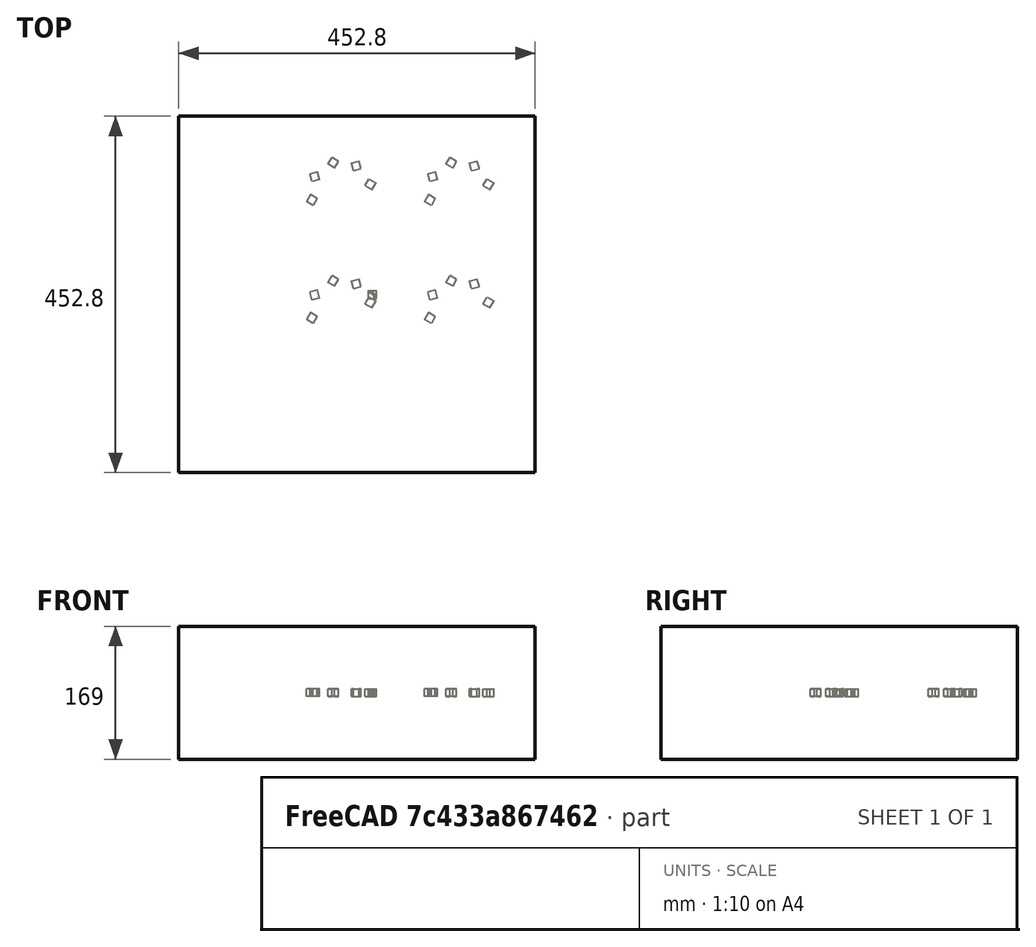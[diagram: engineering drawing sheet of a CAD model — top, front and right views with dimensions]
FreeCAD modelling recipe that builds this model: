
FCSTD DOCUMENT  (FreeCAD 1.0R39109 (Git))
Label: orthoArray-of-polarArray-of-Part
License: All rights reserved
LicenseURL: http://en.wikipedia.org/wiki/All_rights_reserved
objects: App::DocumentObjectGroupPython×1251, Part::FeaturePython×5, App::Part×5
note: 4 computed .brp shape members not serialized (recipe doc carries the construction recipe); baked Part::Feature solids carry a one-line shape summary decoded from their .brp

FEATURE [App::DocumentObjectGroupPython] HALFPI  # scripted group (container) (typed FeaturePython)
  name = HALFPI
  value = pi/2.
FEATURE [App::DocumentObjectGroupPython] PI  # scripted group (container) (typed FeaturePython)
  name = PI
  value = 1.*pi
FEATURE [App::DocumentObjectGroupPython] TWOPI  # scripted group (container) (typed FeaturePython)
  name = TWOPI
  value = 2.*pi
FEATURE [App::DocumentObjectGroupPython] Constants  # scripted group (container) (typed FeaturePython)
  Group = -> [HALFPI,PI,TWOPI]
FEATURE [App::DocumentObjectGroupPython] Variables  # scripted group (container) (typed FeaturePython)
FEATURE [App::DocumentObjectGroupPython] Quantities  # scripted group (container) (typed FeaturePython)
FEATURE [App::DocumentObjectGroupPython] Isotopes  # scripted group (container) (typed FeaturePython)
FEATURE [App::DocumentObjectGroupPython] Elements  # scripted group (container) (typed FeaturePython)
FEATURE [App::DocumentObjectGroupPython] Matrix  # scripted group (container) (typed FeaturePython)
FEATURE [App::DocumentObjectGroupPython] Surfaces  # scripted group (container) (typed FeaturePython)
FEATURE [App::DocumentObjectGroupPython] Opticals  # scripted group (container) (typed FeaturePython)
  Group = -> [Matrix,Surfaces]
FEATURE [App::DocumentObjectGroupPython] G4Isotopes  # scripted group (container) (typed FeaturePython)
FEATURE [App::DocumentObjectGroupPython] H_element  # scripted group (container) (typed FeaturePython)
  Z = 1
  atom_value = 1.008
  formula = H
  name = H_element
FEATURE [App::DocumentObjectGroupPython] He_element  # scripted group (container) (typed FeaturePython)
  Z = 2
  atom_value = 4.0026
  formula = He
  name = He_element
FEATURE [App::DocumentObjectGroupPython] Li_element  # scripted group (container) (typed FeaturePython)
  Z = 3
  atom_value = 6.94
  formula = Li
  name = Li_element
FEATURE [App::DocumentObjectGroupPython] Be_element  # scripted group (container) (typed FeaturePython)
  Z = 4
  atom_value = 9.01218
  formula = Be
  name = Be_element
FEATURE [App::DocumentObjectGroupPython] B_element  # scripted group (container) (typed FeaturePython)
  Z = 5
  atom_value = 10.81
  formula = B
  name = B_element
FEATURE [App::DocumentObjectGroupPython] C_element  # scripted group (container) (typed FeaturePython)
  Z = 6
  atom_value = 12.011
  formula = C
  name = C_element
FEATURE [App::DocumentObjectGroupPython] N_element  # scripted group (container) (typed FeaturePython)
  Z = 7
  atom_value = 14.007
  formula = N
  name = N_element
FEATURE [App::DocumentObjectGroupPython] O_element  # scripted group (container) (typed FeaturePython)
  Z = 8
  atom_value = 15.999
  formula = O
  name = O_element
FEATURE [App::DocumentObjectGroupPython] F_element  # scripted group (container) (typed FeaturePython)
  Z = 9
  atom_value = 18.9984
  formula = F
  name = F_element
FEATURE [App::DocumentObjectGroupPython] Ne_element  # scripted group (container) (typed FeaturePython)
  Z = 10
  atom_value = 20.1797
  formula = Ne
  name = Ne_element
FEATURE [App::DocumentObjectGroupPython] Na_element  # scripted group (container) (typed FeaturePython)
  Z = 11
  atom_value = 22.9898
  formula = Na
  name = Na_element
FEATURE [App::DocumentObjectGroupPython] Mg_element  # scripted group (container) (typed FeaturePython)
  Z = 12
  atom_value = 24.305
  formula = Mg
  name = Mg_element
FEATURE [App::DocumentObjectGroupPython] Al_element  # scripted group (container) (typed FeaturePython)
  Z = 13
  atom_value = 26.9815
  formula = Al
  name = Al_element
FEATURE [App::DocumentObjectGroupPython] Si_element  # scripted group (container) (typed FeaturePython)
  Z = 14
  atom_value = 28.085
  formula = Si
  name = Si_element
FEATURE [App::DocumentObjectGroupPython] P_element  # scripted group (container) (typed FeaturePython)
  Z = 15
  atom_value = 30.9738
  formula = P
  name = P_element
FEATURE [App::DocumentObjectGroupPython] S_element  # scripted group (container) (typed FeaturePython)
  Z = 16
  atom_value = 32.06
  formula = S
  name = S_element
FEATURE [App::DocumentObjectGroupPython] Cl_element  # scripted group (container) (typed FeaturePython)
  Z = 17
  atom_value = 35.45
  formula = Cl
  name = Cl_element
FEATURE [App::DocumentObjectGroupPython] Ar_element  # scripted group (container) (typed FeaturePython)
  Z = 18
  atom_value = 39.95
  formula = Ar
  name = Ar_element
FEATURE [App::DocumentObjectGroupPython] K_element  # scripted group (container) (typed FeaturePython)
  Z = 19
  atom_value = 39.0983
  formula = K
  name = K_element
FEATURE [App::DocumentObjectGroupPython] Ca_element  # scripted group (container) (typed FeaturePython)
  Z = 20
  atom_value = 40.078
  formula = Ca
  name = Ca_element
FEATURE [App::DocumentObjectGroupPython] Sc_element  # scripted group (container) (typed FeaturePython)
  Z = 21
  atom_value = 44.9559
  formula = Sc
  name = Sc_element
FEATURE [App::DocumentObjectGroupPython] Ti_element  # scripted group (container) (typed FeaturePython)
  Z = 22
  atom_value = 47.867
  formula = Ti
  name = Ti_element
FEATURE [App::DocumentObjectGroupPython] V_element  # scripted group (container) (typed FeaturePython)
  Z = 23
  atom_value = 50.9415
  formula = V
  name = V_element
FEATURE [App::DocumentObjectGroupPython] Cr_element  # scripted group (container) (typed FeaturePython)
  Z = 24
  atom_value = 51.9961
  formula = Cr
  name = Cr_element
FEATURE [App::DocumentObjectGroupPython] Mn_element  # scripted group (container) (typed FeaturePython)
  Z = 25
  atom_value = 54.938
  formula = Mn
  name = Mn_element
FEATURE [App::DocumentObjectGroupPython] Fe_element  # scripted group (container) (typed FeaturePython)
  Z = 26
  atom_value = 55.845
  formula = Fe
  name = Fe_element
FEATURE [App::DocumentObjectGroupPython] Co_element  # scripted group (container) (typed FeaturePython)
  Z = 27
  atom_value = 58.9332
  formula = Co
  name = Co_element
FEATURE [App::DocumentObjectGroupPython] Ni_element  # scripted group (container) (typed FeaturePython)
  Z = 28
  atom_value = 58.6934
  formula = Ni
  name = Ni_element
FEATURE [App::DocumentObjectGroupPython] Cu_element  # scripted group (container) (typed FeaturePython)
  Z = 29
  atom_value = 63.546
  formula = Cu
  name = Cu_element
FEATURE [App::DocumentObjectGroupPython] Zn_element  # scripted group (container) (typed FeaturePython)
  Z = 30
  atom_value = 65.38
  formula = Zn
  name = Zn_element
FEATURE [App::DocumentObjectGroupPython] Ga_element  # scripted group (container) (typed FeaturePython)
  Z = 31
  atom_value = 69.723
  formula = Ga
  name = Ga_element
FEATURE [App::DocumentObjectGroupPython] Ge_element  # scripted group (container) (typed FeaturePython)
  Z = 32
  atom_value = 72.63
  formula = Ge
  name = Ge_element
FEATURE [App::DocumentObjectGroupPython] As_element  # scripted group (container) (typed FeaturePython)
  Z = 33
  atom_value = 74.9216
  formula = As
  name = As_element
FEATURE [App::DocumentObjectGroupPython] Se_element  # scripted group (container) (typed FeaturePython)
  Z = 34
  atom_value = 78.971
  formula = Se
  name = Se_element
FEATURE [App::DocumentObjectGroupPython] Br_element  # scripted group (container) (typed FeaturePython)
  Z = 35
  atom_value = 79.904
  formula = Br
  name = Br_element
FEATURE [App::DocumentObjectGroupPython] Kr_element  # scripted group (container) (typed FeaturePython)
  Z = 36
  atom_value = 83.798
  formula = Kr
  name = Kr_element
FEATURE [App::DocumentObjectGroupPython] Rb_element  # scripted group (container) (typed FeaturePython)
  Z = 37
  atom_value = 85.4678
  formula = Rb
  name = Rb_element
FEATURE [App::DocumentObjectGroupPython] Sr_element  # scripted group (container) (typed FeaturePython)
  Z = 38
  atom_value = 87.62
  formula = Sr
  name = Sr_element
FEATURE [App::DocumentObjectGroupPython] Y_element  # scripted group (container) (typed FeaturePython)
  Z = 39
  atom_value = 88.9058
  formula = Y
  name = Y_element
FEATURE [App::DocumentObjectGroupPython] Zr_element  # scripted group (container) (typed FeaturePython)
  Z = 40
  atom_value = 91.224
  formula = Zr
  name = Zr_element
FEATURE [App::DocumentObjectGroupPython] Nb_element  # scripted group (container) (typed FeaturePython)
  Z = 41
  atom_value = 92.9064
  formula = Nb
  name = Nb_element
FEATURE [App::DocumentObjectGroupPython] Mo_element  # scripted group (container) (typed FeaturePython)
  Z = 42
  atom_value = 95.95
  formula = Mo
  name = Mo_element
FEATURE [App::DocumentObjectGroupPython] Tc_element  # scripted group (container) (typed FeaturePython)
  Z = 43
  atom_value = 97
  formula = Tc
  name = Tc_element
FEATURE [App::DocumentObjectGroupPython] Ru_element  # scripted group (container) (typed FeaturePython)
  Z = 44
  atom_value = 101.07
  formula = Ru
  name = Ru_element
FEATURE [App::DocumentObjectGroupPython] Rh_element  # scripted group (container) (typed FeaturePython)
  Z = 45
  atom_value = 102.905
  formula = Rh
  name = Rh_element
FEATURE [App::DocumentObjectGroupPython] Pd_element  # scripted group (container) (typed FeaturePython)
  Z = 46
  atom_value = 106.42
  formula = Pd
  name = Pd_element
FEATURE [App::DocumentObjectGroupPython] Ag_element  # scripted group (container) (typed FeaturePython)
  Z = 47
  atom_value = 107.868
  formula = Ag
  name = Ag_element
FEATURE [App::DocumentObjectGroupPython] Cd_element  # scripted group (container) (typed FeaturePython)
  Z = 48
  atom_value = 112.414
  formula = Cd
  name = Cd_element
FEATURE [App::DocumentObjectGroupPython] In_element  # scripted group (container) (typed FeaturePython)
  Z = 49
  atom_value = 114.818
  formula = In
  name = In_element
FEATURE [App::DocumentObjectGroupPython] Sn_element  # scripted group (container) (typed FeaturePython)
  Z = 50
  atom_value = 118.71
  formula = Sn
  name = Sn_element
FEATURE [App::DocumentObjectGroupPython] Sb_element  # scripted group (container) (typed FeaturePython)
  Z = 51
  atom_value = 121.76
  formula = Sb
  name = Sb_element
FEATURE [App::DocumentObjectGroupPython] Te_element  # scripted group (container) (typed FeaturePython)
  Z = 52
  atom_value = 127.6
  formula = Te
  name = Te_element
FEATURE [App::DocumentObjectGroupPython] I_element  # scripted group (container) (typed FeaturePython)
  Z = 53
  atom_value = 126.904
  formula = I
  name = I_element
FEATURE [App::DocumentObjectGroupPython] Xe_element  # scripted group (container) (typed FeaturePython)
  Z = 54
  atom_value = 131.293
  formula = Xe
  name = Xe_element
FEATURE [App::DocumentObjectGroupPython] Cs_element  # scripted group (container) (typed FeaturePython)
  Z = 55
  atom_value = 132.905
  formula = Cs
  name = Cs_element
FEATURE [App::DocumentObjectGroupPython] Ba_element  # scripted group (container) (typed FeaturePython)
  Z = 56
  atom_value = 137.327
  formula = Ba
  name = Ba_element
FEATURE [App::DocumentObjectGroupPython] La_element  # scripted group (container) (typed FeaturePython)
  Z = 57
  atom_value = 138.905
  formula = La
  name = La_element
FEATURE [App::DocumentObjectGroupPython] Ce_element  # scripted group (container) (typed FeaturePython)
  Z = 58
  atom_value = 140.116
  formula = Ce
  name = Ce_element
FEATURE [App::DocumentObjectGroupPython] Pr_element  # scripted group (container) (typed FeaturePython)
  Z = 59
  atom_value = 140.908
  formula = Pr
  name = Pr_element
FEATURE [App::DocumentObjectGroupPython] Nd_element  # scripted group (container) (typed FeaturePython)
  Z = 60
  atom_value = 144.242
  formula = Nd
  name = Nd_element
FEATURE [App::DocumentObjectGroupPython] Pm_element  # scripted group (container) (typed FeaturePython)
  Z = 61
  atom_value = 145
  formula = Pm
  name = Pm_element
FEATURE [App::DocumentObjectGroupPython] Sm_element  # scripted group (container) (typed FeaturePython)
  Z = 62
  atom_value = 150.36
  formula = Sm
  name = Sm_element
FEATURE [App::DocumentObjectGroupPython] Eu_element  # scripted group (container) (typed FeaturePython)
  Z = 63
  atom_value = 151.964
  formula = Eu
  name = Eu_element
FEATURE [App::DocumentObjectGroupPython] Gd_element  # scripted group (container) (typed FeaturePython)
  Z = 64
  atom_value = 157.25
  formula = Gd
  name = Gd_element
FEATURE [App::DocumentObjectGroupPython] Tb_element  # scripted group (container) (typed FeaturePython)
  Z = 65
  atom_value = 158.925
  formula = Tb
  name = Tb_element
FEATURE [App::DocumentObjectGroupPython] Dy_element  # scripted group (container) (typed FeaturePython)
  Z = 66
  atom_value = 162.5
  formula = Dy
  name = Dy_element
FEATURE [App::DocumentObjectGroupPython] Ho_element  # scripted group (container) (typed FeaturePython)
  Z = 67
  atom_value = 164.93
  formula = Ho
  name = Ho_element
FEATURE [App::DocumentObjectGroupPython] Er_element  # scripted group (container) (typed FeaturePython)
  Z = 68
  atom_value = 167.259
  formula = Er
  name = Er_element
FEATURE [App::DocumentObjectGroupPython] Tm_element  # scripted group (container) (typed FeaturePython)
  Z = 69
  atom_value = 168.934
  formula = Tm
  name = Tm_element
FEATURE [App::DocumentObjectGroupPython] Yb_element  # scripted group (container) (typed FeaturePython)
  Z = 70
  atom_value = 173.045
  formula = Yb
  name = Yb_element
FEATURE [App::DocumentObjectGroupPython] Lu_element  # scripted group (container) (typed FeaturePython)
  Z = 71
  atom_value = 174.967
  formula = Lu
  name = Lu_element
FEATURE [App::DocumentObjectGroupPython] Hf_element  # scripted group (container) (typed FeaturePython)
  Z = 72
  atom_value = 178.49
  formula = Hf
  name = Hf_element
FEATURE [App::DocumentObjectGroupPython] Ta_element  # scripted group (container) (typed FeaturePython)
  Z = 73
  atom_value = 180.948
  formula = Ta
  name = Ta_element
FEATURE [App::DocumentObjectGroupPython] W_element  # scripted group (container) (typed FeaturePython)
  Z = 74
  atom_value = 183.84
  formula = W
  name = W_element
FEATURE [App::DocumentObjectGroupPython] Re_element  # scripted group (container) (typed FeaturePython)
  Z = 75
  atom_value = 186.207
  formula = Re
  name = Re_element
FEATURE [App::DocumentObjectGroupPython] Os_element  # scripted group (container) (typed FeaturePython)
  Z = 76
  atom_value = 190.23
  formula = Os
  name = Os_element
FEATURE [App::DocumentObjectGroupPython] Ir_element  # scripted group (container) (typed FeaturePython)
  Z = 77
  atom_value = 192.217
  formula = Ir
  name = Ir_element
FEATURE [App::DocumentObjectGroupPython] Pt_element  # scripted group (container) (typed FeaturePython)
  Z = 78
  atom_value = 195.084
  formula = Pt
  name = Pt_element
FEATURE [App::DocumentObjectGroupPython] Au_element  # scripted group (container) (typed FeaturePython)
  Z = 79
  atom_value = 196.967
  formula = Au
  name = Au_element
FEATURE [App::DocumentObjectGroupPython] Hg_element  # scripted group (container) (typed FeaturePython)
  Z = 80
  atom_value = 200.592
  formula = Hg
  name = Hg_element
FEATURE [App::DocumentObjectGroupPython] Tl_element  # scripted group (container) (typed FeaturePython)
  Z = 81
  atom_value = 204.38
  formula = Tl
  name = Tl_element
FEATURE [App::DocumentObjectGroupPython] Pb_element  # scripted group (container) (typed FeaturePython)
  Z = 82
  atom_value = 207.2
  formula = Pb
  name = Pb_element
FEATURE [App::DocumentObjectGroupPython] Bi_element  # scripted group (container) (typed FeaturePython)
  Z = 83
  atom_value = 208.98
  formula = Bi
  name = Bi_element
FEATURE [App::DocumentObjectGroupPython] Po_element  # scripted group (container) (typed FeaturePython)
  Z = 84
  atom_value = 209
  formula = Po
  name = Po_element
FEATURE [App::DocumentObjectGroupPython] At_element  # scripted group (container) (typed FeaturePython)
  Z = 85
  atom_value = 210
  formula = At
  name = At_element
FEATURE [App::DocumentObjectGroupPython] Rn_element  # scripted group (container) (typed FeaturePython)
  Z = 86
  atom_value = 222
  formula = Rn
  name = Rn_element
FEATURE [App::DocumentObjectGroupPython] Fr_element  # scripted group (container) (typed FeaturePython)
  Z = 87
  atom_value = 223
  formula = Fr
  name = Fr_element
FEATURE [App::DocumentObjectGroupPython] Ra_element  # scripted group (container) (typed FeaturePython)
  Z = 88
  atom_value = 226
  formula = Ra
  name = Ra_element
FEATURE [App::DocumentObjectGroupPython] Ac_element  # scripted group (container) (typed FeaturePython)
  Z = 89
  atom_value = 227
  formula = Ac
  name = Ac_element
FEATURE [App::DocumentObjectGroupPython] Th_element  # scripted group (container) (typed FeaturePython)
  Z = 90
  atom_value = 232.038
  formula = Th
  name = Th_element
FEATURE [App::DocumentObjectGroupPython] Pa_element  # scripted group (container) (typed FeaturePython)
  Z = 91
  atom_value = 231.036
  formula = Pa
  name = Pa_element
FEATURE [App::DocumentObjectGroupPython] U_element  # scripted group (container) (typed FeaturePython)
  Z = 92
  atom_value = 238.029
  formula = U
  name = U_element
FEATURE [App::DocumentObjectGroupPython] Np_element  # scripted group (container) (typed FeaturePython)
  Z = 93
  atom_value = 237
  formula = Np
  name = Np_element
FEATURE [App::DocumentObjectGroupPython] Pu_element  # scripted group (container) (typed FeaturePython)
  Z = 94
  atom_value = 244
  formula = Pu
  name = Pu_element
FEATURE [App::DocumentObjectGroupPython] Am_element  # scripted group (container) (typed FeaturePython)
  Z = 95
  atom_value = 243
  formula = Am
  name = Am_element
FEATURE [App::DocumentObjectGroupPython] Cm_element  # scripted group (container) (typed FeaturePython)
  Z = 96
  atom_value = 247
  formula = Cm
  name = Cm_element
FEATURE [App::DocumentObjectGroupPython] Bk_element  # scripted group (container) (typed FeaturePython)
  Z = 97
  atom_value = 247
  formula = Bk
  name = Bk_element
FEATURE [App::DocumentObjectGroupPython] Cf_element  # scripted group (container) (typed FeaturePython)
  Z = 98
  atom_value = 251
  formula = Cf
  name = Cf_element
FEATURE [App::DocumentObjectGroupPython] G4Elements  # scripted group (container) (typed FeaturePython)
  Group = -> [H_element,He_element,Li_element,Be_element,B_element,C_element,N_element,O_element,F_element,Ne_element,Na_element,Mg_element,Al_element,Si_element,P_element,S_element,Cl_element,Ar_element,K_element,Ca_element,Sc_element,Ti_element,V_element,Cr_element,Mn_element,Fe_element,Co_element,Ni_element,Cu_element,Zn_element,Ga_element,Ge_element,As_element,Se_element,Br_element,Kr_element,Rb_element,+61 more]
FEATURE [App::DocumentObjectGroupPython] H_element001  label="H_element : 0.101"  # scripted group (container) (typed FeaturePython)
  n = 0.101327
FEATURE [App::DocumentObjectGroupPython] C_element001  label="C_element : 0.775"  # scripted group (container) (typed FeaturePython)
  n = 0.7755
FEATURE [App::DocumentObjectGroupPython] N_element001  label="N_element : 0.035"  # scripted group (container) (typed FeaturePython)
  n = 0.035057
FEATURE [App::DocumentObjectGroupPython] O_element001  label="O_element : 0.052"  # scripted group (container) (typed FeaturePython)
  n = 0.0523159
FEATURE [App::DocumentObjectGroupPython] F_element001  label="F_element : 0.017"  # scripted group (container) (typed FeaturePython)
  n = 0.017422
FEATURE [App::DocumentObjectGroupPython] Ca_element001  label="Ca_element : 0.018"  # scripted group (container) (typed FeaturePython)
  n = 0.018378
FEATURE [App::DocumentObjectGroupPython] G4_A_150_TISSUE  label="G4_A-150_TISSUE"  # scripted group (container) (typed FeaturePython)
  Dunit = g/cm3
  Dvalue = 1.127
  Group = -> [H_element001,C_element001,N_element001,O_element001,F_element001,Ca_element001]
  conduct = 2
  density = 1
  expand = 3
  formula = G4_A-150_TISSUE
  name = G4_A-150_TISSUE
  specific = 4
FEATURE [App::DocumentObjectGroupPython] C_element002  label="C_element : 3"  # scripted group (container) (typed FeaturePython)
  n = 3
  ref = C_element
FEATURE [App::DocumentObjectGroupPython] H_element002  label="H_element : 6"  # scripted group (container) (typed FeaturePython)
  n = 6
  ref = H_element
FEATURE [App::DocumentObjectGroupPython] O_element002  label="O_element : 1"  # scripted group (container) (typed FeaturePython)
  n = 1
  ref = O_element
FEATURE [App::DocumentObjectGroupPython] G4_ACETONE  # scripted group (container) (typed FeaturePython)
  Dunit = g/cm3
  Dvalue = 0.7899
  Group = -> [C_element002,H_element002,O_element002]
  conduct = 2
  density = 1
  expand = 3
  formula = G4_ACETONE
  name = G4_ACETONE
  specific = 4
FEATURE [App::DocumentObjectGroupPython] C_element003  label="C_element : 2"  # scripted group (container) (typed FeaturePython)
  n = 2
  ref = C_element
FEATURE [App::DocumentObjectGroupPython] H_element003  label="H_element : 2"  # scripted group (container) (typed FeaturePython)
  n = 2
  ref = H_element
FEATURE [App::DocumentObjectGroupPython] G4_ACETYLENE  # scripted group (container) (typed FeaturePython)
  Dunit = g/cm3
  Dvalue = 0.0010967
  Group = -> [C_element003,H_element003]
  conduct = 2
  density = 1
  expand = 3
  formula = G4_ACETYLENE
  name = G4_ACETYLENE
  specific = 4
FEATURE [App::DocumentObjectGroupPython] C_element004  label="C_element : 5"  # scripted group (container) (typed FeaturePython)
  n = 5
  ref = C_element
FEATURE [App::DocumentObjectGroupPython] H_element004  label="H_element : 5"  # scripted group (container) (typed FeaturePython)
  n = 5
  ref = H_element
FEATURE [App::DocumentObjectGroupPython] N_element002  label="N_element : 5"  # scripted group (container) (typed FeaturePython)
  n = 5
  ref = N_element
FEATURE [App::DocumentObjectGroupPython] G4_ADENINE  # scripted group (container) (typed FeaturePython)
  Dunit = g/cm3
  Dvalue = 1.6
  Group = -> [C_element004,H_element004,N_element002]
  conduct = 2
  density = 1
  expand = 3
  formula = G4_ADENINE
  name = G4_ADENINE
  specific = 4
FEATURE [App::DocumentObjectGroupPython] H_element005  label="H_element : 0.114"  # scripted group (container) (typed FeaturePython)
  n = 0.114
FEATURE [App::DocumentObjectGroupPython] C_element005  label="C_element : 0.598"  # scripted group (container) (typed FeaturePython)
  n = 0.598
FEATURE [App::DocumentObjectGroupPython] N_element003  label="N_element : 0.007"  # scripted group (container) (typed FeaturePython)
  n = 0.007
FEATURE [App::DocumentObjectGroupPython] O_element003  label="O_element : 0.278"  # scripted group (container) (typed FeaturePython)
  n = 0.278
FEATURE [App::DocumentObjectGroupPython] Na_element001  label="Na_element : 0.001"  # scripted group (container) (typed FeaturePython)
  n = 0.001
FEATURE [App::DocumentObjectGroupPython] S_element001  label="S_element : 0.001"  # scripted group (container) (typed FeaturePython)
  n = 0.001
FEATURE [App::DocumentObjectGroupPython] Cl_element001  label="Cl_element : 0.001"  # scripted group (container) (typed FeaturePython)
  n = 0.001
FEATURE [App::DocumentObjectGroupPython] G4_ADIPOSE_TISSUE_ICRP  # scripted group (container) (typed FeaturePython)
  Dunit = g/cm3
  Dvalue = 0.95
  Group = -> [H_element005,C_element005,N_element003,O_element003,Na_element001,S_element001,Cl_element001]
  conduct = 2
  density = 1
  expand = 3
  formula = G4_ADIPOSE_TISSUE_ICRP
  name = G4_ADIPOSE_TISSUE_ICRP
  specific = 4
FEATURE [App::DocumentObjectGroupPython] C_element006  label="C_element : 0.000"  # scripted group (container) (typed FeaturePython)
  n = 0.000124
FEATURE [App::DocumentObjectGroupPython] N_element004  label="N_element : 0.755"  # scripted group (container) (typed FeaturePython)
  n = 0.755268
FEATURE [App::DocumentObjectGroupPython] O_element004  label="O_element : 0.232"  # scripted group (container) (typed FeaturePython)
  n = 0.231781
FEATURE [App::DocumentObjectGroupPython] Ar_element001  label="Ar_element : 0.013"  # scripted group (container) (typed FeaturePython)
  n = 0.012827
FEATURE [App::DocumentObjectGroupPython] G4_AIR  # scripted group (container) (typed FeaturePython)
  Dunit = g/cm3
  Dvalue = 0.00120479
  Group = -> [C_element006,N_element004,O_element004,Ar_element001]
  conduct = 2
  density = 1
  expand = 3
  formula = G4_AIR
  name = G4_AIR
  specific = 4
FEATURE [App::DocumentObjectGroupPython] C_element007  label="C_element : 006"  # scripted group (container) (typed FeaturePython)
  n = 3
  ref = C_element
FEATURE [App::DocumentObjectGroupPython] H_element006  label="H_element : 7"  # scripted group (container) (typed FeaturePython)
  n = 7
  ref = H_element
FEATURE [App::DocumentObjectGroupPython] N_element005  label="N_element : 1"  # scripted group (container) (typed FeaturePython)
  n = 1
  ref = N_element
FEATURE [App::DocumentObjectGroupPython] O_element005  label="O_element : 2"  # scripted group (container) (typed FeaturePython)
  n = 2
  ref = O_element
FEATURE [App::DocumentObjectGroupPython] G4_ALANINE  # scripted group (container) (typed FeaturePython)
  Dunit = g/cm3
  Dvalue = 1.42
  Group = -> [C_element007,H_element006,N_element005,O_element005]
  conduct = 2
  density = 1
  expand = 3
  formula = G4_ALANINE
  name = G4_ALANINE
  specific = 4
FEATURE [App::DocumentObjectGroupPython] Al_element001  label="Al_element : 2"  # scripted group (container) (typed FeaturePython)
  n = 2
  ref = Al_element
FEATURE [App::DocumentObjectGroupPython] O_element006  label="O_element : 3"  # scripted group (container) (typed FeaturePython)
  n = 3
  ref = O_element
FEATURE [App::DocumentObjectGroupPython] G4_ALUMINUM_OXIDE  # scripted group (container) (typed FeaturePython)
  Dunit = g/cm3
  Dvalue = 3.97
  Group = -> [Al_element001,O_element006]
  conduct = 2
  density = 1
  expand = 3
  formula = G4_ALUMINUM_OXIDE
  name = G4_ALUMINUM_OXIDE
  specific = 4
FEATURE [App::DocumentObjectGroupPython] H_element007  label="H_element : 0.106"  # scripted group (container) (typed FeaturePython)
  n = 0.10593
FEATURE [App::DocumentObjectGroupPython] C_element008  label="C_element : 0.789"  # scripted group (container) (typed FeaturePython)
  n = 0.788974
FEATURE [App::DocumentObjectGroupPython] O_element007  label="O_element : 0.105"  # scripted group (container) (typed FeaturePython)
  n = 0.105096
FEATURE [App::DocumentObjectGroupPython] G4_AMBER  # scripted group (container) (typed FeaturePython)
  Dunit = g/cm3
  Dvalue = 1.1
  Group = -> [H_element007,C_element008,O_element007]
  conduct = 2
  density = 1
  expand = 3
  formula = G4_AMBER
  name = G4_AMBER
  specific = 4
FEATURE [App::DocumentObjectGroupPython] N_element006  label="N_element : 006"  # scripted group (container) (typed FeaturePython)
  n = 1
  ref = N_element
FEATURE [App::DocumentObjectGroupPython] H_element008  label="H_element : 3"  # scripted group (container) (typed FeaturePython)
  n = 3
  ref = H_element
FEATURE [App::DocumentObjectGroupPython] G4_AMMONIA  # scripted group (container) (typed FeaturePython)
  Dunit = g/cm3
  Dvalue = 0.000826019
  Group = -> [N_element006,H_element008]
  conduct = 2
  density = 1
  expand = 3
  formula = G4_AMMONIA
  name = G4_AMMONIA
  specific = 4
FEATURE [App::DocumentObjectGroupPython] C_element009  label="C_element : 6"  # scripted group (container) (typed FeaturePython)
  n = 6
  ref = C_element
FEATURE [App::DocumentObjectGroupPython] H_element009  label="H_element : 008"  # scripted group (container) (typed FeaturePython)
  n = 7
  ref = H_element
FEATURE [App::DocumentObjectGroupPython] N_element007  label="N_element : 007"  # scripted group (container) (typed FeaturePython)
  n = 1
  ref = N_element
FEATURE [App::DocumentObjectGroupPython] G4_ANILINE  # scripted group (container) (typed FeaturePython)
  Dunit = g/cm3
  Dvalue = 1.0235
  Group = -> [C_element009,H_element009,N_element007]
  conduct = 2
  density = 1
  expand = 3
  formula = G4_ANILINE
  name = G4_ANILINE
  specific = 4
FEATURE [App::DocumentObjectGroupPython] C_element010  label="C_element : 14"  # scripted group (container) (typed FeaturePython)
  n = 14
  ref = C_element
FEATURE [App::DocumentObjectGroupPython] H_element010  label="H_element : 10"  # scripted group (container) (typed FeaturePython)
  n = 10
  ref = H_element
FEATURE [App::DocumentObjectGroupPython] G4_ANTHRACENE  # scripted group (container) (typed FeaturePython)
  Dunit = g/cm3
  Dvalue = 1.283
  Group = -> [C_element010,H_element010]
  conduct = 2
  density = 1
  expand = 3
  formula = G4_ANTHRACENE
  name = G4_ANTHRACENE
  specific = 4
FEATURE [App::DocumentObjectGroupPython] H_element011  label="H_element : 0.065"  # scripted group (container) (typed FeaturePython)
  n = 0.0654709
FEATURE [App::DocumentObjectGroupPython] C_element011  label="C_element : 0.537"  # scripted group (container) (typed FeaturePython)
  n = 0.536944
FEATURE [App::DocumentObjectGroupPython] N_element008  label="N_element : 0.021"  # scripted group (container) (typed FeaturePython)
  n = 0.0215
FEATURE [App::DocumentObjectGroupPython] O_element008  label="O_element : 0.032"  # scripted group (container) (typed FeaturePython)
  n = 0.032085
FEATURE [App::DocumentObjectGroupPython] F_element002  label="F_element : 0.167"  # scripted group (container) (typed FeaturePython)
  n = 0.167411
FEATURE [App::DocumentObjectGroupPython] Ca_element002  label="Ca_element : 0.177"  # scripted group (container) (typed FeaturePython)
  n = 0.176589
FEATURE [App::DocumentObjectGroupPython] G4_B_100_BONE  label="G4_B-100_BONE"  # scripted group (container) (typed FeaturePython)
  Dunit = g/cm3
  Dvalue = 1.45
  Group = -> [H_element011,C_element011,N_element008,O_element008,F_element002,Ca_element002]
  conduct = 2
  density = 1
  expand = 3
  formula = G4_B-100_BONE
  name = G4_B-100_BONE
  specific = 4
FEATURE [App::DocumentObjectGroupPython] H_element012  label="H_element : 0.057"  # scripted group (container) (typed FeaturePython)
  n = 0.057441
FEATURE [App::DocumentObjectGroupPython] C_element012  label="C_element : 0.790"  # scripted group (container) (typed FeaturePython)
  n = 0.774591
FEATURE [App::DocumentObjectGroupPython] O_element009  label="O_element : 0.168"  # scripted group (container) (typed FeaturePython)
  n = 0.167968
FEATURE [App::DocumentObjectGroupPython] G4_BAKELITE  # scripted group (container) (typed FeaturePython)
  Dunit = g/cm3
  Dvalue = 1.25
  Group = -> [H_element012,C_element012,O_element009]
  conduct = 2
  density = 1
  expand = 3
  formula = G4_BAKELITE
  name = G4_BAKELITE
  specific = 4
FEATURE [App::DocumentObjectGroupPython] Ba_element001  label="Ba_element : 1"  # scripted group (container) (typed FeaturePython)
  n = 1
  ref = Ba_element
FEATURE [App::DocumentObjectGroupPython] F_element003  label="F_element : 2"  # scripted group (container) (typed FeaturePython)
  n = 2
  ref = F_element
FEATURE [App::DocumentObjectGroupPython] G4_BARIUM_FLUORIDE  # scripted group (container) (typed FeaturePython)
  Dunit = g/cm3
  Dvalue = 4.89
  Group = -> [Ba_element001,F_element003]
  conduct = 2
  density = 1
  expand = 3
  formula = G4_BARIUM_FLUORIDE
  name = G4_BARIUM_FLUORIDE
  specific = 4
FEATURE [App::DocumentObjectGroupPython] Ba_element002  label="Ba_element : 002"  # scripted group (container) (typed FeaturePython)
  n = 1
  ref = Ba_element
FEATURE [App::DocumentObjectGroupPython] S_element002  label="S_element : 1"  # scripted group (container) (typed FeaturePython)
  n = 1
  ref = S_element
FEATURE [App::DocumentObjectGroupPython] O_element010  label="O_element : 4"  # scripted group (container) (typed FeaturePython)
  n = 4
  ref = O_element
FEATURE [App::DocumentObjectGroupPython] G4_BARIUM_SULFATE  # scripted group (container) (typed FeaturePython)
  Dunit = g/cm3
  Dvalue = 4.5
  Group = -> [Ba_element002,S_element002,O_element010]
  conduct = 2
  density = 1
  expand = 3
  formula = G4_BARIUM_SULFATE
  name = G4_BARIUM_SULFATE
  specific = 4
FEATURE [App::DocumentObjectGroupPython] C_element013  label="C_element : 007"  # scripted group (container) (typed FeaturePython)
  n = 6
  ref = C_element
FEATURE [App::DocumentObjectGroupPython] H_element013  label="H_element : 009"  # scripted group (container) (typed FeaturePython)
  n = 6
  ref = H_element
FEATURE [App::DocumentObjectGroupPython] G4_BENZENE  # scripted group (container) (typed FeaturePython)
  Dunit = g/cm3
  Dvalue = 0.87865
  Group = -> [C_element013,H_element013]
  conduct = 2
  density = 1
  expand = 3
  formula = G4_BENZENE
  name = G4_BENZENE
  specific = 4
FEATURE [App::DocumentObjectGroupPython] Be_element001  label="Be_element : 1"  # scripted group (container) (typed FeaturePython)
  n = 1
  ref = Be_element
FEATURE [App::DocumentObjectGroupPython] O_element011  label="O_element : 005"  # scripted group (container) (typed FeaturePython)
  n = 1
  ref = O_element
FEATURE [App::DocumentObjectGroupPython] G4_BERYLLIUM_OXIDE  # scripted group (container) (typed FeaturePython)
  Dunit = g/cm3
  Dvalue = 3.01
  Group = -> [Be_element001,O_element011]
  conduct = 2
  density = 1
  expand = 3
  formula = G4_BERYLLIUM_OXIDE
  name = G4_BERYLLIUM_OXIDE
  specific = 4
FEATURE [App::DocumentObjectGroupPython] Bi_element001  label="Bi_element : 4"  # scripted group (container) (typed FeaturePython)
  n = 4
  ref = Bi_element
FEATURE [App::DocumentObjectGroupPython] Ge_element001  label="Ge_element : 3"  # scripted group (container) (typed FeaturePython)
  n = 3
  ref = Ge_element
FEATURE [App::DocumentObjectGroupPython] O_element012  label="O_element : 12"  # scripted group (container) (typed FeaturePython)
  n = 12
  ref = O_element
FEATURE [App::DocumentObjectGroupPython] G4_BGO  # scripted group (container) (typed FeaturePython)
  Dunit = g/cm3
  Dvalue = 7.13
  Group = -> [Bi_element001,Ge_element001,O_element012]
  conduct = 2
  density = 1
  expand = 3
  formula = G4_BGO
  name = G4_BGO
  specific = 4
FEATURE [App::DocumentObjectGroupPython] H_element014  label="H_element : 0.102"  # scripted group (container) (typed FeaturePython)
  n = 0.102
FEATURE [App::DocumentObjectGroupPython] C_element014  label="C_element : 0.110"  # scripted group (container) (typed FeaturePython)
  n = 0.11
FEATURE [App::DocumentObjectGroupPython] N_element009  label="N_element : 0.033"  # scripted group (container) (typed FeaturePython)
  n = 0.033
FEATURE [App::DocumentObjectGroupPython] O_element013  label="O_element : 0.745"  # scripted group (container) (typed FeaturePython)
  n = 0.745
FEATURE [App::DocumentObjectGroupPython] Na_element002  label="Na_element : 0.002"  # scripted group (container) (typed FeaturePython)
  n = 0.001
FEATURE [App::DocumentObjectGroupPython] P_element001  label="P_element : 0.001"  # scripted group (container) (typed FeaturePython)
  n = 0.001
FEATURE [App::DocumentObjectGroupPython] S_element003  label="S_element : 0.002"  # scripted group (container) (typed FeaturePython)
  n = 0.002
FEATURE [App::DocumentObjectGroupPython] Cl_element002  label="Cl_element : 0.003"  # scripted group (container) (typed FeaturePython)
  n = 0.003
FEATURE [App::DocumentObjectGroupPython] K_element001  label="K_element : 0.002"  # scripted group (container) (typed FeaturePython)
  n = 0.002
FEATURE [App::DocumentObjectGroupPython] Fe_element001  label="Fe_element : 0.001"  # scripted group (container) (typed FeaturePython)
  n = 0.001
FEATURE [App::DocumentObjectGroupPython] G4_BLOOD_ICRP  # scripted group (container) (typed FeaturePython)
  Dunit = g/cm3
  Dvalue = 1.06
  Group = -> [H_element014,C_element014,N_element009,O_element013,Na_element002,P_element001,S_element003,Cl_element002,K_element001,Fe_element001]
  conduct = 2
  density = 1
  expand = 3
  formula = G4_BLOOD_ICRP
  name = G4_BLOOD_ICRP
  specific = 4
FEATURE [App::DocumentObjectGroupPython] H_element015  label="H_element : 0.064"  # scripted group (container) (typed FeaturePython)
  n = 0.064
FEATURE [App::DocumentObjectGroupPython] C_element015  label="C_element : 0.278"  # scripted group (container) (typed FeaturePython)
  n = 0.278
FEATURE [App::DocumentObjectGroupPython] N_element010  label="N_element : 0.027"  # scripted group (container) (typed FeaturePython)
  n = 0.027
FEATURE [App::DocumentObjectGroupPython] O_element014  label="O_element : 0.410"  # scripted group (container) (typed FeaturePython)
  n = 0.41
FEATURE [App::DocumentObjectGroupPython] Mg_element001  label="Mg_element : 0.002"  # scripted group (container) (typed FeaturePython)
  n = 0.002
FEATURE [App::DocumentObjectGroupPython] P_element002  label="P_element : 0.070"  # scripted group (container) (typed FeaturePython)
  n = 0.07
FEATURE [App::DocumentObjectGroupPython] S_element004  label="S_element : 0.003"  # scripted group (container) (typed FeaturePython)
  n = 0.002
FEATURE [App::DocumentObjectGroupPython] Ca_element003  label="Ca_element : 0.147"  # scripted group (container) (typed FeaturePython)
  n = 0.147
FEATURE [App::DocumentObjectGroupPython] G4_BONE_COMPACT_ICRU  # scripted group (container) (typed FeaturePython)
  Dunit = g/cm3
  Dvalue = 1.85
  Group = -> [H_element015,C_element015,N_element010,O_element014,Mg_element001,P_element002,S_element004,Ca_element003]
  conduct = 2
  density = 1
  expand = 3
  formula = G4_BONE_COMPACT_ICRU
  name = G4_BONE_COMPACT_ICRU
  specific = 4
FEATURE [App::DocumentObjectGroupPython] H_element016  label="H_element : 0.034"  # scripted group (container) (typed FeaturePython)
  n = 0.034
FEATURE [App::DocumentObjectGroupPython] C_element016  label="C_element : 0.155"  # scripted group (container) (typed FeaturePython)
  n = 0.155
FEATURE [App::DocumentObjectGroupPython] N_element011  label="N_element : 0.042"  # scripted group (container) (typed FeaturePython)
  n = 0.042
FEATURE [App::DocumentObjectGroupPython] O_element015  label="O_element : 0.435"  # scripted group (container) (typed FeaturePython)
  n = 0.435
FEATURE [App::DocumentObjectGroupPython] Na_element003  label="Na_element : 0.003"  # scripted group (container) (typed FeaturePython)
  n = 0.001
FEATURE [App::DocumentObjectGroupPython] Mg_element002  label="Mg_element : 0.003"  # scripted group (container) (typed FeaturePython)
  n = 0.002
FEATURE [App::DocumentObjectGroupPython] P_element003  label="P_element : 0.103"  # scripted group (container) (typed FeaturePython)
  n = 0.103
FEATURE [App::DocumentObjectGroupPython] S_element005  label="S_element : 0.004"  # scripted group (container) (typed FeaturePython)
  n = 0.003
FEATURE [App::DocumentObjectGroupPython] Ca_element004  label="Ca_element : 0.225"  # scripted group (container) (typed FeaturePython)
  n = 0.225
FEATURE [App::DocumentObjectGroupPython] G4_BONE_CORTICAL_ICRP  # scripted group (container) (typed FeaturePython)
  Dunit = g/cm3
  Dvalue = 1.92
  Group = -> [H_element016,C_element016,N_element011,O_element015,Na_element003,Mg_element002,P_element003,S_element005,Ca_element004]
  conduct = 2
  density = 1
  expand = 3
  formula = G4_BONE_CORTICAL_ICRP
  name = G4_BONE_CORTICAL_ICRP
  specific = 4
FEATURE [App::DocumentObjectGroupPython] B_element001  label="B_element : 4"  # scripted group (container) (typed FeaturePython)
  n = 4
  ref = B_element
FEATURE [App::DocumentObjectGroupPython] C_element017  label="C_element : 1"  # scripted group (container) (typed FeaturePython)
  n = 1
  ref = C_element
FEATURE [App::DocumentObjectGroupPython] G4_BORON_CARBIDE  # scripted group (container) (typed FeaturePython)
  Dunit = g/cm3
  Dvalue = 2.52
  Group = -> [B_element001,C_element017]
  conduct = 2
  density = 1
  expand = 3
  formula = G4_BORON_CARBIDE
  name = G4_BORON_CARBIDE
  specific = 4
FEATURE [App::DocumentObjectGroupPython] B_element002  label="B_element : 2"  # scripted group (container) (typed FeaturePython)
  n = 2
  ref = B_element
FEATURE [App::DocumentObjectGroupPython] O_element016  label="O_element : 006"  # scripted group (container) (typed FeaturePython)
  n = 3
  ref = O_element
FEATURE [App::DocumentObjectGroupPython] G4_BORON_OXIDE  # scripted group (container) (typed FeaturePython)
  Dunit = g/cm3
  Dvalue = 1.812
  Group = -> [B_element002,O_element016]
  conduct = 2
  density = 1
  expand = 3
  formula = G4_BORON_OXIDE
  name = G4_BORON_OXIDE
  specific = 4
FEATURE [App::DocumentObjectGroupPython] H_element017  label="H_element : 0.107"  # scripted group (container) (typed FeaturePython)
  n = 0.107
FEATURE [App::DocumentObjectGroupPython] C_element018  label="C_element : 0.145"  # scripted group (container) (typed FeaturePython)
  n = 0.145
FEATURE [App::DocumentObjectGroupPython] N_element012  label="N_element : 0.022"  # scripted group (container) (typed FeaturePython)
  n = 0.022
FEATURE [App::DocumentObjectGroupPython] O_element017  label="O_element : 0.712"  # scripted group (container) (typed FeaturePython)
  n = 0.712
FEATURE [App::DocumentObjectGroupPython] Na_element004  label="Na_element : 0.004"  # scripted group (container) (typed FeaturePython)
  n = 0.002
FEATURE [App::DocumentObjectGroupPython] P_element004  label="P_element : 0.004"  # scripted group (container) (typed FeaturePython)
  n = 0.004
FEATURE [App::DocumentObjectGroupPython] S_element006  label="S_element : 0.005"  # scripted group (container) (typed FeaturePython)
  n = 0.002
FEATURE [App::DocumentObjectGroupPython] Cl_element003  label="Cl_element : 0.004"  # scripted group (container) (typed FeaturePython)
  n = 0.003
FEATURE [App::DocumentObjectGroupPython] K_element002  label="K_element : 0.003"  # scripted group (container) (typed FeaturePython)
  n = 0.003
FEATURE [App::DocumentObjectGroupPython] G4_BRAIN_ICRP  # scripted group (container) (typed FeaturePython)
  Dunit = g/cm3
  Dvalue = 1.04
  Group = -> [H_element017,C_element018,N_element012,O_element017,Na_element004,P_element004,S_element006,Cl_element003,K_element002]
  conduct = 2
  density = 1
  expand = 3
  formula = G4_BRAIN_ICRP
  name = G4_BRAIN_ICRP
  specific = 4
FEATURE [App::DocumentObjectGroupPython] C_element019  label="C_element : 4"  # scripted group (container) (typed FeaturePython)
  n = 4
  ref = C_element
FEATURE [App::DocumentObjectGroupPython] H_element018  label="H_element : 010"  # scripted group (container) (typed FeaturePython)
  n = 10
  ref = H_element
FEATURE [App::DocumentObjectGroupPython] G4_BUTANE  # scripted group (container) (typed FeaturePython)
  Dunit = g/cm3
  Dvalue = 0.00249343
  Group = -> [C_element019,H_element018]
  conduct = 2
  density = 1
  expand = 3
  formula = G4_BUTANE
  name = G4_BUTANE
  specific = 4
FEATURE [App::DocumentObjectGroupPython] C_element020  label="C_element : 008"  # scripted group (container) (typed FeaturePython)
  n = 4
  ref = C_element
FEATURE [App::DocumentObjectGroupPython] H_element019  label="H_element : 011"  # scripted group (container) (typed FeaturePython)
  n = 10
  ref = H_element
FEATURE [App::DocumentObjectGroupPython] O_element018  label="O_element : 007"  # scripted group (container) (typed FeaturePython)
  n = 1
  ref = O_element
FEATURE [App::DocumentObjectGroupPython] G4_N_BUTYL_ALCOHOL  label="G4_N-BUTYL_ALCOHOL"  # scripted group (container) (typed FeaturePython)
  Dunit = g/cm3
  Dvalue = 0.8098
  Group = -> [C_element020,H_element019,O_element018]
  conduct = 2
  density = 1
  expand = 3
  formula = G4_N-BUTYL_ALCOHOL
  name = G4_N-BUTYL_ALCOHOL
  specific = 4
FEATURE [App::DocumentObjectGroupPython] H_element020  label="H_element : 0.025"  # scripted group (container) (typed FeaturePython)
  n = 0.02468
FEATURE [App::DocumentObjectGroupPython] C_element021  label="C_element : 0.502"  # scripted group (container) (typed FeaturePython)
  n = 0.501611
FEATURE [App::DocumentObjectGroupPython] O_element019  label="O_element : 0.005"  # scripted group (container) (typed FeaturePython)
  n = 0.004527
FEATURE [App::DocumentObjectGroupPython] F_element004  label="F_element : 0.465"  # scripted group (container) (typed FeaturePython)
  n = 0.465209
FEATURE [App::DocumentObjectGroupPython] Si_element001  label="Si_element : 0.004"  # scripted group (container) (typed FeaturePython)
  n = 0.003973
FEATURE [App::DocumentObjectGroupPython] G4_C_552  label="G4_C-552"  # scripted group (container) (typed FeaturePython)
  Dunit = g/cm3
  Dvalue = 1.76
  Group = -> [H_element020,C_element021,O_element019,F_element004,Si_element001]
  conduct = 2
  density = 1
  expand = 3
  formula = G4_C-552
  name = G4_C-552
  specific = 4
FEATURE [App::DocumentObjectGroupPython] Cd_element001  label="Cd_element : 1"  # scripted group (container) (typed FeaturePython)
  n = 1
  ref = Cd_element
FEATURE [App::DocumentObjectGroupPython] Te_element001  label="Te_element : 1"  # scripted group (container) (typed FeaturePython)
  n = 1
  ref = Te_element
FEATURE [App::DocumentObjectGroupPython] G4_CADMIUM_TELLURIDE  # scripted group (container) (typed FeaturePython)
  Dunit = g/cm3
  Dvalue = 6.2
  Group = -> [Cd_element001,Te_element001]
  conduct = 2
  density = 1
  expand = 3
  formula = G4_CADMIUM_TELLURIDE
  name = G4_CADMIUM_TELLURIDE
  specific = 4
FEATURE [App::DocumentObjectGroupPython] Cd_element002  label="Cd_element : 002"  # scripted group (container) (typed FeaturePython)
  n = 1
  ref = Cd_element
FEATURE [App::DocumentObjectGroupPython] W_element001  label="W_element : 1"  # scripted group (container) (typed FeaturePython)
  n = 1
  ref = W_element
FEATURE [App::DocumentObjectGroupPython] O_element020  label="O_element : 008"  # scripted group (container) (typed FeaturePython)
  n = 4
  ref = O_element
FEATURE [App::DocumentObjectGroupPython] G4_CADMIUM_TUNGSTATE  # scripted group (container) (typed FeaturePython)
  Dunit = g/cm3
  Dvalue = 7.9
  Group = -> [Cd_element002,W_element001,O_element020]
  conduct = 2
  density = 1
  expand = 3
  formula = G4_CADMIUM_TUNGSTATE
  name = G4_CADMIUM_TUNGSTATE
  specific = 4
FEATURE [App::DocumentObjectGroupPython] Ca_element005  label="Ca_element : 1"  # scripted group (container) (typed FeaturePython)
  n = 1
  ref = Ca_element
FEATURE [App::DocumentObjectGroupPython] C_element022  label="C_element : 009"  # scripted group (container) (typed FeaturePython)
  n = 1
  ref = C_element
FEATURE [App::DocumentObjectGroupPython] O_element021  label="O_element : 009"  # scripted group (container) (typed FeaturePython)
  n = 3
  ref = O_element
FEATURE [App::DocumentObjectGroupPython] G4_CALCIUM_CARBONATE  # scripted group (container) (typed FeaturePython)
  Dunit = g/cm3
  Dvalue = 2.8
  Group = -> [Ca_element005,C_element022,O_element021]
  conduct = 2
  density = 1
  expand = 3
  formula = G4_CALCIUM_CARBONATE
  name = G4_CALCIUM_CARBONATE
  specific = 4
FEATURE [App::DocumentObjectGroupPython] Ca_element006  label="Ca_element : 002"  # scripted group (container) (typed FeaturePython)
  n = 1
  ref = Ca_element
FEATURE [App::DocumentObjectGroupPython] F_element005  label="F_element : 003"  # scripted group (container) (typed FeaturePython)
  n = 2
  ref = F_element
FEATURE [App::DocumentObjectGroupPython] G4_CALCIUM_FLUORIDE  # scripted group (container) (typed FeaturePython)
  Dunit = g/cm3
  Dvalue = 3.18
  Group = -> [Ca_element006,F_element005]
  conduct = 2
  density = 1
  expand = 3
  formula = G4_CALCIUM_FLUORIDE
  name = G4_CALCIUM_FLUORIDE
  specific = 4
FEATURE [App::DocumentObjectGroupPython] Ca_element007  label="Ca_element : 003"  # scripted group (container) (typed FeaturePython)
  n = 1
  ref = Ca_element
FEATURE [App::DocumentObjectGroupPython] O_element022  label="O_element : 010"  # scripted group (container) (typed FeaturePython)
  n = 1
  ref = O_element
FEATURE [App::DocumentObjectGroupPython] G4_CALCIUM_OXIDE  # scripted group (container) (typed FeaturePython)
  Dunit = g/cm3
  Dvalue = 3.3
  Group = -> [Ca_element007,O_element022]
  conduct = 2
  density = 1
  expand = 3
  formula = G4_CALCIUM_OXIDE
  name = G4_CALCIUM_OXIDE
  specific = 4
FEATURE [App::DocumentObjectGroupPython] Ca_element008  label="Ca_element : 004"  # scripted group (container) (typed FeaturePython)
  n = 1
  ref = Ca_element
FEATURE [App::DocumentObjectGroupPython] S_element007  label="S_element : 002"  # scripted group (container) (typed FeaturePython)
  n = 1
  ref = S_element
FEATURE [App::DocumentObjectGroupPython] O_element023  label="O_element : 011"  # scripted group (container) (typed FeaturePython)
  n = 4
  ref = O_element
FEATURE [App::DocumentObjectGroupPython] G4_CALCIUM_SULFATE  # scripted group (container) (typed FeaturePython)
  Dunit = g/cm3
  Dvalue = 2.96
  Group = -> [Ca_element008,S_element007,O_element023]
  conduct = 2
  density = 1
  expand = 3
  formula = G4_CALCIUM_SULFATE
  name = G4_CALCIUM_SULFATE
  specific = 4
FEATURE [App::DocumentObjectGroupPython] Ca_element009  label="Ca_element : 005"  # scripted group (container) (typed FeaturePython)
  n = 1
  ref = Ca_element
FEATURE [App::DocumentObjectGroupPython] W_element002  label="W_element : 002"  # scripted group (container) (typed FeaturePython)
  n = 1
  ref = W_element
FEATURE [App::DocumentObjectGroupPython] O_element024  label="O_element : 012"  # scripted group (container) (typed FeaturePython)
  n = 4
  ref = O_element
FEATURE [App::DocumentObjectGroupPython] G4_CALCIUM_TUNGSTATE  # scripted group (container) (typed FeaturePython)
  Dunit = g/cm3
  Dvalue = 6.062
  Group = -> [Ca_element009,W_element002,O_element024]
  conduct = 2
  density = 1
  expand = 3
  formula = G4_CALCIUM_TUNGSTATE
  name = G4_CALCIUM_TUNGSTATE
  specific = 4
FEATURE [App::DocumentObjectGroupPython] C_element023  label="C_element : 010"  # scripted group (container) (typed FeaturePython)
  n = 1
  ref = C_element
FEATURE [App::DocumentObjectGroupPython] O_element025  label="O_element : 013"  # scripted group (container) (typed FeaturePython)
  n = 2
  ref = O_element
FEATURE [App::DocumentObjectGroupPython] G4_CARBON_DIOXIDE  # scripted group (container) (typed FeaturePython)
  Dunit = g/cm3
  Dvalue = 0.00184212
  Group = -> [C_element023,O_element025]
  conduct = 2
  density = 1
  expand = 3
  formula = G4_CARBON_DIOXIDE
  name = G4_CARBON_DIOXIDE
  specific = 4
FEATURE [App::DocumentObjectGroupPython] C_element024  label="C_element : 011"  # scripted group (container) (typed FeaturePython)
  n = 1
  ref = C_element
FEATURE [App::DocumentObjectGroupPython] Cl_element004  label="Cl_element : 4"  # scripted group (container) (typed FeaturePython)
  n = 4
  ref = Cl_element
FEATURE [App::DocumentObjectGroupPython] G4_CARBON_TETRACHLORIDE  # scripted group (container) (typed FeaturePython)
  Dunit = g/cm3
  Dvalue = 1.594
  Group = -> [C_element024,Cl_element004]
  conduct = 2
  density = 1
  expand = 3
  formula = G4_CARBON_TETRACHLORIDE
  name = G4_CARBON_TETRACHLORIDE
  specific = 4
FEATURE [App::DocumentObjectGroupPython] C_element025  label="C_element : 012"  # scripted group (container) (typed FeaturePython)
  n = 6
  ref = C_element
FEATURE [App::DocumentObjectGroupPython] H_element021  label="H_element : 012"  # scripted group (container) (typed FeaturePython)
  n = 10
  ref = H_element
FEATURE [App::DocumentObjectGroupPython] O_element026  label="O_element : 5"  # scripted group (container) (typed FeaturePython)
  n = 5
  ref = O_element
FEATURE [App::DocumentObjectGroupPython] G4_CELLULOSE_CELLOPHANE  # scripted group (container) (typed FeaturePython)
  Dunit = g/cm3
  Dvalue = 1.42
  Group = -> [C_element025,H_element021,O_element026]
  conduct = 2
  density = 1
  expand = 3
  formula = G4_CELLULOSE_CELLOPHANE
  name = G4_CELLULOSE_CELLOPHANE
  specific = 4
FEATURE [App::DocumentObjectGroupPython] H_element022  label="H_element : 0.067"  # scripted group (container) (typed FeaturePython)
  n = 0.067125
FEATURE [App::DocumentObjectGroupPython] C_element026  label="C_element : 0.545"  # scripted group (container) (typed FeaturePython)
  n = 0.545403
FEATURE [App::DocumentObjectGroupPython] O_element027  label="O_element : 0.387"  # scripted group (container) (typed FeaturePython)
  n = 0.387472
FEATURE [App::DocumentObjectGroupPython] G4_CELLULOSE_BUTYRATE  # scripted group (container) (typed FeaturePython)
  Dunit = g/cm3
  Dvalue = 1.2
  Group = -> [H_element022,C_element026,O_element027]
  conduct = 2
  density = 1
  expand = 3
  formula = G4_CELLULOSE_BUTYRATE
  name = G4_CELLULOSE_BUTYRATE
  specific = 4
FEATURE [App::DocumentObjectGroupPython] H_element023  label="H_element : 0.029"  # scripted group (container) (typed FeaturePython)
  n = 0.029216
FEATURE [App::DocumentObjectGroupPython] C_element027  label="C_element : 0.271"  # scripted group (container) (typed FeaturePython)
  n = 0.271296
FEATURE [App::DocumentObjectGroupPython] N_element013  label="N_element : 0.121"  # scripted group (container) (typed FeaturePython)
  n = 0.121276
FEATURE [App::DocumentObjectGroupPython] O_element028  label="O_element : 0.578"  # scripted group (container) (typed FeaturePython)
  n = 0.578212
FEATURE [App::DocumentObjectGroupPython] G4_CELLULOSE_NITRATE  # scripted group (container) (typed FeaturePython)
  Dunit = g/cm3
  Dvalue = 1.49
  Group = -> [H_element023,C_element027,N_element013,O_element028]
  conduct = 2
  density = 1
  expand = 3
  formula = G4_CELLULOSE_NITRATE
  name = G4_CELLULOSE_NITRATE
  specific = 4
FEATURE [App::DocumentObjectGroupPython] H_element024  label="H_element : 0.108"  # scripted group (container) (typed FeaturePython)
  n = 0.107596
FEATURE [App::DocumentObjectGroupPython] N_element014  label="N_element : 0.001"  # scripted group (container) (typed FeaturePython)
  n = 0.0008
FEATURE [App::DocumentObjectGroupPython] O_element029  label="O_element : 0.875"  # scripted group (container) (typed FeaturePython)
  n = 0.874976
FEATURE [App::DocumentObjectGroupPython] S_element008  label="S_element : 0.015"  # scripted group (container) (typed FeaturePython)
  n = 0.014627
FEATURE [App::DocumentObjectGroupPython] Ce_element001  label="Ce_element : 0.002"  # scripted group (container) (typed FeaturePython)
  n = 0.002001
FEATURE [App::DocumentObjectGroupPython] G4_CERIC_SULFATE  # scripted group (container) (typed FeaturePython)
  Dunit = g/cm3
  Dvalue = 1.03
  Group = -> [H_element024,N_element014,O_element029,S_element008,Ce_element001]
  conduct = 2
  density = 1
  expand = 3
  formula = G4_CERIC_SULFATE
  name = G4_CERIC_SULFATE
  specific = 4
FEATURE [App::DocumentObjectGroupPython] Cs_element001  label="Cs_element : 1"  # scripted group (container) (typed FeaturePython)
  n = 1
  ref = Cs_element
FEATURE [App::DocumentObjectGroupPython] F_element006  label="F_element : 1"  # scripted group (container) (typed FeaturePython)
  n = 1
  ref = F_element
FEATURE [App::DocumentObjectGroupPython] G4_CESIUM_FLUORIDE  # scripted group (container) (typed FeaturePython)
  Dunit = g/cm3
  Dvalue = 4.115
  Group = -> [Cs_element001,F_element006]
  conduct = 2
  density = 1
  expand = 3
  formula = G4_CESIUM_FLUORIDE
  name = G4_CESIUM_FLUORIDE
  specific = 4
FEATURE [App::DocumentObjectGroupPython] Cs_element002  label="Cs_element : 002"  # scripted group (container) (typed FeaturePython)
  n = 1
  ref = Cs_element
FEATURE [App::DocumentObjectGroupPython] I_element001  label="I_element : 1"  # scripted group (container) (typed FeaturePython)
  n = 1
  ref = I_element
FEATURE [App::DocumentObjectGroupPython] G4_CESIUM_IODIDE  # scripted group (container) (typed FeaturePython)
  Dunit = g/cm3
  Dvalue = 4.51
  Group = -> [Cs_element002,I_element001]
  conduct = 2
  density = 1
  expand = 3
  formula = G4_CESIUM_IODIDE
  name = G4_CESIUM_IODIDE
  specific = 4
FEATURE [App::DocumentObjectGroupPython] C_element028  label="C_element : 013"  # scripted group (container) (typed FeaturePython)
  n = 6
  ref = C_element
FEATURE [App::DocumentObjectGroupPython] H_element025  label="H_element : 013"  # scripted group (container) (typed FeaturePython)
  n = 5
  ref = H_element
FEATURE [App::DocumentObjectGroupPython] Cl_element005  label="Cl_element : 1"  # scripted group (container) (typed FeaturePython)
  n = 1
  ref = Cl_element
FEATURE [App::DocumentObjectGroupPython] G4_CHLOROBENZENE  # scripted group (container) (typed FeaturePython)
  Dunit = g/cm3
  Dvalue = 1.1058
  Group = -> [C_element028,H_element025,Cl_element005]
  conduct = 2
  density = 1
  expand = 3
  formula = G4_CHLOROBENZENE
  name = G4_CHLOROBENZENE
  specific = 4
FEATURE [App::DocumentObjectGroupPython] C_element029  label="C_element : 014"  # scripted group (container) (typed FeaturePython)
  n = 1
  ref = C_element
FEATURE [App::DocumentObjectGroupPython] H_element026  label="H_element : 1"  # scripted group (container) (typed FeaturePython)
  n = 1
  ref = H_element
FEATURE [App::DocumentObjectGroupPython] Cl_element006  label="Cl_element : 3"  # scripted group (container) (typed FeaturePython)
  n = 3
  ref = Cl_element
FEATURE [App::DocumentObjectGroupPython] G4_CHLOROFORM  # scripted group (container) (typed FeaturePython)
  Dunit = g/cm3
  Dvalue = 1.4832
  Group = -> [C_element029,H_element026,Cl_element006]
  conduct = 2
  density = 1
  expand = 3
  formula = G4_CHLOROFORM
  name = G4_CHLOROFORM
  specific = 4
FEATURE [App::DocumentObjectGroupPython] H_element027  label="H_element : 0.010"  # scripted group (container) (typed FeaturePython)
  n = 0.01
FEATURE [App::DocumentObjectGroupPython] C_element030  label="C_element : 0.001"  # scripted group (container) (typed FeaturePython)
  n = 0.001
FEATURE [App::DocumentObjectGroupPython] O_element030  label="O_element : 0.529"  # scripted group (container) (typed FeaturePython)
  n = 0.529107
FEATURE [App::DocumentObjectGroupPython] Na_element005  label="Na_element : 0.016"  # scripted group (container) (typed FeaturePython)
  n = 0.016
FEATURE [App::DocumentObjectGroupPython] Mg_element003  label="Mg_element : 0.004"  # scripted group (container) (typed FeaturePython)
  n = 0.002
FEATURE [App::DocumentObjectGroupPython] Al_element002  label="Al_element : 0.034"  # scripted group (container) (typed FeaturePython)
  n = 0.033872
FEATURE [App::DocumentObjectGroupPython] Si_element002  label="Si_element : 0.337"  # scripted group (container) (typed FeaturePython)
  n = 0.337021
FEATURE [App::DocumentObjectGroupPython] K_element003  label="K_element : 0.013"  # scripted group (container) (typed FeaturePython)
  n = 0.013
FEATURE [App::DocumentObjectGroupPython] Ca_element010  label="Ca_element : 0.044"  # scripted group (container) (typed FeaturePython)
  n = 0.044
FEATURE [App::DocumentObjectGroupPython] Fe_element002  label="Fe_element : 0.014"  # scripted group (container) (typed FeaturePython)
  n = 0.014
FEATURE [App::DocumentObjectGroupPython] G4_CONCRETE  # scripted group (container) (typed FeaturePython)
  Dunit = g/cm3
  Dvalue = 2.3
  Group = -> [H_element027,C_element030,O_element030,Na_element005,Mg_element003,Al_element002,Si_element002,K_element003,Ca_element010,Fe_element002]
  conduct = 2
  density = 1
  expand = 3
  formula = G4_CONCRETE
  name = G4_CONCRETE
  specific = 4
FEATURE [App::DocumentObjectGroupPython] C_element031  label="C_element : 015"  # scripted group (container) (typed FeaturePython)
  n = 6
  ref = C_element
FEATURE [App::DocumentObjectGroupPython] H_element028  label="H_element : 12"  # scripted group (container) (typed FeaturePython)
  n = 12
  ref = H_element
FEATURE [App::DocumentObjectGroupPython] G4_CYCLOHEXANE  # scripted group (container) (typed FeaturePython)
  Dunit = g/cm3
  Dvalue = 0.779
  Group = -> [C_element031,H_element028]
  conduct = 2
  density = 1
  expand = 3
  formula = G4_CYCLOHEXANE
  name = G4_CYCLOHEXANE
  specific = 4
FEATURE [App::DocumentObjectGroupPython] C_element032  label="C_element : 016"  # scripted group (container) (typed FeaturePython)
  n = 6
  ref = C_element
FEATURE [App::DocumentObjectGroupPython] H_element029  label="H_element : 4"  # scripted group (container) (typed FeaturePython)
  n = 4
  ref = H_element
FEATURE [App::DocumentObjectGroupPython] Cl_element007  label="Cl_element : 2"  # scripted group (container) (typed FeaturePython)
  n = 2
  ref = Cl_element
FEATURE [App::DocumentObjectGroupPython] G4_1_2_DICHLOROBENZENE  label="G4_1.2-DICHLOROBENZENE"  # scripted group (container) (typed FeaturePython)
  Dunit = g/cm3
  Dvalue = 1.3048
  Group = -> [C_element032,H_element029,Cl_element007]
  conduct = 2
  density = 1
  expand = 3
  formula = G4_1.2-DICHLOROBENZENE
  name = G4_1.2-DICHLOROBENZENE
  specific = 4
FEATURE [App::DocumentObjectGroupPython] C_element033  label="C_element : 017"  # scripted group (container) (typed FeaturePython)
  n = 4
  ref = C_element
FEATURE [App::DocumentObjectGroupPython] H_element030  label="H_element : 8"  # scripted group (container) (typed FeaturePython)
  n = 8
  ref = H_element
FEATURE [App::DocumentObjectGroupPython] O_element031  label="O_element : 014"  # scripted group (container) (typed FeaturePython)
  n = 1
  ref = O_element
FEATURE [App::DocumentObjectGroupPython] Cl_element008  label="Cl_element : 005"  # scripted group (container) (typed FeaturePython)
  n = 2
  ref = Cl_element
FEATURE [App::DocumentObjectGroupPython] G4_DICHLORODIETHYL_ETHER  # scripted group (container) (typed FeaturePython)
  Dunit = g/cm3
  Dvalue = 1.2199
  Group = -> [C_element033,H_element030,O_element031,Cl_element008]
  conduct = 2
  density = 1
  expand = 3
  formula = G4_DICHLORODIETHYL_ETHER
  name = G4_DICHLORODIETHYL_ETHER
  specific = 4
FEATURE [App::DocumentObjectGroupPython] C_element034  label="C_element : 018"  # scripted group (container) (typed FeaturePython)
  n = 2
  ref = C_element
FEATURE [App::DocumentObjectGroupPython] H_element031  label="H_element : 014"  # scripted group (container) (typed FeaturePython)
  n = 4
  ref = H_element
FEATURE [App::DocumentObjectGroupPython] Cl_element009  label="Cl_element : 006"  # scripted group (container) (typed FeaturePython)
  n = 2
  ref = Cl_element
FEATURE [App::DocumentObjectGroupPython] G4_1_2_DICHLOROETHANE  label="G4_1.2-DICHLOROETHANE"  # scripted group (container) (typed FeaturePython)
  Dunit = g/cm3
  Dvalue = 1.2351
  Group = -> [C_element034,H_element031,Cl_element009]
  conduct = 2
  density = 1
  expand = 3
  formula = G4_1.2-DICHLOROETHANE
  name = G4_1.2-DICHLOROETHANE
  specific = 4
FEATURE [App::DocumentObjectGroupPython] C_element035  label="C_element : 019"  # scripted group (container) (typed FeaturePython)
  n = 4
  ref = C_element
FEATURE [App::DocumentObjectGroupPython] H_element032  label="H_element : 015"  # scripted group (container) (typed FeaturePython)
  n = 10
  ref = H_element
FEATURE [App::DocumentObjectGroupPython] O_element032  label="O_element : 015"  # scripted group (container) (typed FeaturePython)
  n = 1
  ref = O_element
FEATURE [App::DocumentObjectGroupPython] G4_DIETHYL_ETHER  # scripted group (container) (typed FeaturePython)
  Dunit = g/cm3
  Dvalue = 0.71378
  Group = -> [C_element035,H_element032,O_element032]
  conduct = 2
  density = 1
  expand = 3
  formula = G4_DIETHYL_ETHER
  name = G4_DIETHYL_ETHER
  specific = 4
FEATURE [App::DocumentObjectGroupPython] C_element036  label="C_element : 020"  # scripted group (container) (typed FeaturePython)
  n = 3
  ref = C_element
FEATURE [App::DocumentObjectGroupPython] H_element033  label="H_element : 016"  # scripted group (container) (typed FeaturePython)
  n = 7
  ref = H_element
FEATURE [App::DocumentObjectGroupPython] N_element015  label="N_element : 008"  # scripted group (container) (typed FeaturePython)
  n = 1
  ref = N_element
FEATURE [App::DocumentObjectGroupPython] O_element033  label="O_element : 016"  # scripted group (container) (typed FeaturePython)
  n = 1
  ref = O_element
FEATURE [App::DocumentObjectGroupPython] G4_N_N_DIMETHYL_FORMAMIDE  label="G4_N.N-DIMETHYL_FORMAMIDE"  # scripted group (container) (typed FeaturePython)
  Dunit = g/cm3
  Dvalue = 0.9487
  Group = -> [C_element036,H_element033,N_element015,O_element033]
  conduct = 2
  density = 1
  expand = 3
  formula = G4_N.N-DIMETHYL_FORMAMIDE
  name = G4_N.N-DIMETHYL_FORMAMIDE
  specific = 4
FEATURE [App::DocumentObjectGroupPython] C_element037  label="C_element : 021"  # scripted group (container) (typed FeaturePython)
  n = 2
  ref = C_element
FEATURE [App::DocumentObjectGroupPython] H_element034  label="H_element : 017"  # scripted group (container) (typed FeaturePython)
  n = 6
  ref = H_element
FEATURE [App::DocumentObjectGroupPython] O_element034  label="O_element : 017"  # scripted group (container) (typed FeaturePython)
  n = 1
  ref = O_element
FEATURE [App::DocumentObjectGroupPython] S_element009  label="S_element : 003"  # scripted group (container) (typed FeaturePython)
  n = 1
  ref = S_element
FEATURE [App::DocumentObjectGroupPython] G4_DIMETHYL_SULFOXIDE  # scripted group (container) (typed FeaturePython)
  Dunit = g/cm3
  Dvalue = 1.1014
  Group = -> [C_element037,H_element034,O_element034,S_element009]
  conduct = 2
  density = 1
  expand = 3
  formula = G4_DIMETHYL_SULFOXIDE
  name = G4_DIMETHYL_SULFOXIDE
  specific = 4
FEATURE [App::DocumentObjectGroupPython] C_element038  label="C_element : 022"  # scripted group (container) (typed FeaturePython)
  n = 2
  ref = C_element
FEATURE [App::DocumentObjectGroupPython] H_element035  label="H_element : 018"  # scripted group (container) (typed FeaturePython)
  n = 6
  ref = H_element
FEATURE [App::DocumentObjectGroupPython] G4_ETHANE  # scripted group (container) (typed FeaturePython)
  Dunit = g/cm3
  Dvalue = 0.00125324
  Group = -> [C_element038,H_element035]
  conduct = 2
  density = 1
  expand = 3
  formula = G4_ETHANE
  name = G4_ETHANE
  specific = 4
FEATURE [App::DocumentObjectGroupPython] C_element039  label="C_element : 023"  # scripted group (container) (typed FeaturePython)
  n = 2
  ref = C_element
FEATURE [App::DocumentObjectGroupPython] H_element036  label="H_element : 019"  # scripted group (container) (typed FeaturePython)
  n = 6
  ref = H_element
FEATURE [App::DocumentObjectGroupPython] O_element035  label="O_element : 018"  # scripted group (container) (typed FeaturePython)
  n = 1
  ref = O_element
FEATURE [App::DocumentObjectGroupPython] G4_ETHYL_ALCOHOL  # scripted group (container) (typed FeaturePython)
  Dunit = g/cm3
  Dvalue = 0.7893
  Group = -> [C_element039,H_element036,O_element035]
  conduct = 2
  density = 1
  expand = 3
  formula = G4_ETHYL_ALCOHOL
  name = G4_ETHYL_ALCOHOL
  specific = 4
FEATURE [App::DocumentObjectGroupPython] H_element037  label="H_element : 0.090"  # scripted group (container) (typed FeaturePython)
  n = 0.090027
FEATURE [App::DocumentObjectGroupPython] C_element040  label="C_element : 0.585"  # scripted group (container) (typed FeaturePython)
  n = 0.585182
FEATURE [App::DocumentObjectGroupPython] O_element036  label="O_element : 0.325"  # scripted group (container) (typed FeaturePython)
  n = 0.324791
FEATURE [App::DocumentObjectGroupPython] G4_ETHYL_CELLULOSE  # scripted group (container) (typed FeaturePython)
  Dunit = g/cm3
  Dvalue = 1.13
  Group = -> [H_element037,C_element040,O_element036]
  conduct = 2
  density = 1
  expand = 3
  formula = G4_ETHYL_CELLULOSE
  name = G4_ETHYL_CELLULOSE
  specific = 4
FEATURE [App::DocumentObjectGroupPython] C_element041  label="C_element : 024"  # scripted group (container) (typed FeaturePython)
  n = 2
  ref = C_element
FEATURE [App::DocumentObjectGroupPython] H_element038  label="H_element : 020"  # scripted group (container) (typed FeaturePython)
  n = 4
  ref = H_element
FEATURE [App::DocumentObjectGroupPython] G4_ETHYLENE  # scripted group (container) (typed FeaturePython)
  Dunit = g/cm3
  Dvalue = 0.00117497
  Group = -> [C_element041,H_element038]
  conduct = 2
  density = 1
  expand = 3
  formula = G4_ETHYLENE
  name = G4_ETHYLENE
  specific = 4
FEATURE [App::DocumentObjectGroupPython] H_element039  label="H_element : 0.096"  # scripted group (container) (typed FeaturePython)
  n = 0.096
FEATURE [App::DocumentObjectGroupPython] C_element042  label="C_element : 0.195"  # scripted group (container) (typed FeaturePython)
  n = 0.195
FEATURE [App::DocumentObjectGroupPython] N_element016  label="N_element : 0.057"  # scripted group (container) (typed FeaturePython)
  n = 0.057
FEATURE [App::DocumentObjectGroupPython] O_element037  label="O_element : 0.646"  # scripted group (container) (typed FeaturePython)
  n = 0.646
FEATURE [App::DocumentObjectGroupPython] Na_element006  label="Na_element : 0.017"  # scripted group (container) (typed FeaturePython)
  n = 0.001
FEATURE [App::DocumentObjectGroupPython] P_element005  label="P_element : 0.104"  # scripted group (container) (typed FeaturePython)
  n = 0.001
FEATURE [App::DocumentObjectGroupPython] S_element010  label="S_element : 0.016"  # scripted group (container) (typed FeaturePython)
  n = 0.003
FEATURE [App::DocumentObjectGroupPython] Cl_element010  label="Cl_element : 0.005"  # scripted group (container) (typed FeaturePython)
  n = 0.001
FEATURE [App::DocumentObjectGroupPython] G4_EYE_LENS_ICRP  # scripted group (container) (typed FeaturePython)
  Dunit = g/cm3
  Dvalue = 1.07
  Group = -> [H_element039,C_element042,N_element016,O_element037,Na_element006,P_element005,S_element010,Cl_element010]
  conduct = 2
  density = 1
  expand = 3
  formula = G4_EYE_LENS_ICRP
  name = G4_EYE_LENS_ICRP
  specific = 4
FEATURE [App::DocumentObjectGroupPython] Fe_element003  label="Fe_element : 2"  # scripted group (container) (typed FeaturePython)
  n = 2
  ref = Fe_element
FEATURE [App::DocumentObjectGroupPython] O_element038  label="O_element : 019"  # scripted group (container) (typed FeaturePython)
  n = 3
  ref = O_element
FEATURE [App::DocumentObjectGroupPython] G4_FERRIC_OXIDE  # scripted group (container) (typed FeaturePython)
  Dunit = g/cm3
  Dvalue = 5.2
  Group = -> [Fe_element003,O_element038]
  conduct = 2
  density = 1
  expand = 3
  formula = G4_FERRIC_OXIDE
  name = G4_FERRIC_OXIDE
  specific = 4
FEATURE [App::DocumentObjectGroupPython] Fe_element004  label="Fe_element : 1"  # scripted group (container) (typed FeaturePython)
  n = 1
  ref = Fe_element
FEATURE [App::DocumentObjectGroupPython] B_element003  label="B_element : 1"  # scripted group (container) (typed FeaturePython)
  n = 1
  ref = B_element
FEATURE [App::DocumentObjectGroupPython] G4_FERROBORIDE  # scripted group (container) (typed FeaturePython)
  Dunit = g/cm3
  Dvalue = 7.15
  Group = -> [Fe_element004,B_element003]
  conduct = 2
  density = 1
  expand = 3
  formula = G4_FERROBORIDE
  name = G4_FERROBORIDE
  specific = 4
FEATURE [App::DocumentObjectGroupPython] Fe_element005  label="Fe_element : 003"  # scripted group (container) (typed FeaturePython)
  n = 1
  ref = Fe_element
FEATURE [App::DocumentObjectGroupPython] O_element039  label="O_element : 020"  # scripted group (container) (typed FeaturePython)
  n = 1
  ref = O_element
FEATURE [App::DocumentObjectGroupPython] G4_FERROUS_OXIDE  # scripted group (container) (typed FeaturePython)
  Dunit = g/cm3
  Dvalue = 5.7
  Group = -> [Fe_element005,O_element039]
  conduct = 2
  density = 1
  expand = 3
  formula = G4_FERROUS_OXIDE
  name = G4_FERROUS_OXIDE
  specific = 4
FEATURE [App::DocumentObjectGroupPython] H_element040  label="H_element : 0.115"  # scripted group (container) (typed FeaturePython)
  n = 0.108259
FEATURE [App::DocumentObjectGroupPython] N_element017  label="N_element : 0.000"  # scripted group (container) (typed FeaturePython)
  n = 2.7e-05
FEATURE [App::DocumentObjectGroupPython] O_element040  label="O_element : 0.879"  # scripted group (container) (typed FeaturePython)
  n = 0.878636
FEATURE [App::DocumentObjectGroupPython] Na_element007  label="Na_element : 0.000"  # scripted group (container) (typed FeaturePython)
  n = 2.2e-05
FEATURE [App::DocumentObjectGroupPython] S_element011  label="S_element : 0.013"  # scripted group (container) (typed FeaturePython)
  n = 0.012968
FEATURE [App::DocumentObjectGroupPython] Cl_element011  label="Cl_element : 0.000"  # scripted group (container) (typed FeaturePython)
  n = 3.4e-05
FEATURE [App::DocumentObjectGroupPython] Fe_element006  label="Fe_element : 0.000"  # scripted group (container) (typed FeaturePython)
  n = 5.4e-05
FEATURE [App::DocumentObjectGroupPython] G4_FERROUS_SULFATE  # scripted group (container) (typed FeaturePython)
  Dunit = g/cm3
  Dvalue = 1.024
  Group = -> [H_element040,N_element017,O_element040,Na_element007,S_element011,Cl_element011,Fe_element006]
  conduct = 2
  density = 1
  expand = 3
  formula = G4_FERROUS_SULFATE
  name = G4_FERROUS_SULFATE
  specific = 4
FEATURE [App::DocumentObjectGroupPython] C_element043  label="C_element : 0.099"  # scripted group (container) (typed FeaturePython)
  n = 0.099335
FEATURE [App::DocumentObjectGroupPython] F_element007  label="F_element : 0.314"  # scripted group (container) (typed FeaturePython)
  n = 0.314247
FEATURE [App::DocumentObjectGroupPython] Cl_element012  label="Cl_element : 0.586"  # scripted group (container) (typed FeaturePython)
  n = 0.586418
FEATURE [App::DocumentObjectGroupPython] G4_FREON_12  label="G4_FREON-12"  # scripted group (container) (typed FeaturePython)
  Dunit = g/cm3
  Dvalue = 1.12
  Group = -> [C_element043,F_element007,Cl_element012]
  conduct = 2
  density = 1
  expand = 3
  formula = G4_FREON-12
  name = G4_FREON-12
  specific = 4
FEATURE [App::DocumentObjectGroupPython] C_element044  label="C_element : 0.057"  # scripted group (container) (typed FeaturePython)
  n = 0.057245
FEATURE [App::DocumentObjectGroupPython] F_element008  label="F_element : 0.181"  # scripted group (container) (typed FeaturePython)
  n = 0.181096
FEATURE [App::DocumentObjectGroupPython] Br_element001  label="Br_element : 0.762"  # scripted group (container) (typed FeaturePython)
  n = 0.761659
FEATURE [App::DocumentObjectGroupPython] G4_FREON_12B2  label="G4_FREON-12B2"  # scripted group (container) (typed FeaturePython)
  Dunit = g/cm3
  Dvalue = 1.8
  Group = -> [C_element044,F_element008,Br_element001]
  conduct = 2
  density = 1
  expand = 3
  formula = G4_FREON-12B2
  name = G4_FREON-12B2
  specific = 4
FEATURE [App::DocumentObjectGroupPython] C_element045  label="C_element : 0.115"  # scripted group (container) (typed FeaturePython)
  n = 0.114983
FEATURE [App::DocumentObjectGroupPython] F_element009  label="F_element : 0.546"  # scripted group (container) (typed FeaturePython)
  n = 0.545621
FEATURE [App::DocumentObjectGroupPython] Cl_element013  label="Cl_element : 0.339"  # scripted group (container) (typed FeaturePython)
  n = 0.339396
FEATURE [App::DocumentObjectGroupPython] G4_FREON_13  label="G4_FREON-13"  # scripted group (container) (typed FeaturePython)
  Dunit = g/cm3
  Dvalue = 0.95
  Group = -> [C_element045,F_element009,Cl_element013]
  conduct = 2
  density = 1
  expand = 3
  formula = G4_FREON-13
  name = G4_FREON-13
  specific = 4
FEATURE [App::DocumentObjectGroupPython] C_element046  label="C_element : 025"  # scripted group (container) (typed FeaturePython)
  n = 1
  ref = C_element
FEATURE [App::DocumentObjectGroupPython] F_element010  label="F_element : 3"  # scripted group (container) (typed FeaturePython)
  n = 3
  ref = F_element
FEATURE [App::DocumentObjectGroupPython] Br_element002  label="Br_element : 1"  # scripted group (container) (typed FeaturePython)
  n = 1
  ref = Br_element
FEATURE [App::DocumentObjectGroupPython] G4_FREON_13B1  label="G4_FREON-13B1"  # scripted group (container) (typed FeaturePython)
  Dunit = g/cm3
  Dvalue = 1.5
  Group = -> [C_element046,F_element010,Br_element002]
  conduct = 2
  density = 1
  expand = 3
  formula = G4_FREON-13B1
  name = G4_FREON-13B1
  specific = 4
FEATURE [App::DocumentObjectGroupPython] C_element047  label="C_element : 0.061"  # scripted group (container) (typed FeaturePython)
  n = 0.061309
FEATURE [App::DocumentObjectGroupPython] F_element011  label="F_element : 0.291"  # scripted group (container) (typed FeaturePython)
  n = 0.290924
FEATURE [App::DocumentObjectGroupPython] I_element002  label="I_element : 0.648"  # scripted group (container) (typed FeaturePython)
  n = 0.647767
FEATURE [App::DocumentObjectGroupPython] G4_FREON_13I1  label="G4_FREON-13I1"  # scripted group (container) (typed FeaturePython)
  Dunit = g/cm3
  Dvalue = 1.8
  Group = -> [C_element047,F_element011,I_element002]
  conduct = 2
  density = 1
  expand = 3
  formula = G4_FREON-13I1
  name = G4_FREON-13I1
  specific = 4
FEATURE [App::DocumentObjectGroupPython] Gd_element001  label="Gd_element : 2"  # scripted group (container) (typed FeaturePython)
  n = 2
  ref = Gd_element
FEATURE [App::DocumentObjectGroupPython] O_element041  label="O_element : 021"  # scripted group (container) (typed FeaturePython)
  n = 2
  ref = O_element
FEATURE [App::DocumentObjectGroupPython] S_element012  label="S_element : 004"  # scripted group (container) (typed FeaturePython)
  n = 1
  ref = S_element
FEATURE [App::DocumentObjectGroupPython] G4_GADOLINIUM_OXYSULFIDE  # scripted group (container) (typed FeaturePython)
  Dunit = g/cm3
  Dvalue = 7.44
  Group = -> [Gd_element001,O_element041,S_element012]
  conduct = 2
  density = 1
  expand = 3
  formula = G4_GADOLINIUM_OXYSULFIDE
  name = G4_GADOLINIUM_OXYSULFIDE
  specific = 4
FEATURE [App::DocumentObjectGroupPython] Ga_element001  label="Ga_element : 1"  # scripted group (container) (typed FeaturePython)
  n = 1
  ref = Ga_element
FEATURE [App::DocumentObjectGroupPython] As_element001  label="As_element : 1"  # scripted group (container) (typed FeaturePython)
  n = 1
  ref = As_element
FEATURE [App::DocumentObjectGroupPython] G4_GALLIUM_ARSENIDE  # scripted group (container) (typed FeaturePython)
  Dunit = g/cm3
  Dvalue = 5.31
  Group = -> [Ga_element001,As_element001]
  conduct = 2
  density = 1
  expand = 3
  formula = G4_GALLIUM_ARSENIDE
  name = G4_GALLIUM_ARSENIDE
  specific = 4
FEATURE [App::DocumentObjectGroupPython] H_element041  label="H_element : 0.081"  # scripted group (container) (typed FeaturePython)
  n = 0.08118
FEATURE [App::DocumentObjectGroupPython] C_element048  label="C_element : 0.416"  # scripted group (container) (typed FeaturePython)
  n = 0.41606
FEATURE [App::DocumentObjectGroupPython] N_element018  label="N_element : 0.111"  # scripted group (container) (typed FeaturePython)
  n = 0.11124
FEATURE [App::DocumentObjectGroupPython] O_element042  label="O_element : 0.381"  # scripted group (container) (typed FeaturePython)
  n = 0.38064
FEATURE [App::DocumentObjectGroupPython] S_element013  label="S_element : 0.011"  # scripted group (container) (typed FeaturePython)
  n = 0.01088
FEATURE [App::DocumentObjectGroupPython] G4_GEL_PHOTO_EMULSION  # scripted group (container) (typed FeaturePython)
  Dunit = g/cm3
  Dvalue = 1.2914
  Group = -> [H_element041,C_element048,N_element018,O_element042,S_element013]
  conduct = 2
  density = 1
  expand = 3
  formula = G4_GEL_PHOTO_EMULSION
  name = G4_GEL_PHOTO_EMULSION
  specific = 4
FEATURE [App::DocumentObjectGroupPython] B_element004  label="B_element : 0.040"  # scripted group (container) (typed FeaturePython)
  n = 0.0400639
FEATURE [App::DocumentObjectGroupPython] O_element043  label="O_element : 0.540"  # scripted group (container) (typed FeaturePython)
  n = 0.539561
FEATURE [App::DocumentObjectGroupPython] Na_element008  label="Na_element : 0.028"  # scripted group (container) (typed FeaturePython)
  n = 0.0281909
FEATURE [App::DocumentObjectGroupPython] Al_element003  label="Al_element : 0.012"  # scripted group (container) (typed FeaturePython)
  n = 0.011644
FEATURE [App::DocumentObjectGroupPython] Si_element003  label="Si_element : 0.377"  # scripted group (container) (typed FeaturePython)
  n = 0.377219
FEATURE [App::DocumentObjectGroupPython] K_element004  label="K_element : 0.014"  # scripted group (container) (typed FeaturePython)
  n = 0.00332099
FEATURE [App::DocumentObjectGroupPython] G4_Pyrex_Glass  # scripted group (container) (typed FeaturePython)
  Dunit = g/cm3
  Dvalue = 2.23
  Group = -> [B_element004,O_element043,Na_element008,Al_element003,Si_element003,K_element004]
  conduct = 2
  density = 1
  expand = 3
  formula = G4_Pyrex_Glass
  name = G4_Pyrex_Glass
  specific = 4
FEATURE [App::DocumentObjectGroupPython] O_element044  label="O_element : 0.156"  # scripted group (container) (typed FeaturePython)
  n = 0.156453
FEATURE [App::DocumentObjectGroupPython] Si_element004  label="Si_element : 0.081"  # scripted group (container) (typed FeaturePython)
  n = 0.080866
FEATURE [App::DocumentObjectGroupPython] Ti_element001  label="Ti_element : 0.008"  # scripted group (container) (typed FeaturePython)
  n = 0.008092
FEATURE [App::DocumentObjectGroupPython] As_element002  label="As_element : 0.003"  # scripted group (container) (typed FeaturePython)
  n = 0.002651
FEATURE [App::DocumentObjectGroupPython] Pb_element001  label="Pb_element : 0.752"  # scripted group (container) (typed FeaturePython)
  n = 0.751938
FEATURE [App::DocumentObjectGroupPython] G4_GLASS_LEAD  # scripted group (container) (typed FeaturePython)
  Dunit = g/cm3
  Dvalue = 6.22
  Group = -> [O_element044,Si_element004,Ti_element001,As_element002,Pb_element001]
  conduct = 2
  density = 1
  expand = 3
  formula = G4_GLASS_LEAD
  name = G4_GLASS_LEAD
  specific = 4
FEATURE [App::DocumentObjectGroupPython] O_element045  label="O_element : 0.460"  # scripted group (container) (typed FeaturePython)
  n = 0.4598
FEATURE [App::DocumentObjectGroupPython] Na_element009  label="Na_element : 0.096"  # scripted group (container) (typed FeaturePython)
  n = 0.0964411
FEATURE [App::DocumentObjectGroupPython] Si_element005  label="Si_element : 0.378"  # scripted group (container) (typed FeaturePython)
  n = 0.336553
FEATURE [App::DocumentObjectGroupPython] Ca_element011  label="Ca_element : 0.107"  # scripted group (container) (typed FeaturePython)
  n = 0.107205
FEATURE [App::DocumentObjectGroupPython] G4_GLASS_PLATE  # scripted group (container) (typed FeaturePython)
  Dunit = g/cm3
  Dvalue = 2.4
  Group = -> [O_element045,Na_element009,Si_element005,Ca_element011]
  conduct = 2
  density = 1
  expand = 3
  formula = G4_GLASS_PLATE
  name = G4_GLASS_PLATE
  specific = 4
FEATURE [App::DocumentObjectGroupPython] C_element049  label="C_element : 026"  # scripted group (container) (typed FeaturePython)
  n = 5
  ref = C_element
FEATURE [App::DocumentObjectGroupPython] H_element042  label="H_element : 021"  # scripted group (container) (typed FeaturePython)
  n = 10
  ref = H_element
FEATURE [App::DocumentObjectGroupPython] N_element019  label="N_element : 2"  # scripted group (container) (typed FeaturePython)
  n = 2
  ref = N_element
FEATURE [App::DocumentObjectGroupPython] O_element046  label="O_element : 022"  # scripted group (container) (typed FeaturePython)
  n = 3
  ref = O_element
FEATURE [App::DocumentObjectGroupPython] G4_GLUTAMINE  # scripted group (container) (typed FeaturePython)
  Dunit = g/cm3
  Dvalue = 1.46
  Group = -> [C_element049,H_element042,N_element019,O_element046]
  conduct = 2
  density = 1
  expand = 3
  formula = G4_GLUTAMINE
  name = G4_GLUTAMINE
  specific = 4
FEATURE [App::DocumentObjectGroupPython] C_element050  label="C_element : 027"  # scripted group (container) (typed FeaturePython)
  n = 3
  ref = C_element
FEATURE [App::DocumentObjectGroupPython] H_element043  label="H_element : 022"  # scripted group (container) (typed FeaturePython)
  n = 8
  ref = H_element
FEATURE [App::DocumentObjectGroupPython] O_element047  label="O_element : 023"  # scripted group (container) (typed FeaturePython)
  n = 3
  ref = O_element
FEATURE [App::DocumentObjectGroupPython] G4_GLYCEROL  # scripted group (container) (typed FeaturePython)
  Dunit = g/cm3
  Dvalue = 1.2613
  Group = -> [C_element050,H_element043,O_element047]
  conduct = 2
  density = 1
  expand = 3
  formula = G4_GLYCEROL
  name = G4_GLYCEROL
  specific = 4
FEATURE [App::DocumentObjectGroupPython] C_element051  label="C_element : 028"  # scripted group (container) (typed FeaturePython)
  n = 5
  ref = C_element
FEATURE [App::DocumentObjectGroupPython] H_element044  label="H_element : 023"  # scripted group (container) (typed FeaturePython)
  n = 5
  ref = H_element
FEATURE [App::DocumentObjectGroupPython] N_element020  label="N_element : 009"  # scripted group (container) (typed FeaturePython)
  n = 5
  ref = N_element
FEATURE [App::DocumentObjectGroupPython] O_element048  label="O_element : 024"  # scripted group (container) (typed FeaturePython)
  n = 1
  ref = O_element
FEATURE [App::DocumentObjectGroupPython] G4_GUANINE  # scripted group (container) (typed FeaturePython)
  Dunit = g/cm3
  Dvalue = 2.2
  Group = -> [C_element051,H_element044,N_element020,O_element048]
  conduct = 2
  density = 1
  expand = 3
  formula = G4_GUANINE
  name = G4_GUANINE
  specific = 4
FEATURE [App::DocumentObjectGroupPython] Ca_element012  label="Ca_element : 006"  # scripted group (container) (typed FeaturePython)
  n = 1
  ref = Ca_element
FEATURE [App::DocumentObjectGroupPython] S_element014  label="S_element : 005"  # scripted group (container) (typed FeaturePython)
  n = 1
  ref = S_element
FEATURE [App::DocumentObjectGroupPython] O_element049  label="O_element : 6"  # scripted group (container) (typed FeaturePython)
  n = 6
  ref = O_element
FEATURE [App::DocumentObjectGroupPython] H_element045  label="H_element : 024"  # scripted group (container) (typed FeaturePython)
  n = 4
  ref = H_element
FEATURE [App::DocumentObjectGroupPython] G4_GYPSUM  # scripted group (container) (typed FeaturePython)
  Dunit = g/cm3
  Dvalue = 2.32
  Group = -> [Ca_element012,S_element014,O_element049,H_element045]
  conduct = 2
  density = 1
  expand = 3
  formula = G4_GYPSUM
  name = G4_GYPSUM
  specific = 4
FEATURE [App::DocumentObjectGroupPython] C_element052  label="C_element : 7"  # scripted group (container) (typed FeaturePython)
  n = 7
  ref = C_element
FEATURE [App::DocumentObjectGroupPython] H_element046  label="H_element : 16"  # scripted group (container) (typed FeaturePython)
  n = 16
  ref = H_element
FEATURE [App::DocumentObjectGroupPython] G4_N_HEPTANE  label="G4_N-HEPTANE"  # scripted group (container) (typed FeaturePython)
  Dunit = g/cm3
  Dvalue = 0.68376
  Group = -> [C_element052,H_element046]
  conduct = 2
  density = 1
  expand = 3
  formula = G4_N-HEPTANE
  name = G4_N-HEPTANE
  specific = 4
FEATURE [App::DocumentObjectGroupPython] C_element053  label="C_element : 029"  # scripted group (container) (typed FeaturePython)
  n = 6
  ref = C_element
FEATURE [App::DocumentObjectGroupPython] H_element047  label="H_element : 14"  # scripted group (container) (typed FeaturePython)
  n = 14
  ref = H_element
FEATURE [App::DocumentObjectGroupPython] G4_N_HEXANE  label="G4_N-HEXANE"  # scripted group (container) (typed FeaturePython)
  Dunit = g/cm3
  Dvalue = 0.6603
  Group = -> [C_element053,H_element047]
  conduct = 2
  density = 1
  expand = 3
  formula = G4_N-HEXANE
  name = G4_N-HEXANE
  specific = 4
FEATURE [App::DocumentObjectGroupPython] C_element054  label="C_element : 22"  # scripted group (container) (typed FeaturePython)
  n = 22
  ref = C_element
FEATURE [App::DocumentObjectGroupPython] H_element048  label="H_element : 025"  # scripted group (container) (typed FeaturePython)
  n = 10
  ref = H_element
FEATURE [App::DocumentObjectGroupPython] N_element021  label="N_element : 010"  # scripted group (container) (typed FeaturePython)
  n = 2
  ref = N_element
FEATURE [App::DocumentObjectGroupPython] O_element050  label="O_element : 025"  # scripted group (container) (typed FeaturePython)
  n = 5
  ref = O_element
FEATURE [App::DocumentObjectGroupPython] G4_KAPTON  # scripted group (container) (typed FeaturePython)
  Dunit = g/cm3
  Dvalue = 1.42
  Group = -> [C_element054,H_element048,N_element021,O_element050]
  conduct = 2
  density = 1
  expand = 3
  formula = G4_KAPTON
  name = G4_KAPTON
  specific = 4
FEATURE [App::DocumentObjectGroupPython] La_element001  label="La_element : 1"  # scripted group (container) (typed FeaturePython)
  n = 1
  ref = La_element
FEATURE [App::DocumentObjectGroupPython] Br_element003  label="Br_element : 002"  # scripted group (container) (typed FeaturePython)
  n = 1
  ref = Br_element
FEATURE [App::DocumentObjectGroupPython] O_element051  label="O_element : 026"  # scripted group (container) (typed FeaturePython)
  n = 1
  ref = O_element
FEATURE [App::DocumentObjectGroupPython] G4_LANTHANUM_OXYBROMIDE  # scripted group (container) (typed FeaturePython)
  Dunit = g/cm3
  Dvalue = 6.28
  Group = -> [La_element001,Br_element003,O_element051]
  conduct = 2
  density = 1
  expand = 3
  formula = G4_LANTHANUM_OXYBROMIDE
  name = G4_LANTHANUM_OXYBROMIDE
  specific = 4
FEATURE [App::DocumentObjectGroupPython] La_element002  label="La_element : 2"  # scripted group (container) (typed FeaturePython)
  n = 2
  ref = La_element
FEATURE [App::DocumentObjectGroupPython] O_element052  label="O_element : 027"  # scripted group (container) (typed FeaturePython)
  n = 2
  ref = O_element
FEATURE [App::DocumentObjectGroupPython] S_element015  label="S_element : 006"  # scripted group (container) (typed FeaturePython)
  n = 1
  ref = S_element
FEATURE [App::DocumentObjectGroupPython] G4_LANTHANUM_OXYSULFIDE  # scripted group (container) (typed FeaturePython)
  Dunit = g/cm3
  Dvalue = 5.86
  Group = -> [La_element002,O_element052,S_element015]
  conduct = 2
  density = 1
  expand = 3
  formula = G4_LANTHANUM_OXYSULFIDE
  name = G4_LANTHANUM_OXYSULFIDE
  specific = 4
FEATURE [App::DocumentObjectGroupPython] O_element053  label="O_element : 0.072"  # scripted group (container) (typed FeaturePython)
  n = 0.071682
FEATURE [App::DocumentObjectGroupPython] Pb_element002  label="Pb_element : 0.928"  # scripted group (container) (typed FeaturePython)
  n = 0.928318
FEATURE [App::DocumentObjectGroupPython] G4_LEAD_OXIDE  # scripted group (container) (typed FeaturePython)
  Dunit = g/cm3
  Dvalue = 9.53
  Group = -> [O_element053,Pb_element002]
  conduct = 2
  density = 1
  expand = 3
  formula = G4_LEAD_OXIDE
  name = G4_LEAD_OXIDE
  specific = 4
FEATURE [App::DocumentObjectGroupPython] Li_element001  label="Li_element : 1"  # scripted group (container) (typed FeaturePython)
  n = 1
  ref = Li_element
FEATURE [App::DocumentObjectGroupPython] N_element022  label="N_element : 011"  # scripted group (container) (typed FeaturePython)
  n = 1
  ref = N_element
FEATURE [App::DocumentObjectGroupPython] H_element049  label="H_element : 026"  # scripted group (container) (typed FeaturePython)
  n = 2
  ref = H_element
FEATURE [App::DocumentObjectGroupPython] G4_LITHIUM_AMIDE  # scripted group (container) (typed FeaturePython)
  Dunit = g/cm3
  Dvalue = 1.178
  Group = -> [Li_element001,N_element022,H_element049]
  conduct = 2
  density = 1
  expand = 3
  formula = G4_LITHIUM_AMIDE
  name = G4_LITHIUM_AMIDE
  specific = 4
FEATURE [App::DocumentObjectGroupPython] Li_element002  label="Li_element : 2"  # scripted group (container) (typed FeaturePython)
  n = 2
  ref = Li_element
FEATURE [App::DocumentObjectGroupPython] C_element055  label="C_element : 030"  # scripted group (container) (typed FeaturePython)
  n = 1
  ref = C_element
FEATURE [App::DocumentObjectGroupPython] O_element054  label="O_element : 028"  # scripted group (container) (typed FeaturePython)
  n = 3
  ref = O_element
FEATURE [App::DocumentObjectGroupPython] G4_LITHIUM_CARBONATE  # scripted group (container) (typed FeaturePython)
  Dunit = g/cm3
  Dvalue = 2.11
  Group = -> [Li_element002,C_element055,O_element054]
  conduct = 2
  density = 1
  expand = 3
  formula = G4_LITHIUM_CARBONATE
  name = G4_LITHIUM_CARBONATE
  specific = 4
FEATURE [App::DocumentObjectGroupPython] Li_element003  label="Li_element : 003"  # scripted group (container) (typed FeaturePython)
  n = 1
  ref = Li_element
FEATURE [App::DocumentObjectGroupPython] F_element012  label="F_element : 004"  # scripted group (container) (typed FeaturePython)
  n = 1
  ref = F_element
FEATURE [App::DocumentObjectGroupPython] G4_LITHIUM_FLUORIDE  # scripted group (container) (typed FeaturePython)
  Dunit = g/cm3
  Dvalue = 2.635
  Group = -> [Li_element003,F_element012]
  conduct = 2
  density = 1
  expand = 3
  formula = G4_LITHIUM_FLUORIDE
  name = G4_LITHIUM_FLUORIDE
  specific = 4
FEATURE [App::DocumentObjectGroupPython] Li_element004  label="Li_element : 004"  # scripted group (container) (typed FeaturePython)
  n = 1
  ref = Li_element
FEATURE [App::DocumentObjectGroupPython] H_element050  label="H_element : 027"  # scripted group (container) (typed FeaturePython)
  n = 1
  ref = H_element
FEATURE [App::DocumentObjectGroupPython] G4_LITHIUM_HYDRIDE  # scripted group (container) (typed FeaturePython)
  Dunit = g/cm3
  Dvalue = 0.82
  Group = -> [Li_element004,H_element050]
  conduct = 2
  density = 1
  expand = 3
  formula = G4_LITHIUM_HYDRIDE
  name = G4_LITHIUM_HYDRIDE
  specific = 4
FEATURE [App::DocumentObjectGroupPython] Li_element005  label="Li_element : 005"  # scripted group (container) (typed FeaturePython)
  n = 1
  ref = Li_element
FEATURE [App::DocumentObjectGroupPython] I_element003  label="I_element : 002"  # scripted group (container) (typed FeaturePython)
  n = 1
  ref = I_element
FEATURE [App::DocumentObjectGroupPython] G4_LITHIUM_IODIDE  # scripted group (container) (typed FeaturePython)
  Dunit = g/cm3
  Dvalue = 3.494
  Group = -> [Li_element005,I_element003]
  conduct = 2
  density = 1
  expand = 3
  formula = G4_LITHIUM_IODIDE
  name = G4_LITHIUM_IODIDE
  specific = 4
FEATURE [App::DocumentObjectGroupPython] Li_element006  label="Li_element : 006"  # scripted group (container) (typed FeaturePython)
  n = 2
  ref = Li_element
FEATURE [App::DocumentObjectGroupPython] O_element055  label="O_element : 029"  # scripted group (container) (typed FeaturePython)
  n = 1
  ref = O_element
FEATURE [App::DocumentObjectGroupPython] G4_LITHIUM_OXIDE  # scripted group (container) (typed FeaturePython)
  Dunit = g/cm3
  Dvalue = 2.013
  Group = -> [Li_element006,O_element055]
  conduct = 2
  density = 1
  expand = 3
  formula = G4_LITHIUM_OXIDE
  name = G4_LITHIUM_OXIDE
  specific = 4
FEATURE [App::DocumentObjectGroupPython] Li_element007  label="Li_element : 007"  # scripted group (container) (typed FeaturePython)
  n = 2
  ref = Li_element
FEATURE [App::DocumentObjectGroupPython] B_element005  label="B_element : 005"  # scripted group (container) (typed FeaturePython)
  n = 4
  ref = B_element
FEATURE [App::DocumentObjectGroupPython] O_element056  label="O_element : 7"  # scripted group (container) (typed FeaturePython)
  n = 7
  ref = O_element
FEATURE [App::DocumentObjectGroupPython] G4_LITHIUM_TETRABORATE  # scripted group (container) (typed FeaturePython)
  Dunit = g/cm3
  Dvalue = 2.44
  Group = -> [Li_element007,B_element005,O_element056]
  conduct = 2
  density = 1
  expand = 3
  formula = G4_LITHIUM_TETRABORATE
  name = G4_LITHIUM_TETRABORATE
  specific = 4
FEATURE [App::DocumentObjectGroupPython] H_element051  label="H_element : 0.105"  # scripted group (container) (typed FeaturePython)
  n = 0.105
FEATURE [App::DocumentObjectGroupPython] C_element056  label="C_element : 0.083"  # scripted group (container) (typed FeaturePython)
  n = 0.083
FEATURE [App::DocumentObjectGroupPython] N_element023  label="N_element : 0.023"  # scripted group (container) (typed FeaturePython)
  n = 0.023
FEATURE [App::DocumentObjectGroupPython] O_element057  label="O_element : 0.779"  # scripted group (container) (typed FeaturePython)
  n = 0.779
FEATURE [App::DocumentObjectGroupPython] Na_element010  label="Na_element : 0.097"  # scripted group (container) (typed FeaturePython)
  n = 0.002
FEATURE [App::DocumentObjectGroupPython] P_element006  label="P_element : 0.105"  # scripted group (container) (typed FeaturePython)
  n = 0.001
FEATURE [App::DocumentObjectGroupPython] S_element016  label="S_element : 0.017"  # scripted group (container) (typed FeaturePython)
  n = 0.002
FEATURE [App::DocumentObjectGroupPython] Cl_element014  label="Cl_element : 0.587"  # scripted group (container) (typed FeaturePython)
  n = 0.003
FEATURE [App::DocumentObjectGroupPython] K_element005  label="K_element : 0.015"  # scripted group (container) (typed FeaturePython)
  n = 0.002
FEATURE [App::DocumentObjectGroupPython] G4_LUNG_ICRP  # scripted group (container) (typed FeaturePython)
  Dunit = g/cm3
  Dvalue = 1.04
  Group = -> [H_element051,C_element056,N_element023,O_element057,Na_element010,P_element006,S_element016,Cl_element014,K_element005]
  conduct = 2
  density = 1
  expand = 3
  formula = G4_LUNG_ICRP
  name = G4_LUNG_ICRP
  specific = 4
FEATURE [App::DocumentObjectGroupPython] H_element052  label="H_element : 0.116"  # scripted group (container) (typed FeaturePython)
  n = 0.114318
FEATURE [App::DocumentObjectGroupPython] C_element057  label="C_element : 0.656"  # scripted group (container) (typed FeaturePython)
  n = 0.655824
FEATURE [App::DocumentObjectGroupPython] O_element058  label="O_element : 0.092"  # scripted group (container) (typed FeaturePython)
  n = 0.0921831
FEATURE [App::DocumentObjectGroupPython] Mg_element004  label="Mg_element : 0.135"  # scripted group (container) (typed FeaturePython)
  n = 0.134792
FEATURE [App::DocumentObjectGroupPython] Ca_element013  label="Ca_element : 0.003"  # scripted group (container) (typed FeaturePython)
  n = 0.002883
FEATURE [App::DocumentObjectGroupPython] G4_M3_WAX  # scripted group (container) (typed FeaturePython)
  Dunit = g/cm3
  Dvalue = 1.05
  Group = -> [H_element052,C_element057,O_element058,Mg_element004,Ca_element013]
  conduct = 2
  density = 1
  expand = 3
  formula = G4_M3_WAX
  name = G4_M3_WAX
  specific = 4
FEATURE [App::DocumentObjectGroupPython] Mg_element005  label="Mg_element : 1"  # scripted group (container) (typed FeaturePython)
  n = 1
  ref = Mg_element
FEATURE [App::DocumentObjectGroupPython] C_element058  label="C_element : 031"  # scripted group (container) (typed FeaturePython)
  n = 1
  ref = C_element
FEATURE [App::DocumentObjectGroupPython] O_element059  label="O_element : 030"  # scripted group (container) (typed FeaturePython)
  n = 3
  ref = O_element
FEATURE [App::DocumentObjectGroupPython] G4_MAGNESIUM_CARBONATE  # scripted group (container) (typed FeaturePython)
  Dunit = g/cm3
  Dvalue = 2.958
  Group = -> [Mg_element005,C_element058,O_element059]
  conduct = 2
  density = 1
  expand = 3
  formula = G4_MAGNESIUM_CARBONATE
  name = G4_MAGNESIUM_CARBONATE
  specific = 4
FEATURE [App::DocumentObjectGroupPython] Mg_element006  label="Mg_element : 002"  # scripted group (container) (typed FeaturePython)
  n = 1
  ref = Mg_element
FEATURE [App::DocumentObjectGroupPython] F_element013  label="F_element : 005"  # scripted group (container) (typed FeaturePython)
  n = 2
  ref = F_element
FEATURE [App::DocumentObjectGroupPython] G4_MAGNESIUM_FLUORIDE  # scripted group (container) (typed FeaturePython)
  Dunit = g/cm3
  Dvalue = 3
  Group = -> [Mg_element006,F_element013]
  conduct = 2
  density = 1
  expand = 3
  formula = G4_MAGNESIUM_FLUORIDE
  name = G4_MAGNESIUM_FLUORIDE
  specific = 4
FEATURE [App::DocumentObjectGroupPython] Mg_element007  label="Mg_element : 003"  # scripted group (container) (typed FeaturePython)
  n = 1
  ref = Mg_element
FEATURE [App::DocumentObjectGroupPython] O_element060  label="O_element : 031"  # scripted group (container) (typed FeaturePython)
  n = 1
  ref = O_element
FEATURE [App::DocumentObjectGroupPython] G4_MAGNESIUM_OXIDE  # scripted group (container) (typed FeaturePython)
  Dunit = g/cm3
  Dvalue = 3.58
  Group = -> [Mg_element007,O_element060]
  conduct = 2
  density = 1
  expand = 3
  formula = G4_MAGNESIUM_OXIDE
  name = G4_MAGNESIUM_OXIDE
  specific = 4
FEATURE [App::DocumentObjectGroupPython] Mg_element008  label="Mg_element : 004"  # scripted group (container) (typed FeaturePython)
  n = 1
  ref = Mg_element
FEATURE [App::DocumentObjectGroupPython] B_element006  label="B_element : 006"  # scripted group (container) (typed FeaturePython)
  n = 4
  ref = B_element
FEATURE [App::DocumentObjectGroupPython] O_element061  label="O_element : 032"  # scripted group (container) (typed FeaturePython)
  n = 7
  ref = O_element
FEATURE [App::DocumentObjectGroupPython] G4_MAGNESIUM_TETRABORATE  # scripted group (container) (typed FeaturePython)
  Dunit = g/cm3
  Dvalue = 2.53
  Group = -> [Mg_element008,B_element006,O_element061]
  conduct = 2
  density = 1
  expand = 3
  formula = G4_MAGNESIUM_TETRABORATE
  name = G4_MAGNESIUM_TETRABORATE
  specific = 4
FEATURE [App::DocumentObjectGroupPython] Hg_element001  label="Hg_element : 1"  # scripted group (container) (typed FeaturePython)
  n = 1
  ref = Hg_element
FEATURE [App::DocumentObjectGroupPython] I_element004  label="I_element : 2"  # scripted group (container) (typed FeaturePython)
  n = 2
  ref = I_element
FEATURE [App::DocumentObjectGroupPython] G4_MERCURIC_IODIDE  # scripted group (container) (typed FeaturePython)
  Dunit = g/cm3
  Dvalue = 6.36
  Group = -> [Hg_element001,I_element004]
  conduct = 2
  density = 1
  expand = 3
  formula = G4_MERCURIC_IODIDE
  name = G4_MERCURIC_IODIDE
  specific = 4
FEATURE [App::DocumentObjectGroupPython] C_element059  label="C_element : 032"  # scripted group (container) (typed FeaturePython)
  n = 1
  ref = C_element
FEATURE [App::DocumentObjectGroupPython] H_element053  label="H_element : 028"  # scripted group (container) (typed FeaturePython)
  n = 4
  ref = H_element
FEATURE [App::DocumentObjectGroupPython] G4_METHANE  # scripted group (container) (typed FeaturePython)
  Dunit = g/cm3
  Dvalue = 0.000667151
  Group = -> [C_element059,H_element053]
  conduct = 2
  density = 1
  expand = 3
  formula = G4_METHANE
  name = G4_METHANE
  specific = 4
FEATURE [App::DocumentObjectGroupPython] C_element060  label="C_element : 033"  # scripted group (container) (typed FeaturePython)
  n = 1
  ref = C_element
FEATURE [App::DocumentObjectGroupPython] H_element054  label="H_element : 029"  # scripted group (container) (typed FeaturePython)
  n = 4
  ref = H_element
FEATURE [App::DocumentObjectGroupPython] O_element062  label="O_element : 033"  # scripted group (container) (typed FeaturePython)
  n = 1
  ref = O_element
FEATURE [App::DocumentObjectGroupPython] G4_METHANOL  # scripted group (container) (typed FeaturePython)
  Dunit = g/cm3
  Dvalue = 0.7914
  Group = -> [C_element060,H_element054,O_element062]
  conduct = 2
  density = 1
  expand = 3
  formula = G4_METHANOL
  name = G4_METHANOL
  specific = 4
FEATURE [App::DocumentObjectGroupPython] H_element055  label="H_element : 0.134"  # scripted group (container) (typed FeaturePython)
  n = 0.13404
FEATURE [App::DocumentObjectGroupPython] C_element061  label="C_element : 0.778"  # scripted group (container) (typed FeaturePython)
  n = 0.77796
FEATURE [App::DocumentObjectGroupPython] O_element063  label="O_element : 0.035"  # scripted group (container) (typed FeaturePython)
  n = 0.03502
FEATURE [App::DocumentObjectGroupPython] Mg_element009  label="Mg_element : 0.039"  # scripted group (container) (typed FeaturePython)
  n = 0.038594
FEATURE [App::DocumentObjectGroupPython] Ti_element002  label="Ti_element : 0.014"  # scripted group (container) (typed FeaturePython)
  n = 0.014386
FEATURE [App::DocumentObjectGroupPython] G4_MIX_D_WAX  # scripted group (container) (typed FeaturePython)
  Dunit = g/cm3
  Dvalue = 0.99
  Group = -> [H_element055,C_element061,O_element063,Mg_element009,Ti_element002]
  conduct = 2
  density = 1
  expand = 3
  formula = G4_MIX_D_WAX
  name = G4_MIX_D_WAX
  specific = 4
FEATURE [App::DocumentObjectGroupPython] H_element056  label="H_element : 0.135"  # scripted group (container) (typed FeaturePython)
  n = 0.081192
FEATURE [App::DocumentObjectGroupPython] C_element062  label="C_element : 0.583"  # scripted group (container) (typed FeaturePython)
  n = 0.583442
FEATURE [App::DocumentObjectGroupPython] N_element024  label="N_element : 0.018"  # scripted group (container) (typed FeaturePython)
  n = 0.017798
FEATURE [App::DocumentObjectGroupPython] O_element064  label="O_element : 0.186"  # scripted group (container) (typed FeaturePython)
  n = 0.186381
FEATURE [App::DocumentObjectGroupPython] Mg_element010  label="Mg_element : 0.130"  # scripted group (container) (typed FeaturePython)
  n = 0.130287
FEATURE [App::DocumentObjectGroupPython] Cl_element015  label="Cl_element : 0.588"  # scripted group (container) (typed FeaturePython)
  n = 0.0009
FEATURE [App::DocumentObjectGroupPython] G4_MS20_TISSUE  # scripted group (container) (typed FeaturePython)
  Dunit = g/cm3
  Dvalue = 1
  Group = -> [H_element056,C_element062,N_element024,O_element064,Mg_element010,Cl_element015]
  conduct = 2
  density = 1
  expand = 3
  formula = G4_MS20_TISSUE
  name = G4_MS20_TISSUE
  specific = 4
FEATURE [App::DocumentObjectGroupPython] H_element057  label="H_element : 0.136"  # scripted group (container) (typed FeaturePython)
  n = 0.102
FEATURE [App::DocumentObjectGroupPython] C_element063  label="C_element : 0.143"  # scripted group (container) (typed FeaturePython)
  n = 0.143
FEATURE [App::DocumentObjectGroupPython] N_element025  label="N_element : 0.034"  # scripted group (container) (typed FeaturePython)
  n = 0.034
FEATURE [App::DocumentObjectGroupPython] O_element065  label="O_element : 0.710"  # scripted group (container) (typed FeaturePython)
  n = 0.71
FEATURE [App::DocumentObjectGroupPython] Na_element011  label="Na_element : 0.098"  # scripted group (container) (typed FeaturePython)
  n = 0.001
FEATURE [App::DocumentObjectGroupPython] P_element007  label="P_element : 0.002"  # scripted group (container) (typed FeaturePython)
  n = 0.002
FEATURE [App::DocumentObjectGroupPython] S_element017  label="S_element : 0.018"  # scripted group (container) (typed FeaturePython)
  n = 0.003
FEATURE [App::DocumentObjectGroupPython] Cl_element016  label="Cl_element : 0.589"  # scripted group (container) (typed FeaturePython)
  n = 0.001
FEATURE [App::DocumentObjectGroupPython] K_element006  label="K_element : 0.004"  # scripted group (container) (typed FeaturePython)
  n = 0.004
FEATURE [App::DocumentObjectGroupPython] G4_MUSCLE_SKELETAL_ICRP  # scripted group (container) (typed FeaturePython)
  Dunit = g/cm3
  Dvalue = 1.05
  Group = -> [H_element057,C_element063,N_element025,O_element065,Na_element011,P_element007,S_element017,Cl_element016,K_element006]
  conduct = 2
  density = 1
  expand = 3
  formula = G4_MUSCLE_SKELETAL_ICRP
  name = G4_MUSCLE_SKELETAL_ICRP
  specific = 4
FEATURE [App::DocumentObjectGroupPython] H_element058  label="H_element : 0.137"  # scripted group (container) (typed FeaturePython)
  n = 0.102102
FEATURE [App::DocumentObjectGroupPython] C_element064  label="C_element : 0.123"  # scripted group (container) (typed FeaturePython)
  n = 0.123123
FEATURE [App::DocumentObjectGroupPython] N_element026  label="N_element : 0.756"  # scripted group (container) (typed FeaturePython)
  n = 0.035035
FEATURE [App::DocumentObjectGroupPython] O_element066  label="O_element : 0.730"  # scripted group (container) (typed FeaturePython)
  n = 0.72973
FEATURE [App::DocumentObjectGroupPython] Na_element012  label="Na_element : 0.099"  # scripted group (container) (typed FeaturePython)
  n = 0.001001
FEATURE [App::DocumentObjectGroupPython] P_element008  label="P_element : 0.106"  # scripted group (container) (typed FeaturePython)
  n = 0.002002
FEATURE [App::DocumentObjectGroupPython] S_element018  label="S_element : 0.019"  # scripted group (container) (typed FeaturePython)
  n = 0.004004
FEATURE [App::DocumentObjectGroupPython] K_element007  label="K_element : 0.016"  # scripted group (container) (typed FeaturePython)
  n = 0.003003
FEATURE [App::DocumentObjectGroupPython] G4_MUSCLE_STRIATED_ICRU  # scripted group (container) (typed FeaturePython)
  Dunit = g/cm3
  Dvalue = 1.04
  Group = -> [H_element058,C_element064,N_element026,O_element066,Na_element012,P_element008,S_element018,K_element007]
  conduct = 2
  density = 1
  expand = 3
  formula = G4_MUSCLE_STRIATED_ICRU
  name = G4_MUSCLE_STRIATED_ICRU
  specific = 4
FEATURE [App::DocumentObjectGroupPython] H_element059  label="H_element : 0.098"  # scripted group (container) (typed FeaturePython)
  n = 0.0982341
FEATURE [App::DocumentObjectGroupPython] C_element065  label="C_element : 0.156"  # scripted group (container) (typed FeaturePython)
  n = 0.156214
FEATURE [App::DocumentObjectGroupPython] N_element027  label="N_element : 0.757"  # scripted group (container) (typed FeaturePython)
  n = 0.035451
FEATURE [App::DocumentObjectGroupPython] O_element067  label="O_element : 0.880"  # scripted group (container) (typed FeaturePython)
  n = 0.710101
FEATURE [App::DocumentObjectGroupPython] G4_MUSCLE_WITH_SUCROSE  # scripted group (container) (typed FeaturePython)
  Dunit = g/cm3
  Dvalue = 1.11
  Group = -> [H_element059,C_element065,N_element027,O_element067]
  conduct = 2
  density = 1
  expand = 3
  formula = G4_MUSCLE_WITH_SUCROSE
  name = G4_MUSCLE_WITH_SUCROSE
  specific = 4
FEATURE [App::DocumentObjectGroupPython] H_element060  label="H_element : 0.138"  # scripted group (container) (typed FeaturePython)
  n = 0.101969
FEATURE [App::DocumentObjectGroupPython] C_element066  label="C_element : 0.120"  # scripted group (container) (typed FeaturePython)
  n = 0.120058
FEATURE [App::DocumentObjectGroupPython] N_element028  label="N_element : 0.758"  # scripted group (container) (typed FeaturePython)
  n = 0.035451
FEATURE [App::DocumentObjectGroupPython] O_element068  label="O_element : 0.743"  # scripted group (container) (typed FeaturePython)
  n = 0.742522
FEATURE [App::DocumentObjectGroupPython] G4_MUSCLE_WITHOUT_SUCROSE  # scripted group (container) (typed FeaturePython)
  Dunit = g/cm3
  Dvalue = 1.07
  Group = -> [H_element060,C_element066,N_element028,O_element068]
  conduct = 2
  density = 1
  expand = 3
  formula = G4_MUSCLE_WITHOUT_SUCROSE
  name = G4_MUSCLE_WITHOUT_SUCROSE
  specific = 4
FEATURE [App::DocumentObjectGroupPython] C_element067  label="C_element : 10"  # scripted group (container) (typed FeaturePython)
  n = 10
  ref = C_element
FEATURE [App::DocumentObjectGroupPython] H_element061  label="H_element : 030"  # scripted group (container) (typed FeaturePython)
  n = 8
  ref = H_element
FEATURE [App::DocumentObjectGroupPython] G4_NAPHTHALENE  # scripted group (container) (typed FeaturePython)
  Dunit = g/cm3
  Dvalue = 1.145
  Group = -> [C_element067,H_element061]
  conduct = 2
  density = 1
  expand = 3
  formula = G4_NAPHTHALENE
  name = G4_NAPHTHALENE
  specific = 4
FEATURE [App::DocumentObjectGroupPython] C_element068  label="C_element : 034"  # scripted group (container) (typed FeaturePython)
  n = 6
  ref = C_element
FEATURE [App::DocumentObjectGroupPython] H_element062  label="H_element : 031"  # scripted group (container) (typed FeaturePython)
  n = 5
  ref = H_element
FEATURE [App::DocumentObjectGroupPython] N_element029  label="N_element : 012"  # scripted group (container) (typed FeaturePython)
  n = 1
  ref = N_element
FEATURE [App::DocumentObjectGroupPython] O_element069  label="O_element : 034"  # scripted group (container) (typed FeaturePython)
  n = 2
  ref = O_element
FEATURE [App::DocumentObjectGroupPython] G4_NITROBENZENE  # scripted group (container) (typed FeaturePython)
  Dunit = g/cm3
  Dvalue = 1.19867
  Group = -> [C_element068,H_element062,N_element029,O_element069]
  conduct = 2
  density = 1
  expand = 3
  formula = G4_NITROBENZENE
  name = G4_NITROBENZENE
  specific = 4
FEATURE [App::DocumentObjectGroupPython] N_element030  label="N_element : 013"  # scripted group (container) (typed FeaturePython)
  n = 2
  ref = N_element
FEATURE [App::DocumentObjectGroupPython] O_element070  label="O_element : 035"  # scripted group (container) (typed FeaturePython)
  n = 1
  ref = O_element
FEATURE [App::DocumentObjectGroupPython] G4_NITROUS_OXIDE  # scripted group (container) (typed FeaturePython)
  Dunit = g/cm3
  Dvalue = 0.00183094
  Group = -> [N_element030,O_element070]
  conduct = 2
  density = 1
  expand = 3
  formula = G4_NITROUS_OXIDE
  name = G4_NITROUS_OXIDE
  specific = 4
FEATURE [App::DocumentObjectGroupPython] H_element063  label="H_element : 0.104"  # scripted group (container) (typed FeaturePython)
  n = 0.103509
FEATURE [App::DocumentObjectGroupPython] C_element069  label="C_element : 0.648"  # scripted group (container) (typed FeaturePython)
  n = 0.648416
FEATURE [App::DocumentObjectGroupPython] N_element031  label="N_element : 0.100"  # scripted group (container) (typed FeaturePython)
  n = 0.0995361
FEATURE [App::DocumentObjectGroupPython] O_element071  label="O_element : 0.149"  # scripted group (container) (typed FeaturePython)
  n = 0.148539
FEATURE [App::DocumentObjectGroupPython] G4_NYLON_8062  label="G4_NYLON-8062"  # scripted group (container) (typed FeaturePython)
  Dunit = g/cm3
  Dvalue = 1.08
  Group = -> [H_element063,C_element069,N_element031,O_element071]
  conduct = 2
  density = 1
  expand = 3
  formula = G4_NYLON-8062
  name = G4_NYLON-8062
  specific = 4
FEATURE [App::DocumentObjectGroupPython] C_element070  label="C_element : 035"  # scripted group (container) (typed FeaturePython)
  n = 6
  ref = C_element
FEATURE [App::DocumentObjectGroupPython] H_element064  label="H_element : 11"  # scripted group (container) (typed FeaturePython)
  n = 11
  ref = H_element
FEATURE [App::DocumentObjectGroupPython] N_element032  label="N_element : 014"  # scripted group (container) (typed FeaturePython)
  n = 1
  ref = N_element
FEATURE [App::DocumentObjectGroupPython] O_element072  label="O_element : 036"  # scripted group (container) (typed FeaturePython)
  n = 1
  ref = O_element
FEATURE [App::DocumentObjectGroupPython] G4_NYLON_6_6  label="G4_NYLON-6-6"  # scripted group (container) (typed FeaturePython)
  Dunit = g/cm3
  Dvalue = 1.14
  Group = -> [C_element070,H_element064,N_element032,O_element072]
  conduct = 2
  density = 1
  expand = 3
  formula = G4_NYLON-6-6
  name = G4_NYLON-6-6
  specific = 4
FEATURE [App::DocumentObjectGroupPython] H_element065  label="H_element : 0.139"  # scripted group (container) (typed FeaturePython)
  n = 0.107062
FEATURE [App::DocumentObjectGroupPython] C_element071  label="C_element : 0.680"  # scripted group (container) (typed FeaturePython)
  n = 0.680449
FEATURE [App::DocumentObjectGroupPython] N_element033  label="N_element : 0.099"  # scripted group (container) (typed FeaturePython)
  n = 0.099189
FEATURE [App::DocumentObjectGroupPython] O_element073  label="O_element : 0.113"  # scripted group (container) (typed FeaturePython)
  n = 0.1133
FEATURE [App::DocumentObjectGroupPython] G4_NYLON_6_10  label="G4_NYLON-6-10"  # scripted group (container) (typed FeaturePython)
  Dunit = g/cm3
  Dvalue = 1.14
  Group = -> [H_element065,C_element071,N_element033,O_element073]
  conduct = 2
  density = 1
  expand = 3
  formula = G4_NYLON-6-10
  name = G4_NYLON-6-10
  specific = 4
FEATURE [App::DocumentObjectGroupPython] H_element066  label="H_element : 0.140"  # scripted group (container) (typed FeaturePython)
  n = 0.115476
FEATURE [App::DocumentObjectGroupPython] C_element072  label="C_element : 0.721"  # scripted group (container) (typed FeaturePython)
  n = 0.720818
FEATURE [App::DocumentObjectGroupPython] N_element034  label="N_element : 0.076"  # scripted group (container) (typed FeaturePython)
  n = 0.0764169
FEATURE [App::DocumentObjectGroupPython] O_element074  label="O_element : 0.087"  # scripted group (container) (typed FeaturePython)
  n = 0.0872889
FEATURE [App::DocumentObjectGroupPython] G4_NYLON_11_RILSAN  label="G4_NYLON-11_RILSAN"  # scripted group (container) (typed FeaturePython)
  Dunit = g/cm3
  Dvalue = 1.425
  Group = -> [H_element066,C_element072,N_element034,O_element074]
  conduct = 2
  density = 1
  expand = 3
  formula = G4_NYLON-11_RILSAN
  name = G4_NYLON-11_RILSAN
  specific = 4
FEATURE [App::DocumentObjectGroupPython] C_element073  label="C_element : 8"  # scripted group (container) (typed FeaturePython)
  n = 8
  ref = C_element
FEATURE [App::DocumentObjectGroupPython] H_element067  label="H_element : 18"  # scripted group (container) (typed FeaturePython)
  n = 18
  ref = H_element
FEATURE [App::DocumentObjectGroupPython] G4_OCTANE  # scripted group (container) (typed FeaturePython)
  Dunit = g/cm3
  Dvalue = 0.7026
  Group = -> [C_element073,H_element067]
  conduct = 2
  density = 1
  expand = 3
  formula = G4_OCTANE
  name = G4_OCTANE
  specific = 4
FEATURE [App::DocumentObjectGroupPython] C_element074  label="C_element : 25"  # scripted group (container) (typed FeaturePython)
  n = 25
  ref = C_element
FEATURE [App::DocumentObjectGroupPython] H_element068  label="H_element : 52"  # scripted group (container) (typed FeaturePython)
  n = 52
  ref = H_element
FEATURE [App::DocumentObjectGroupPython] G4_PARAFFIN  # scripted group (container) (typed FeaturePython)
  Dunit = g/cm3
  Dvalue = 0.93
  Group = -> [C_element074,H_element068]
  conduct = 2
  density = 1
  expand = 3
  formula = G4_PARAFFIN
  name = G4_PARAFFIN
  specific = 4
FEATURE [App::DocumentObjectGroupPython] C_element075  label="C_element : 036"  # scripted group (container) (typed FeaturePython)
  n = 5
  ref = C_element
FEATURE [App::DocumentObjectGroupPython] H_element069  label="H_element : 032"  # scripted group (container) (typed FeaturePython)
  n = 12
  ref = H_element
FEATURE [App::DocumentObjectGroupPython] G4_N_PENTANE  label="G4_N-PENTANE"  # scripted group (container) (typed FeaturePython)
  Dunit = g/cm3
  Dvalue = 0.6262
  Group = -> [C_element075,H_element069]
  conduct = 2
  density = 1
  expand = 3
  formula = G4_N-PENTANE
  name = G4_N-PENTANE
  specific = 4
FEATURE [App::DocumentObjectGroupPython] H_element070  label="H_element : 0.014"  # scripted group (container) (typed FeaturePython)
  n = 0.0141
FEATURE [App::DocumentObjectGroupPython] C_element076  label="C_element : 0.072"  # scripted group (container) (typed FeaturePython)
  n = 0.072261
FEATURE [App::DocumentObjectGroupPython] N_element035  label="N_element : 0.019"  # scripted group (container) (typed FeaturePython)
  n = 0.01932
FEATURE [App::DocumentObjectGroupPython] O_element075  label="O_element : 0.066"  # scripted group (container) (typed FeaturePython)
  n = 0.066101
FEATURE [App::DocumentObjectGroupPython] S_element019  label="S_element : 0.020"  # scripted group (container) (typed FeaturePython)
  n = 0.00189
FEATURE [App::DocumentObjectGroupPython] Br_element004  label="Br_element : 0.349"  # scripted group (container) (typed FeaturePython)
  n = 0.349103
FEATURE [App::DocumentObjectGroupPython] Ag_element001  label="Ag_element : 0.474"  # scripted group (container) (typed FeaturePython)
  n = 0.474105
FEATURE [App::DocumentObjectGroupPython] I_element005  label="I_element : 0.003"  # scripted group (container) (typed FeaturePython)
  n = 0.00312
FEATURE [App::DocumentObjectGroupPython] G4_PHOTO_EMULSION  # scripted group (container) (typed FeaturePython)
  Dunit = g/cm3
  Dvalue = 3.815
  Group = -> [H_element070,C_element076,N_element035,O_element075,S_element019,Br_element004,Ag_element001,I_element005]
  conduct = 2
  density = 1
  expand = 3
  formula = G4_PHOTO_EMULSION
  name = G4_PHOTO_EMULSION
  specific = 4
FEATURE [App::DocumentObjectGroupPython] C_element077  label="C_element : 9"  # scripted group (container) (typed FeaturePython)
  n = 9
  ref = C_element
FEATURE [App::DocumentObjectGroupPython] H_element071  label="H_element : 033"  # scripted group (container) (typed FeaturePython)
  n = 10
  ref = H_element
FEATURE [App::DocumentObjectGroupPython] G4_PLASTIC_SC_VINYLTOLUENE  # scripted group (container) (typed FeaturePython)
  Dunit = g/cm3
  Dvalue = 1.032
  Group = -> [C_element077,H_element071]
  conduct = 2
  density = 1
  expand = 3
  formula = G4_PLASTIC_SC_VINYLTOLUENE
  name = G4_PLASTIC_SC_VINYLTOLUENE
  specific = 4
FEATURE [App::DocumentObjectGroupPython] Pu_element001  label="Pu_element : 1"  # scripted group (container) (typed FeaturePython)
  n = 1
  ref = Pu_element
FEATURE [App::DocumentObjectGroupPython] O_element076  label="O_element : 037"  # scripted group (container) (typed FeaturePython)
  n = 2
  ref = O_element
FEATURE [App::DocumentObjectGroupPython] G4_PLUTONIUM_DIOXIDE  # scripted group (container) (typed FeaturePython)
  Dunit = g/cm3
  Dvalue = 11.46
  Group = -> [Pu_element001,O_element076]
  conduct = 2
  density = 1
  expand = 3
  formula = G4_PLUTONIUM_DIOXIDE
  name = G4_PLUTONIUM_DIOXIDE
  specific = 4
FEATURE [App::DocumentObjectGroupPython] C_element078  label="C_element : 037"  # scripted group (container) (typed FeaturePython)
  n = 3
  ref = C_element
FEATURE [App::DocumentObjectGroupPython] H_element072  label="H_element : 034"  # scripted group (container) (typed FeaturePython)
  n = 3
  ref = H_element
FEATURE [App::DocumentObjectGroupPython] N_element036  label="N_element : 015"  # scripted group (container) (typed FeaturePython)
  n = 1
  ref = N_element
FEATURE [App::DocumentObjectGroupPython] G4_POLYACRYLONITRILE  # scripted group (container) (typed FeaturePython)
  Dunit = g/cm3
  Dvalue = 1.17
  Group = -> [C_element078,H_element072,N_element036]
  conduct = 2
  density = 1
  expand = 3
  formula = G4_POLYACRYLONITRILE
  name = G4_POLYACRYLONITRILE
  specific = 4
FEATURE [App::DocumentObjectGroupPython] C_element079  label="C_element : 16"  # scripted group (container) (typed FeaturePython)
  n = 16
  ref = C_element
FEATURE [App::DocumentObjectGroupPython] H_element073  label="H_element : 035"  # scripted group (container) (typed FeaturePython)
  n = 14
  ref = H_element
FEATURE [App::DocumentObjectGroupPython] O_element077  label="O_element : 038"  # scripted group (container) (typed FeaturePython)
  n = 3
  ref = O_element
FEATURE [App::DocumentObjectGroupPython] G4_POLYCARBONATE  # scripted group (container) (typed FeaturePython)
  Dunit = g/cm3
  Dvalue = 1.2
  Group = -> [C_element079,H_element073,O_element077]
  conduct = 2
  density = 1
  expand = 3
  formula = G4_POLYCARBONATE
  name = G4_POLYCARBONATE
  specific = 4
FEATURE [App::DocumentObjectGroupPython] C_element080  label="C_element : 038"  # scripted group (container) (typed FeaturePython)
  n = 8
  ref = C_element
FEATURE [App::DocumentObjectGroupPython] H_element074  label="H_element : 036"  # scripted group (container) (typed FeaturePython)
  n = 7
  ref = H_element
FEATURE [App::DocumentObjectGroupPython] Cl_element017  label="Cl_element : 007"  # scripted group (container) (typed FeaturePython)
  n = 1
  ref = Cl_element
FEATURE [App::DocumentObjectGroupPython] G4_POLYCHLOROSTYRENE  # scripted group (container) (typed FeaturePython)
  Dunit = g/cm3
  Dvalue = 1.3
  Group = -> [C_element080,H_element074,Cl_element017]
  conduct = 2
  density = 1
  expand = 3
  formula = G4_POLYCHLOROSTYRENE
  name = G4_POLYCHLOROSTYRENE
  specific = 4
FEATURE [App::DocumentObjectGroupPython] C_element081  label="C_element : 039"  # scripted group (container) (typed FeaturePython)
  n = 1
  ref = C_element
FEATURE [App::DocumentObjectGroupPython] H_element075  label="H_element : 037"  # scripted group (container) (typed FeaturePython)
  n = 2
  ref = H_element
FEATURE [App::DocumentObjectGroupPython] G4_POLYETHYLENE  # scripted group (container) (typed FeaturePython)
  Dunit = g/cm3
  Dvalue = 0.94
  Group = -> [C_element081,H_element075]
  conduct = 2
  density = 1
  expand = 3
  formula = G4_POLYETHYLENE
  name = G4_POLYETHYLENE
  specific = 4
FEATURE [App::DocumentObjectGroupPython] C_element082  label="C_element : 040"  # scripted group (container) (typed FeaturePython)
  n = 10
  ref = C_element
FEATURE [App::DocumentObjectGroupPython] H_element076  label="H_element : 038"  # scripted group (container) (typed FeaturePython)
  n = 8
  ref = H_element
FEATURE [App::DocumentObjectGroupPython] O_element078  label="O_element : 039"  # scripted group (container) (typed FeaturePython)
  n = 4
  ref = O_element
FEATURE [App::DocumentObjectGroupPython] G4_MYLAR  # scripted group (container) (typed FeaturePython)
  Dunit = g/cm3
  Dvalue = 1.4
  Group = -> [C_element082,H_element076,O_element078]
  conduct = 2
  density = 1
  expand = 3
  formula = G4_MYLAR
  name = G4_MYLAR
  specific = 4
FEATURE [App::DocumentObjectGroupPython] C_element083  label="C_element : 041"  # scripted group (container) (typed FeaturePython)
  n = 5
  ref = C_element
FEATURE [App::DocumentObjectGroupPython] H_element077  label="H_element : 039"  # scripted group (container) (typed FeaturePython)
  n = 8
  ref = H_element
FEATURE [App::DocumentObjectGroupPython] O_element079  label="O_element : 040"  # scripted group (container) (typed FeaturePython)
  n = 2
  ref = O_element
FEATURE [App::DocumentObjectGroupPython] G4_PLEXIGLASS  # scripted group (container) (typed FeaturePython)
  Dunit = g/cm3
  Dvalue = 1.19
  Group = -> [C_element083,H_element077,O_element079]
  conduct = 2
  density = 1
  expand = 3
  formula = G4_PLEXIGLASS
  name = G4_PLEXIGLASS
  specific = 4
FEATURE [App::DocumentObjectGroupPython] C_element084  label="C_element : 042"  # scripted group (container) (typed FeaturePython)
  n = 1
  ref = C_element
FEATURE [App::DocumentObjectGroupPython] H_element078  label="H_element : 040"  # scripted group (container) (typed FeaturePython)
  n = 2
  ref = H_element
FEATURE [App::DocumentObjectGroupPython] O_element080  label="O_element : 041"  # scripted group (container) (typed FeaturePython)
  n = 1
  ref = O_element
FEATURE [App::DocumentObjectGroupPython] G4_POLYOXYMETHYLENE  # scripted group (container) (typed FeaturePython)
  Dunit = g/cm3
  Dvalue = 1.425
  Group = -> [C_element084,H_element078,O_element080]
  conduct = 2
  density = 1
  expand = 3
  formula = G4_POLYOXYMETHYLENE
  name = G4_POLYOXYMETHYLENE
  specific = 4
FEATURE [App::DocumentObjectGroupPython] C_element085  label="C_element : 043"  # scripted group (container) (typed FeaturePython)
  n = 2
  ref = C_element
FEATURE [App::DocumentObjectGroupPython] H_element079  label="H_element : 041"  # scripted group (container) (typed FeaturePython)
  n = 4
  ref = H_element
FEATURE [App::DocumentObjectGroupPython] G4_POLYPROPYLENE  # scripted group (container) (typed FeaturePython)
  Dunit = g/cm3
  Dvalue = 0.9
  Group = -> [C_element085,H_element079]
  conduct = 2
  density = 1
  expand = 3
  formula = G4_POLYPROPYLENE
  name = G4_POLYPROPYLENE
  specific = 4
FEATURE [App::DocumentObjectGroupPython] C_element086  label="C_element : 044"  # scripted group (container) (typed FeaturePython)
  n = 8
  ref = C_element
FEATURE [App::DocumentObjectGroupPython] H_element080  label="H_element : 042"  # scripted group (container) (typed FeaturePython)
  n = 8
  ref = H_element
FEATURE [App::DocumentObjectGroupPython] G4_POLYSTYRENE  # scripted group (container) (typed FeaturePython)
  Dunit = g/cm3
  Dvalue = 1.06
  Group = -> [C_element086,H_element080]
  conduct = 2
  density = 1
  expand = 3
  formula = G4_POLYSTYRENE
  name = G4_POLYSTYRENE
  specific = 4
FEATURE [App::DocumentObjectGroupPython] C_element087  label="C_element : 045"  # scripted group (container) (typed FeaturePython)
  n = 2
  ref = C_element
FEATURE [App::DocumentObjectGroupPython] F_element014  label="F_element : 4"  # scripted group (container) (typed FeaturePython)
  n = 4
  ref = F_element
FEATURE [App::DocumentObjectGroupPython] G4_TEFLON  # scripted group (container) (typed FeaturePython)
  Dunit = g/cm3
  Dvalue = 2.2
  Group = -> [C_element087,F_element014]
  conduct = 2
  density = 1
  expand = 3
  formula = G4_TEFLON
  name = G4_TEFLON
  specific = 4
FEATURE [App::DocumentObjectGroupPython] C_element088  label="C_element : 046"  # scripted group (container) (typed FeaturePython)
  n = 2
  ref = C_element
FEATURE [App::DocumentObjectGroupPython] F_element015  label="F_element : 006"  # scripted group (container) (typed FeaturePython)
  n = 3
  ref = F_element
FEATURE [App::DocumentObjectGroupPython] Cl_element018  label="Cl_element : 008"  # scripted group (container) (typed FeaturePython)
  n = 1
  ref = Cl_element
FEATURE [App::DocumentObjectGroupPython] G4_POLYTRIFLUOROCHLOROETHYLENE  # scripted group (container) (typed FeaturePython)
  Dunit = g/cm3
  Dvalue = 2.1
  Group = -> [C_element088,F_element015,Cl_element018]
  conduct = 2
  density = 1
  expand = 3
  formula = G4_POLYTRIFLUOROCHLOROETHYLENE
  name = G4_POLYTRIFLUOROCHLOROETHYLENE
  specific = 4
FEATURE [App::DocumentObjectGroupPython] C_element089  label="C_element : 047"  # scripted group (container) (typed FeaturePython)
  n = 4
  ref = C_element
FEATURE [App::DocumentObjectGroupPython] H_element081  label="H_element : 043"  # scripted group (container) (typed FeaturePython)
  n = 6
  ref = H_element
FEATURE [App::DocumentObjectGroupPython] O_element081  label="O_element : 042"  # scripted group (container) (typed FeaturePython)
  n = 2
  ref = O_element
FEATURE [App::DocumentObjectGroupPython] G4_POLYVINYL_ACETATE  # scripted group (container) (typed FeaturePython)
  Dunit = g/cm3
  Dvalue = 1.19
  Group = -> [C_element089,H_element081,O_element081]
  conduct = 2
  density = 1
  expand = 3
  formula = G4_POLYVINYL_ACETATE
  name = G4_POLYVINYL_ACETATE
  specific = 4
FEATURE [App::DocumentObjectGroupPython] C_element090  label="C_element : 048"  # scripted group (container) (typed FeaturePython)
  n = 2
  ref = C_element
FEATURE [App::DocumentObjectGroupPython] H_element082  label="H_element : 044"  # scripted group (container) (typed FeaturePython)
  n = 4
  ref = H_element
FEATURE [App::DocumentObjectGroupPython] O_element082  label="O_element : 043"  # scripted group (container) (typed FeaturePython)
  n = 1
  ref = O_element
FEATURE [App::DocumentObjectGroupPython] G4_POLYVINYL_ALCOHOL  # scripted group (container) (typed FeaturePython)
  Dunit = g/cm3
  Dvalue = 1.3
  Group = -> [C_element090,H_element082,O_element082]
  conduct = 2
  density = 1
  expand = 3
  formula = G4_POLYVINYL_ALCOHOL
  name = G4_POLYVINYL_ALCOHOL
  specific = 4
FEATURE [App::DocumentObjectGroupPython] C_element091  label="C_element : 049"  # scripted group (container) (typed FeaturePython)
  n = 8
  ref = C_element
FEATURE [App::DocumentObjectGroupPython] H_element083  label="H_element : 045"  # scripted group (container) (typed FeaturePython)
  n = 14
  ref = H_element
FEATURE [App::DocumentObjectGroupPython] O_element083  label="O_element : 044"  # scripted group (container) (typed FeaturePython)
  n = 2
  ref = O_element
FEATURE [App::DocumentObjectGroupPython] G4_POLYVINYL_BUTYRAL  # scripted group (container) (typed FeaturePython)
  Dunit = g/cm3
  Dvalue = 1.12
  Group = -> [C_element091,H_element083,O_element083]
  conduct = 2
  density = 1
  expand = 3
  formula = G4_POLYVINYL_BUTYRAL
  name = G4_POLYVINYL_BUTYRAL
  specific = 4
FEATURE [App::DocumentObjectGroupPython] C_element092  label="C_element : 050"  # scripted group (container) (typed FeaturePython)
  n = 2
  ref = C_element
FEATURE [App::DocumentObjectGroupPython] H_element084  label="H_element : 046"  # scripted group (container) (typed FeaturePython)
  n = 3
  ref = H_element
FEATURE [App::DocumentObjectGroupPython] Cl_element019  label="Cl_element : 009"  # scripted group (container) (typed FeaturePython)
  n = 1
  ref = Cl_element
FEATURE [App::DocumentObjectGroupPython] G4_POLYVINYL_CHLORIDE  # scripted group (container) (typed FeaturePython)
  Dunit = g/cm3
  Dvalue = 1.3
  Group = -> [C_element092,H_element084,Cl_element019]
  conduct = 2
  density = 1
  expand = 3
  formula = G4_POLYVINYL_CHLORIDE
  name = G4_POLYVINYL_CHLORIDE
  specific = 4
FEATURE [App::DocumentObjectGroupPython] C_element093  label="C_element : 051"  # scripted group (container) (typed FeaturePython)
  n = 2
  ref = C_element
FEATURE [App::DocumentObjectGroupPython] H_element085  label="H_element : 047"  # scripted group (container) (typed FeaturePython)
  n = 2
  ref = H_element
FEATURE [App::DocumentObjectGroupPython] Cl_element020  label="Cl_element : 010"  # scripted group (container) (typed FeaturePython)
  n = 2
  ref = Cl_element
FEATURE [App::DocumentObjectGroupPython] G4_POLYVINYLIDENE_CHLORIDE  # scripted group (container) (typed FeaturePython)
  Dunit = g/cm3
  Dvalue = 1.7
  Group = -> [C_element093,H_element085,Cl_element020]
  conduct = 2
  density = 1
  expand = 3
  formula = G4_POLYVINYLIDENE_CHLORIDE
  name = G4_POLYVINYLIDENE_CHLORIDE
  specific = 4
FEATURE [App::DocumentObjectGroupPython] C_element094  label="C_element : 052"  # scripted group (container) (typed FeaturePython)
  n = 2
  ref = C_element
FEATURE [App::DocumentObjectGroupPython] H_element086  label="H_element : 048"  # scripted group (container) (typed FeaturePython)
  n = 2
  ref = H_element
FEATURE [App::DocumentObjectGroupPython] F_element016  label="F_element : 007"  # scripted group (container) (typed FeaturePython)
  n = 2
  ref = F_element
FEATURE [App::DocumentObjectGroupPython] G4_POLYVINYLIDENE_FLUORIDE  # scripted group (container) (typed FeaturePython)
  Dunit = g/cm3
  Dvalue = 1.76
  Group = -> [C_element094,H_element086,F_element016]
  conduct = 2
  density = 1
  expand = 3
  formula = G4_POLYVINYLIDENE_FLUORIDE
  name = G4_POLYVINYLIDENE_FLUORIDE
  specific = 4
FEATURE [App::DocumentObjectGroupPython] C_element095  label="C_element : 053"  # scripted group (container) (typed FeaturePython)
  n = 6
  ref = C_element
FEATURE [App::DocumentObjectGroupPython] H_element087  label="H_element : 9"  # scripted group (container) (typed FeaturePython)
  n = 9
  ref = H_element
FEATURE [App::DocumentObjectGroupPython] N_element037  label="N_element : 016"  # scripted group (container) (typed FeaturePython)
  n = 1
  ref = N_element
FEATURE [App::DocumentObjectGroupPython] O_element084  label="O_element : 045"  # scripted group (container) (typed FeaturePython)
  n = 1
  ref = O_element
FEATURE [App::DocumentObjectGroupPython] G4_POLYVINYL_PYRROLIDONE  # scripted group (container) (typed FeaturePython)
  Dunit = g/cm3
  Dvalue = 1.25
  Group = -> [C_element095,H_element087,N_element037,O_element084]
  conduct = 2
  density = 1
  expand = 3
  formula = G4_POLYVINYL_PYRROLIDONE
  name = G4_POLYVINYL_PYRROLIDONE
  specific = 4
FEATURE [App::DocumentObjectGroupPython] K_element008  label="K_element : 1"  # scripted group (container) (typed FeaturePython)
  n = 1
  ref = K_element
FEATURE [App::DocumentObjectGroupPython] I_element006  label="I_element : 003"  # scripted group (container) (typed FeaturePython)
  n = 1
  ref = I_element
FEATURE [App::DocumentObjectGroupPython] G4_POTASSIUM_IODIDE  # scripted group (container) (typed FeaturePython)
  Dunit = g/cm3
  Dvalue = 3.13
  Group = -> [K_element008,I_element006]
  conduct = 2
  density = 1
  expand = 3
  formula = G4_POTASSIUM_IODIDE
  name = G4_POTASSIUM_IODIDE
  specific = 4
FEATURE [App::DocumentObjectGroupPython] K_element009  label="K_element : 2"  # scripted group (container) (typed FeaturePython)
  n = 2
  ref = K_element
FEATURE [App::DocumentObjectGroupPython] O_element085  label="O_element : 046"  # scripted group (container) (typed FeaturePython)
  n = 1
  ref = O_element
FEATURE [App::DocumentObjectGroupPython] G4_POTASSIUM_OXIDE  # scripted group (container) (typed FeaturePython)
  Dunit = g/cm3
  Dvalue = 2.32
  Group = -> [K_element009,O_element085]
  conduct = 2
  density = 1
  expand = 3
  formula = G4_POTASSIUM_OXIDE
  name = G4_POTASSIUM_OXIDE
  specific = 4
FEATURE [App::DocumentObjectGroupPython] C_element096  label="C_element : 054"  # scripted group (container) (typed FeaturePython)
  n = 3
  ref = C_element
FEATURE [App::DocumentObjectGroupPython] H_element088  label="H_element : 049"  # scripted group (container) (typed FeaturePython)
  n = 8
  ref = H_element
FEATURE [App::DocumentObjectGroupPython] G4_PROPANE  # scripted group (container) (typed FeaturePython)
  Dunit = g/cm3
  Dvalue = 0.00187939
  Group = -> [C_element096,H_element088]
  conduct = 2
  density = 1
  expand = 3
  formula = G4_PROPANE
  name = G4_PROPANE
  specific = 4
FEATURE [App::DocumentObjectGroupPython] C_element097  label="C_element : 055"  # scripted group (container) (typed FeaturePython)
  n = 3
  ref = C_element
FEATURE [App::DocumentObjectGroupPython] H_element089  label="H_element : 050"  # scripted group (container) (typed FeaturePython)
  n = 8
  ref = H_element
FEATURE [App::DocumentObjectGroupPython] G4_lPROPANE  # scripted group (container) (typed FeaturePython)
  Dunit = g/cm3
  Dvalue = 0.43
  Group = -> [C_element097,H_element089]
  conduct = 2
  density = 1
  expand = 3
  formula = G4_lPROPANE
  name = G4_lPROPANE
  specific = 4
FEATURE [App::DocumentObjectGroupPython] C_element098  label="C_element : 056"  # scripted group (container) (typed FeaturePython)
  n = 3
  ref = C_element
FEATURE [App::DocumentObjectGroupPython] H_element090  label="H_element : 051"  # scripted group (container) (typed FeaturePython)
  n = 8
  ref = H_element
FEATURE [App::DocumentObjectGroupPython] O_element086  label="O_element : 047"  # scripted group (container) (typed FeaturePython)
  n = 1
  ref = O_element
FEATURE [App::DocumentObjectGroupPython] G4_N_PROPYL_ALCOHOL  label="G4_N-PROPYL_ALCOHOL"  # scripted group (container) (typed FeaturePython)
  Dunit = g/cm3
  Dvalue = 0.8035
  Group = -> [C_element098,H_element090,O_element086]
  conduct = 2
  density = 1
  expand = 3
  formula = G4_N-PROPYL_ALCOHOL
  name = G4_N-PROPYL_ALCOHOL
  specific = 4
FEATURE [App::DocumentObjectGroupPython] C_element099  label="C_element : 057"  # scripted group (container) (typed FeaturePython)
  n = 5
  ref = C_element
FEATURE [App::DocumentObjectGroupPython] H_element091  label="H_element : 052"  # scripted group (container) (typed FeaturePython)
  n = 5
  ref = H_element
FEATURE [App::DocumentObjectGroupPython] N_element038  label="N_element : 017"  # scripted group (container) (typed FeaturePython)
  n = 1
  ref = N_element
FEATURE [App::DocumentObjectGroupPython] G4_PYRIDINE  # scripted group (container) (typed FeaturePython)
  Dunit = g/cm3
  Dvalue = 0.9819
  Group = -> [C_element099,H_element091,N_element038]
  conduct = 2
  density = 1
  expand = 3
  formula = G4_PYRIDINE
  name = G4_PYRIDINE
  specific = 4
FEATURE [App::DocumentObjectGroupPython] H_element092  label="H_element : 0.144"  # scripted group (container) (typed FeaturePython)
  n = 0.143711
FEATURE [App::DocumentObjectGroupPython] C_element100  label="C_element : 0.856"  # scripted group (container) (typed FeaturePython)
  n = 0.856289
FEATURE [App::DocumentObjectGroupPython] G4_RUBBER_BUTYL  # scripted group (container) (typed FeaturePython)
  Dunit = g/cm3
  Dvalue = 0.92
  Group = -> [H_element092,C_element100]
  conduct = 2
  density = 1
  expand = 3
  formula = G4_RUBBER_BUTYL
  name = G4_RUBBER_BUTYL
  specific = 4
FEATURE [App::DocumentObjectGroupPython] H_element093  label="H_element : 0.118"  # scripted group (container) (typed FeaturePython)
  n = 0.118371
FEATURE [App::DocumentObjectGroupPython] C_element101  label="C_element : 0.882"  # scripted group (container) (typed FeaturePython)
  n = 0.881629
FEATURE [App::DocumentObjectGroupPython] G4_RUBBER_NATURAL  # scripted group (container) (typed FeaturePython)
  Dunit = g/cm3
  Dvalue = 0.92
  Group = -> [H_element093,C_element101]
  conduct = 2
  density = 1
  expand = 3
  formula = G4_RUBBER_NATURAL
  name = G4_RUBBER_NATURAL
  specific = 4
FEATURE [App::DocumentObjectGroupPython] H_element094  label="H_element : 0.145"  # scripted group (container) (typed FeaturePython)
  n = 0.05692
FEATURE [App::DocumentObjectGroupPython] C_element102  label="C_element : 0.543"  # scripted group (container) (typed FeaturePython)
  n = 0.542646
FEATURE [App::DocumentObjectGroupPython] Cl_element021  label="Cl_element : 0.400"  # scripted group (container) (typed FeaturePython)
  n = 0.400434
FEATURE [App::DocumentObjectGroupPython] G4_RUBBER_NEOPRENE  # scripted group (container) (typed FeaturePython)
  Dunit = g/cm3
  Dvalue = 1.23
  Group = -> [H_element094,C_element102,Cl_element021]
  conduct = 2
  density = 1
  expand = 3
  formula = G4_RUBBER_NEOPRENE
  name = G4_RUBBER_NEOPRENE
  specific = 4
FEATURE [App::DocumentObjectGroupPython] Si_element006  label="Si_element : 1"  # scripted group (container) (typed FeaturePython)
  n = 1
  ref = Si_element
FEATURE [App::DocumentObjectGroupPython] O_element087  label="O_element : 048"  # scripted group (container) (typed FeaturePython)
  n = 2
  ref = O_element
FEATURE [App::DocumentObjectGroupPython] G4_SILICON_DIOXIDE  # scripted group (container) (typed FeaturePython)
  Dunit = g/cm3
  Dvalue = 2.32
  Group = -> [Si_element006,O_element087]
  conduct = 2
  density = 1
  expand = 3
  formula = G4_SILICON_DIOXIDE
  name = G4_SILICON_DIOXIDE
  specific = 4
FEATURE [App::DocumentObjectGroupPython] Ag_element002  label="Ag_element : 1"  # scripted group (container) (typed FeaturePython)
  n = 1
  ref = Ag_element
FEATURE [App::DocumentObjectGroupPython] Br_element005  label="Br_element : 003"  # scripted group (container) (typed FeaturePython)
  n = 1
  ref = Br_element
FEATURE [App::DocumentObjectGroupPython] G4_SILVER_BROMIDE  # scripted group (container) (typed FeaturePython)
  Dunit = g/cm3
  Dvalue = 6.473
  Group = -> [Ag_element002,Br_element005]
  conduct = 2
  density = 1
  expand = 3
  formula = G4_SILVER_BROMIDE
  name = G4_SILVER_BROMIDE
  specific = 4
FEATURE [App::DocumentObjectGroupPython] Ag_element003  label="Ag_element : 002"  # scripted group (container) (typed FeaturePython)
  n = 1
  ref = Ag_element
FEATURE [App::DocumentObjectGroupPython] Cl_element022  label="Cl_element : 011"  # scripted group (container) (typed FeaturePython)
  n = 1
  ref = Cl_element
FEATURE [App::DocumentObjectGroupPython] G4_SILVER_CHLORIDE  # scripted group (container) (typed FeaturePython)
  Dunit = g/cm3
  Dvalue = 5.56
  Group = -> [Ag_element003,Cl_element022]
  conduct = 2
  density = 1
  expand = 3
  formula = G4_SILVER_CHLORIDE
  name = G4_SILVER_CHLORIDE
  specific = 4
FEATURE [App::DocumentObjectGroupPython] Br_element006  label="Br_element : 0.423"  # scripted group (container) (typed FeaturePython)
  n = 0.422895
FEATURE [App::DocumentObjectGroupPython] Ag_element004  label="Ag_element : 0.574"  # scripted group (container) (typed FeaturePython)
  n = 0.573748
FEATURE [App::DocumentObjectGroupPython] I_element007  label="I_element : 0.649"  # scripted group (container) (typed FeaturePython)
  n = 0.003357
FEATURE [App::DocumentObjectGroupPython] G4_SILVER_HALIDES  # scripted group (container) (typed FeaturePython)
  Dunit = g/cm3
  Dvalue = 6.47
  Group = -> [Br_element006,Ag_element004,I_element007]
  conduct = 2
  density = 1
  expand = 3
  formula = G4_SILVER_HALIDES
  name = G4_SILVER_HALIDES
  specific = 4
FEATURE [App::DocumentObjectGroupPython] Ag_element005  label="Ag_element : 003"  # scripted group (container) (typed FeaturePython)
  n = 1
  ref = Ag_element
FEATURE [App::DocumentObjectGroupPython] I_element008  label="I_element : 004"  # scripted group (container) (typed FeaturePython)
  n = 1
  ref = I_element
FEATURE [App::DocumentObjectGroupPython] G4_SILVER_IODIDE  # scripted group (container) (typed FeaturePython)
  Dunit = g/cm3
  Dvalue = 6.01
  Group = -> [Ag_element005,I_element008]
  conduct = 2
  density = 1
  expand = 3
  formula = G4_SILVER_IODIDE
  name = G4_SILVER_IODIDE
  specific = 4
FEATURE [App::DocumentObjectGroupPython] H_element095  label="H_element : 0.100"  # scripted group (container) (typed FeaturePython)
  n = 0.1
FEATURE [App::DocumentObjectGroupPython] C_element103  label="C_element : 0.204"  # scripted group (container) (typed FeaturePython)
  n = 0.204
FEATURE [App::DocumentObjectGroupPython] N_element039  label="N_element : 0.759"  # scripted group (container) (typed FeaturePython)
  n = 0.042
FEATURE [App::DocumentObjectGroupPython] O_element088  label="O_element : 0.645"  # scripted group (container) (typed FeaturePython)
  n = 0.645
FEATURE [App::DocumentObjectGroupPython] Na_element013  label="Na_element : 0.100"  # scripted group (container) (typed FeaturePython)
  n = 0.002
FEATURE [App::DocumentObjectGroupPython] P_element009  label="P_element : 0.107"  # scripted group (container) (typed FeaturePython)
  n = 0.001
FEATURE [App::DocumentObjectGroupPython] S_element020  label="S_element : 0.021"  # scripted group (container) (typed FeaturePython)
  n = 0.002
FEATURE [App::DocumentObjectGroupPython] Cl_element023  label="Cl_element : 0.590"  # scripted group (container) (typed FeaturePython)
  n = 0.003
FEATURE [App::DocumentObjectGroupPython] K_element010  label="K_element : 0.001"  # scripted group (container) (typed FeaturePython)
  n = 0.001
FEATURE [App::DocumentObjectGroupPython] G4_SKIN_ICRP  # scripted group (container) (typed FeaturePython)
  Dunit = g/cm3
  Dvalue = 1.09
  Group = -> [H_element095,C_element103,N_element039,O_element088,Na_element013,P_element009,S_element020,Cl_element023,K_element010]
  conduct = 2
  density = 1
  expand = 3
  formula = G4_SKIN_ICRP
  name = G4_SKIN_ICRP
  specific = 4
FEATURE [App::DocumentObjectGroupPython] Na_element014  label="Na_element : 2"  # scripted group (container) (typed FeaturePython)
  n = 2
  ref = Na_element
FEATURE [App::DocumentObjectGroupPython] C_element104  label="C_element : 058"  # scripted group (container) (typed FeaturePython)
  n = 1
  ref = C_element
FEATURE [App::DocumentObjectGroupPython] O_element089  label="O_element : 049"  # scripted group (container) (typed FeaturePython)
  n = 3
  ref = O_element
FEATURE [App::DocumentObjectGroupPython] G4_SODIUM_CARBONATE  # scripted group (container) (typed FeaturePython)
  Dunit = g/cm3
  Dvalue = 2.532
  Group = -> [Na_element014,C_element104,O_element089]
  conduct = 2
  density = 1
  expand = 3
  formula = G4_SODIUM_CARBONATE
  name = G4_SODIUM_CARBONATE
  specific = 4
FEATURE [App::DocumentObjectGroupPython] Na_element015  label="Na_element : 1"  # scripted group (container) (typed FeaturePython)
  n = 1
  ref = Na_element
FEATURE [App::DocumentObjectGroupPython] I_element009  label="I_element : 005"  # scripted group (container) (typed FeaturePython)
  n = 1
  ref = I_element
FEATURE [App::DocumentObjectGroupPython] G4_SODIUM_IODIDE  # scripted group (container) (typed FeaturePython)
  Dunit = g/cm3
  Dvalue = 3.667
  Group = -> [Na_element015,I_element009]
  conduct = 2
  density = 1
  expand = 3
  formula = G4_SODIUM_IODIDE
  name = G4_SODIUM_IODIDE
  specific = 4
FEATURE [App::DocumentObjectGroupPython] Na_element016  label="Na_element : 003"  # scripted group (container) (typed FeaturePython)
  n = 2
  ref = Na_element
FEATURE [App::DocumentObjectGroupPython] O_element090  label="O_element : 050"  # scripted group (container) (typed FeaturePython)
  n = 1
  ref = O_element
FEATURE [App::DocumentObjectGroupPython] G4_SODIUM_MONOXIDE  # scripted group (container) (typed FeaturePython)
  Dunit = g/cm3
  Dvalue = 2.27
  Group = -> [Na_element016,O_element090]
  conduct = 2
  density = 1
  expand = 3
  formula = G4_SODIUM_MONOXIDE
  name = G4_SODIUM_MONOXIDE
  specific = 4
FEATURE [App::DocumentObjectGroupPython] Na_element017  label="Na_element : 004"  # scripted group (container) (typed FeaturePython)
  n = 1
  ref = Na_element
FEATURE [App::DocumentObjectGroupPython] N_element040  label="N_element : 018"  # scripted group (container) (typed FeaturePython)
  n = 1
  ref = N_element
FEATURE [App::DocumentObjectGroupPython] O_element091  label="O_element : 051"  # scripted group (container) (typed FeaturePython)
  n = 3
  ref = O_element
FEATURE [App::DocumentObjectGroupPython] G4_SODIUM_NITRATE  # scripted group (container) (typed FeaturePython)
  Dunit = g/cm3
  Dvalue = 2.261
  Group = -> [Na_element017,N_element040,O_element091]
  conduct = 2
  density = 1
  expand = 3
  formula = G4_SODIUM_NITRATE
  name = G4_SODIUM_NITRATE
  specific = 4
FEATURE [App::DocumentObjectGroupPython] C_element105  label="C_element : 059"  # scripted group (container) (typed FeaturePython)
  n = 14
  ref = C_element
FEATURE [App::DocumentObjectGroupPython] H_element096  label="H_element : 053"  # scripted group (container) (typed FeaturePython)
  n = 12
  ref = H_element
FEATURE [App::DocumentObjectGroupPython] G4_STILBENE  # scripted group (container) (typed FeaturePython)
  Dunit = g/cm3
  Dvalue = 0.9707
  Group = -> [C_element105,H_element096]
  conduct = 2
  density = 1
  expand = 3
  formula = G4_STILBENE
  name = G4_STILBENE
  specific = 4
FEATURE [App::DocumentObjectGroupPython] C_element106  label="C_element : 12"  # scripted group (container) (typed FeaturePython)
  n = 12
  ref = C_element
FEATURE [App::DocumentObjectGroupPython] H_element097  label="H_element : 22"  # scripted group (container) (typed FeaturePython)
  n = 22
  ref = H_element
FEATURE [App::DocumentObjectGroupPython] O_element092  label="O_element : 11"  # scripted group (container) (typed FeaturePython)
  n = 11
  ref = O_element
FEATURE [App::DocumentObjectGroupPython] G4_SUCROSE  # scripted group (container) (typed FeaturePython)
  Dunit = g/cm3
  Dvalue = 1.5805
  Group = -> [C_element106,H_element097,O_element092]
  conduct = 2
  density = 1
  expand = 3
  formula = G4_SUCROSE
  name = G4_SUCROSE
  specific = 4
FEATURE [App::DocumentObjectGroupPython] C_element107  label="C_element : 18"  # scripted group (container) (typed FeaturePython)
  n = 18
  ref = C_element
FEATURE [App::DocumentObjectGroupPython] H_element098  label="H_element : 054"  # scripted group (container) (typed FeaturePython)
  n = 14
  ref = H_element
FEATURE [App::DocumentObjectGroupPython] G4_TERPHENYL  # scripted group (container) (typed FeaturePython)
  Dunit = g/cm3
  Dvalue = 1.24
  Group = -> [C_element107,H_element098]
  conduct = 2
  density = 1
  expand = 3
  formula = G4_TERPHENYL
  name = G4_TERPHENYL
  specific = 4
FEATURE [App::DocumentObjectGroupPython] H_element099  label="H_element : 0.146"  # scripted group (container) (typed FeaturePython)
  n = 0.106
FEATURE [App::DocumentObjectGroupPython] C_element108  label="C_element : 0.883"  # scripted group (container) (typed FeaturePython)
  n = 0.099
FEATURE [App::DocumentObjectGroupPython] N_element041  label="N_element : 0.020"  # scripted group (container) (typed FeaturePython)
  n = 0.02
FEATURE [App::DocumentObjectGroupPython] O_element093  label="O_element : 0.766"  # scripted group (container) (typed FeaturePython)
  n = 0.766
FEATURE [App::DocumentObjectGroupPython] Na_element018  label="Na_element : 0.101"  # scripted group (container) (typed FeaturePython)
  n = 0.002
FEATURE [App::DocumentObjectGroupPython] P_element010  label="P_element : 0.108"  # scripted group (container) (typed FeaturePython)
  n = 0.001
FEATURE [App::DocumentObjectGroupPython] S_element021  label="S_element : 0.022"  # scripted group (container) (typed FeaturePython)
  n = 0.002
FEATURE [App::DocumentObjectGroupPython] Cl_element024  label="Cl_element : 0.002"  # scripted group (container) (typed FeaturePython)
  n = 0.002
FEATURE [App::DocumentObjectGroupPython] K_element011  label="K_element : 0.017"  # scripted group (container) (typed FeaturePython)
  n = 0.002
FEATURE [App::DocumentObjectGroupPython] G4_TESTIS_ICRP  # scripted group (container) (typed FeaturePython)
  Dunit = g/cm3
  Dvalue = 1.04
  Group = -> [H_element099,C_element108,N_element041,O_element093,Na_element018,P_element010,S_element021,Cl_element024,K_element011]
  conduct = 2
  density = 1
  expand = 3
  formula = G4_TESTIS_ICRP
  name = G4_TESTIS_ICRP
  specific = 4
FEATURE [App::DocumentObjectGroupPython] C_element109  label="C_element : 060"  # scripted group (container) (typed FeaturePython)
  n = 2
  ref = C_element
FEATURE [App::DocumentObjectGroupPython] Cl_element025  label="Cl_element : 012"  # scripted group (container) (typed FeaturePython)
  n = 4
  ref = Cl_element
FEATURE [App::DocumentObjectGroupPython] G4_TETRACHLOROETHYLENE  # scripted group (container) (typed FeaturePython)
  Dunit = g/cm3
  Dvalue = 1.625
  Group = -> [C_element109,Cl_element025]
  conduct = 2
  density = 1
  expand = 3
  formula = G4_TETRACHLOROETHYLENE
  name = G4_TETRACHLOROETHYLENE
  specific = 4
FEATURE [App::DocumentObjectGroupPython] Tl_element001  label="Tl_element : 1"  # scripted group (container) (typed FeaturePython)
  n = 1
  ref = Tl_element
FEATURE [App::DocumentObjectGroupPython] Cl_element026  label="Cl_element : 013"  # scripted group (container) (typed FeaturePython)
  n = 1
  ref = Cl_element
FEATURE [App::DocumentObjectGroupPython] G4_THALLIUM_CHLORIDE  # scripted group (container) (typed FeaturePython)
  Dunit = g/cm3
  Dvalue = 7.004
  Group = -> [Tl_element001,Cl_element026]
  conduct = 2
  density = 1
  expand = 3
  formula = G4_THALLIUM_CHLORIDE
  name = G4_THALLIUM_CHLORIDE
  specific = 4
FEATURE [App::DocumentObjectGroupPython] H_element100  label="H_element : 0.147"  # scripted group (container) (typed FeaturePython)
  n = 0.105
FEATURE [App::DocumentObjectGroupPython] C_element110  label="C_element : 0.256"  # scripted group (container) (typed FeaturePython)
  n = 0.256
FEATURE [App::DocumentObjectGroupPython] N_element042  label="N_element : 0.760"  # scripted group (container) (typed FeaturePython)
  n = 0.027
FEATURE [App::DocumentObjectGroupPython] O_element094  label="O_element : 0.602"  # scripted group (container) (typed FeaturePython)
  n = 0.602
FEATURE [App::DocumentObjectGroupPython] Na_element019  label="Na_element : 0.102"  # scripted group (container) (typed FeaturePython)
  n = 0.001
FEATURE [App::DocumentObjectGroupPython] P_element011  label="P_element : 0.109"  # scripted group (container) (typed FeaturePython)
  n = 0.002
FEATURE [App::DocumentObjectGroupPython] S_element022  label="S_element : 0.023"  # scripted group (container) (typed FeaturePython)
  n = 0.003
FEATURE [App::DocumentObjectGroupPython] Cl_element027  label="Cl_element : 0.591"  # scripted group (container) (typed FeaturePython)
  n = 0.002
FEATURE [App::DocumentObjectGroupPython] K_element012  label="K_element : 0.018"  # scripted group (container) (typed FeaturePython)
  n = 0.002
FEATURE [App::DocumentObjectGroupPython] G4_TISSUE_SOFT_ICRP  # scripted group (container) (typed FeaturePython)
  Dunit = g/cm3
  Dvalue = 1.03
  Group = -> [H_element100,C_element110,N_element042,O_element094,Na_element019,P_element011,S_element022,Cl_element027,K_element012]
  conduct = 2
  density = 1
  expand = 3
  formula = G4_TISSUE_SOFT_ICRP
  name = G4_TISSUE_SOFT_ICRP
  specific = 4
FEATURE [App::DocumentObjectGroupPython] H_element101  label="H_element : 0.148"  # scripted group (container) (typed FeaturePython)
  n = 0.101
FEATURE [App::DocumentObjectGroupPython] C_element111  label="C_element : 0.111"  # scripted group (container) (typed FeaturePython)
  n = 0.111
FEATURE [App::DocumentObjectGroupPython] N_element043  label="N_element : 0.026"  # scripted group (container) (typed FeaturePython)
  n = 0.026
FEATURE [App::DocumentObjectGroupPython] O_element095  label="O_element : 0.762"  # scripted group (container) (typed FeaturePython)
  n = 0.762
FEATURE [App::DocumentObjectGroupPython] G4_TISSUE_SOFT_ICRU_4  label="G4_TISSUE_SOFT_ICRU-4"  # scripted group (container) (typed FeaturePython)
  Dunit = g/cm3
  Dvalue = 1
  Group = -> [H_element101,C_element111,N_element043,O_element095]
  conduct = 2
  density = 1
  expand = 3
  formula = G4_TISSUE_SOFT_ICRU-4
  name = G4_TISSUE_SOFT_ICRU-4
  specific = 4
FEATURE [App::DocumentObjectGroupPython] H_element102  label="H_element : 0.149"  # scripted group (container) (typed FeaturePython)
  n = 0.101869
FEATURE [App::DocumentObjectGroupPython] C_element112  label="C_element : 0.456"  # scripted group (container) (typed FeaturePython)
  n = 0.456179
FEATURE [App::DocumentObjectGroupPython] N_element044  label="N_element : 0.761"  # scripted group (container) (typed FeaturePython)
  n = 0.035172
FEATURE [App::DocumentObjectGroupPython] O_element096  label="O_element : 0.407"  # scripted group (container) (typed FeaturePython)
  n = 0.40678
FEATURE [App::DocumentObjectGroupPython] G4_TISSUE_METHANE  label="G4_TISSUE-METHANE"  # scripted group (container) (typed FeaturePython)
  Dunit = g/cm3
  Dvalue = 0.00106409
  Group = -> [H_element102,C_element112,N_element044,O_element096]
  conduct = 2
  density = 1
  expand = 3
  formula = G4_TISSUE-METHANE
  name = G4_TISSUE-METHANE
  specific = 4
FEATURE [App::DocumentObjectGroupPython] H_element103  label="H_element : 0.103"  # scripted group (container) (typed FeaturePython)
  n = 0.102672
FEATURE [App::DocumentObjectGroupPython] C_element113  label="C_element : 0.569"  # scripted group (container) (typed FeaturePython)
  n = 0.56894
FEATURE [App::DocumentObjectGroupPython] N_element045  label="N_element : 0.762"  # scripted group (container) (typed FeaturePython)
  n = 0.035022
FEATURE [App::DocumentObjectGroupPython] O_element097  label="O_element : 0.293"  # scripted group (container) (typed FeaturePython)
  n = 0.293366
FEATURE [App::DocumentObjectGroupPython] G4_TISSUE_PROPANE  label="G4_TISSUE-PROPANE"  # scripted group (container) (typed FeaturePython)
  Dunit = g/cm3
  Dvalue = 0.00182628
  Group = -> [H_element103,C_element113,N_element045,O_element097]
  conduct = 2
  density = 1
  expand = 3
  formula = G4_TISSUE-PROPANE
  name = G4_TISSUE-PROPANE
  specific = 4
FEATURE [App::DocumentObjectGroupPython] Ti_element003  label="Ti_element : 1"  # scripted group (container) (typed FeaturePython)
  n = 1
  ref = Ti_element
FEATURE [App::DocumentObjectGroupPython] O_element098  label="O_element : 052"  # scripted group (container) (typed FeaturePython)
  n = 2
  ref = O_element
FEATURE [App::DocumentObjectGroupPython] G4_TITANIUM_DIOXIDE  # scripted group (container) (typed FeaturePython)
  Dunit = g/cm3
  Dvalue = 4.26
  Group = -> [Ti_element003,O_element098]
  conduct = 2
  density = 1
  expand = 3
  formula = G4_TITANIUM_DIOXIDE
  name = G4_TITANIUM_DIOXIDE
  specific = 4
FEATURE [App::DocumentObjectGroupPython] C_element114  label="C_element : 061"  # scripted group (container) (typed FeaturePython)
  n = 7
  ref = C_element
FEATURE [App::DocumentObjectGroupPython] H_element104  label="H_element : 055"  # scripted group (container) (typed FeaturePython)
  n = 8
  ref = H_element
FEATURE [App::DocumentObjectGroupPython] G4_TOLUENE  # scripted group (container) (typed FeaturePython)
  Dunit = g/cm3
  Dvalue = 0.8669
  Group = -> [C_element114,H_element104]
  conduct = 2
  density = 1
  expand = 3
  formula = G4_TOLUENE
  name = G4_TOLUENE
  specific = 4
FEATURE [App::DocumentObjectGroupPython] C_element115  label="C_element : 062"  # scripted group (container) (typed FeaturePython)
  n = 2
  ref = C_element
FEATURE [App::DocumentObjectGroupPython] H_element105  label="H_element : 056"  # scripted group (container) (typed FeaturePython)
  n = 1
  ref = H_element
FEATURE [App::DocumentObjectGroupPython] Cl_element028  label="Cl_element : 014"  # scripted group (container) (typed FeaturePython)
  n = 3
  ref = Cl_element
FEATURE [App::DocumentObjectGroupPython] G4_TRICHLOROETHYLENE  # scripted group (container) (typed FeaturePython)
  Dunit = g/cm3
  Dvalue = 1.46
  Group = -> [C_element115,H_element105,Cl_element028]
  conduct = 2
  density = 1
  expand = 3
  formula = G4_TRICHLOROETHYLENE
  name = G4_TRICHLOROETHYLENE
  specific = 4
FEATURE [App::DocumentObjectGroupPython] C_element116  label="C_element : 063"  # scripted group (container) (typed FeaturePython)
  n = 6
  ref = C_element
FEATURE [App::DocumentObjectGroupPython] H_element106  label="H_element : 15"  # scripted group (container) (typed FeaturePython)
  n = 15
  ref = H_element
FEATURE [App::DocumentObjectGroupPython] O_element099  label="O_element : 053"  # scripted group (container) (typed FeaturePython)
  n = 4
  ref = O_element
FEATURE [App::DocumentObjectGroupPython] P_element012  label="P_element : 1"  # scripted group (container) (typed FeaturePython)
  n = 1
  ref = P_element
FEATURE [App::DocumentObjectGroupPython] G4_TRIETHYL_PHOSPHATE  # scripted group (container) (typed FeaturePython)
  Dunit = g/cm3
  Dvalue = 1.07
  Group = -> [C_element116,H_element106,O_element099,P_element012]
  conduct = 2
  density = 1
  expand = 3
  formula = G4_TRIETHYL_PHOSPHATE
  name = G4_TRIETHYL_PHOSPHATE
  specific = 4
FEATURE [App::DocumentObjectGroupPython] W_element003  label="W_element : 003"  # scripted group (container) (typed FeaturePython)
  n = 1
  ref = W_element
FEATURE [App::DocumentObjectGroupPython] F_element017  label="F_element : 6"  # scripted group (container) (typed FeaturePython)
  n = 6
  ref = F_element
FEATURE [App::DocumentObjectGroupPython] G4_TUNGSTEN_HEXAFLUORIDE  # scripted group (container) (typed FeaturePython)
  Dunit = g/cm3
  Dvalue = 2.4
  Group = -> [W_element003,F_element017]
  conduct = 2
  density = 1
  expand = 3
  formula = G4_TUNGSTEN_HEXAFLUORIDE
  name = G4_TUNGSTEN_HEXAFLUORIDE
  specific = 4
FEATURE [App::DocumentObjectGroupPython] U_element001  label="U_element : 1"  # scripted group (container) (typed FeaturePython)
  n = 1
  ref = U_element
FEATURE [App::DocumentObjectGroupPython] C_element117  label="C_element : 064"  # scripted group (container) (typed FeaturePython)
  n = 2
  ref = C_element
FEATURE [App::DocumentObjectGroupPython] G4_URANIUM_DICARBIDE  # scripted group (container) (typed FeaturePython)
  Dunit = g/cm3
  Dvalue = 11.28
  Group = -> [U_element001,C_element117]
  conduct = 2
  density = 1
  expand = 3
  formula = G4_URANIUM_DICARBIDE
  name = G4_URANIUM_DICARBIDE
  specific = 4
FEATURE [App::DocumentObjectGroupPython] U_element002  label="U_element : 002"  # scripted group (container) (typed FeaturePython)
  n = 1
  ref = U_element
FEATURE [App::DocumentObjectGroupPython] C_element118  label="C_element : 065"  # scripted group (container) (typed FeaturePython)
  n = 1
  ref = C_element
FEATURE [App::DocumentObjectGroupPython] G4_URANIUM_MONOCARBIDE  # scripted group (container) (typed FeaturePython)
  Dunit = g/cm3
  Dvalue = 13.63
  Group = -> [U_element002,C_element118]
  conduct = 2
  density = 1
  expand = 3
  formula = G4_URANIUM_MONOCARBIDE
  name = G4_URANIUM_MONOCARBIDE
  specific = 4
FEATURE [App::DocumentObjectGroupPython] U_element003  label="U_element : 003"  # scripted group (container) (typed FeaturePython)
  n = 1
  ref = U_element
FEATURE [App::DocumentObjectGroupPython] O_element100  label="O_element : 054"  # scripted group (container) (typed FeaturePython)
  n = 2
  ref = O_element
FEATURE [App::DocumentObjectGroupPython] G4_URANIUM_OXIDE  # scripted group (container) (typed FeaturePython)
  Dunit = g/cm3
  Dvalue = 10.96
  Group = -> [U_element003,O_element100]
  conduct = 2
  density = 1
  expand = 3
  formula = G4_URANIUM_OXIDE
  name = G4_URANIUM_OXIDE
  specific = 4
FEATURE [App::DocumentObjectGroupPython] C_element119  label="C_element : 066"  # scripted group (container) (typed FeaturePython)
  n = 1
  ref = C_element
FEATURE [App::DocumentObjectGroupPython] H_element107  label="H_element : 057"  # scripted group (container) (typed FeaturePython)
  n = 4
  ref = H_element
FEATURE [App::DocumentObjectGroupPython] N_element046  label="N_element : 019"  # scripted group (container) (typed FeaturePython)
  n = 2
  ref = N_element
FEATURE [App::DocumentObjectGroupPython] O_element101  label="O_element : 055"  # scripted group (container) (typed FeaturePython)
  n = 1
  ref = O_element
FEATURE [App::DocumentObjectGroupPython] G4_UREA  # scripted group (container) (typed FeaturePython)
  Dunit = g/cm3
  Dvalue = 1.323
  Group = -> [C_element119,H_element107,N_element046,O_element101]
  conduct = 2
  density = 1
  expand = 3
  formula = G4_UREA
  name = G4_UREA
  specific = 4
FEATURE [App::DocumentObjectGroupPython] C_element120  label="C_element : 067"  # scripted group (container) (typed FeaturePython)
  n = 5
  ref = C_element
FEATURE [App::DocumentObjectGroupPython] H_element108  label="H_element : 058"  # scripted group (container) (typed FeaturePython)
  n = 11
  ref = H_element
FEATURE [App::DocumentObjectGroupPython] N_element047  label="N_element : 020"  # scripted group (container) (typed FeaturePython)
  n = 1
  ref = N_element
FEATURE [App::DocumentObjectGroupPython] O_element102  label="O_element : 056"  # scripted group (container) (typed FeaturePython)
  n = 2
  ref = O_element
FEATURE [App::DocumentObjectGroupPython] G4_VALINE  # scripted group (container) (typed FeaturePython)
  Dunit = g/cm3
  Dvalue = 1.23
  Group = -> [C_element120,H_element108,N_element047,O_element102]
  conduct = 2
  density = 1
  expand = 3
  formula = G4_VALINE
  name = G4_VALINE
  specific = 4
FEATURE [App::DocumentObjectGroupPython] H_element109  label="H_element : 0.009"  # scripted group (container) (typed FeaturePython)
  n = 0.009417
FEATURE [App::DocumentObjectGroupPython] C_element121  label="C_element : 0.281"  # scripted group (container) (typed FeaturePython)
  n = 0.280555
FEATURE [App::DocumentObjectGroupPython] F_element018  label="F_element : 0.710"  # scripted group (container) (typed FeaturePython)
  n = 0.710028
FEATURE [App::DocumentObjectGroupPython] G4_VITON  # scripted group (container) (typed FeaturePython)
  Dunit = g/cm3
  Dvalue = 1.8
  Group = -> [H_element109,C_element121,F_element018]
  conduct = 2
  density = 1
  expand = 3
  formula = G4_VITON
  name = G4_VITON
  specific = 4
FEATURE [App::DocumentObjectGroupPython] H_element110  label="H_element : 059"  # scripted group (container) (typed FeaturePython)
  n = 2
  ref = H_element
FEATURE [App::DocumentObjectGroupPython] O_element103  label="O_element : 057"  # scripted group (container) (typed FeaturePython)
  n = 1
  ref = O_element
FEATURE [App::DocumentObjectGroupPython] G4_WATER  # scripted group (container) (typed FeaturePython)
  Dunit = g/cm3
  Dvalue = 1
  Group = -> [H_element110,O_element103]
  conduct = 2
  density = 1
  expand = 3
  formula = G4_WATER
  name = G4_WATER
  specific = 4
FEATURE [App::DocumentObjectGroupPython] H_element111  label="H_element : 060"  # scripted group (container) (typed FeaturePython)
  n = 2
  ref = H_element
FEATURE [App::DocumentObjectGroupPython] O_element104  label="O_element : 058"  # scripted group (container) (typed FeaturePython)
  n = 1
  ref = O_element
FEATURE [App::DocumentObjectGroupPython] G4_WATER_VAPOR  # scripted group (container) (typed FeaturePython)
  Dunit = g/cm3
  Dvalue = 0.000756182
  Group = -> [H_element111,O_element104]
  conduct = 2
  density = 1
  expand = 3
  formula = G4_WATER_VAPOR
  name = G4_WATER_VAPOR
  specific = 4
FEATURE [App::DocumentObjectGroupPython] C_element122  label="C_element : 068"  # scripted group (container) (typed FeaturePython)
  n = 8
  ref = C_element
FEATURE [App::DocumentObjectGroupPython] H_element112  label="H_element : 061"  # scripted group (container) (typed FeaturePython)
  n = 10
  ref = H_element
FEATURE [App::DocumentObjectGroupPython] G4_XYLENE  # scripted group (container) (typed FeaturePython)
  Dunit = g/cm3
  Dvalue = 0.87
  Group = -> [C_element122,H_element112]
  conduct = 2
  density = 1
  expand = 3
  formula = G4_XYLENE
  name = G4_XYLENE
  specific = 4
FEATURE [App::DocumentObjectGroupPython] C_element123  label="C_element : 069"  # scripted group (container) (typed FeaturePython)
  n = 1
  ref = C_element
FEATURE [App::DocumentObjectGroupPython] G4_GRAPHITE  # scripted group (container) (typed FeaturePython)
  Dunit = g/cm3
  Dvalue = 2.21
  Group = -> [C_element123]
  conduct = 2
  density = 1
  expand = 3
  formula = G4_GRAPHITE
  name = G4_GRAPHITE
  specific = 4
FEATURE [App::DocumentObjectGroupPython] NIST  # scripted group (container) (typed FeaturePython)
  Group = -> [G4_A_150_TISSUE,G4_ACETONE,G4_ACETYLENE,G4_ADENINE,G4_ADIPOSE_TISSUE_ICRP,G4_AIR,G4_ALANINE,G4_ALUMINUM_OXIDE,G4_AMBER,G4_AMMONIA,G4_ANILINE,G4_ANTHRACENE,G4_B_100_BONE,G4_BAKELITE,G4_BARIUM_FLUORIDE,G4_BARIUM_SULFATE,G4_BENZENE,G4_BERYLLIUM_OXIDE,G4_BGO,G4_BLOOD_ICRP,G4_BONE_COMPACT_ICRU,G4_BONE_CORTICAL_ICRP,G4_BORON_CARBIDE,G4_BORON_OXIDE,G4_BRAIN_ICRP,G4_BUTANE,G4_N_BUTYL_ALCOHOL,G4_C_552,+152 more]
FEATURE [App::DocumentObjectGroupPython] H_element113  label="H_element : 062"  # scripted group (container) (typed FeaturePython)
  n = 1
  ref = H_element
FEATURE [App::DocumentObjectGroupPython] G4_H  # scripted group (container) (typed FeaturePython)
  Dunit = g/cm3
  Dvalue = 8.3748e-05
  Group = -> [H_element113]
  conduct = 2
  density = 1
  expand = 3
  formula = H
  name = G4_H
  specific = 4
FEATURE [App::DocumentObjectGroupPython] He_element001  label="He_element : 1"  # scripted group (container) (typed FeaturePython)
  n = 1
  ref = He_element
FEATURE [App::DocumentObjectGroupPython] G4_He  # scripted group (container) (typed FeaturePython)
  Dunit = g/cm3
  Dvalue = 0.000166322
  Group = -> [He_element001]
  conduct = 2
  density = 1
  expand = 3
  formula = He
  name = G4_He
  specific = 4
FEATURE [App::DocumentObjectGroupPython] Li_element008  label="Li_element : 008"  # scripted group (container) (typed FeaturePython)
  n = 1
  ref = Li_element
FEATURE [App::DocumentObjectGroupPython] G4_Li  # scripted group (container) (typed FeaturePython)
  Dunit = g/cm3
  Dvalue = 0.534
  Group = -> [Li_element008]
  conduct = 2
  density = 1
  expand = 3
  formula = Li
  name = G4_Li
  specific = 4
FEATURE [App::DocumentObjectGroupPython] Be_element002  label="Be_element : 002"  # scripted group (container) (typed FeaturePython)
  n = 1
  ref = Be_element
FEATURE [App::DocumentObjectGroupPython] G4_Be  # scripted group (container) (typed FeaturePython)
  Dunit = g/cm3
  Dvalue = 1.848
  Group = -> [Be_element002]
  conduct = 2
  density = 1
  expand = 3
  formula = Be
  name = G4_Be
  specific = 4
FEATURE [App::DocumentObjectGroupPython] B_element007  label="B_element : 007"  # scripted group (container) (typed FeaturePython)
  n = 1
  ref = B_element
FEATURE [App::DocumentObjectGroupPython] G4_B  # scripted group (container) (typed FeaturePython)
  Dunit = g/cm3
  Dvalue = 2.37
  Group = -> [B_element007]
  conduct = 2
  density = 1
  expand = 3
  formula = B
  name = G4_B
  specific = 4
FEATURE [App::DocumentObjectGroupPython] C_element124  label="C_element : 070"  # scripted group (container) (typed FeaturePython)
  n = 1
  ref = C_element
FEATURE [App::DocumentObjectGroupPython] G4_C  # scripted group (container) (typed FeaturePython)
  Dunit = g/cm3
  Dvalue = 2
  Group = -> [C_element124]
  conduct = 2
  density = 1
  expand = 3
  formula = C
  name = G4_C
  specific = 4
FEATURE [App::DocumentObjectGroupPython] N_element048  label="N_element : 021"  # scripted group (container) (typed FeaturePython)
  n = 1
  ref = N_element
FEATURE [App::DocumentObjectGroupPython] G4_N  # scripted group (container) (typed FeaturePython)
  Dunit = g/cm3
  Dvalue = 0.0011652
  Group = -> [N_element048]
  conduct = 2
  density = 1
  expand = 3
  formula = N
  name = G4_N
  specific = 4
FEATURE [App::DocumentObjectGroupPython] O_element105  label="O_element : 059"  # scripted group (container) (typed FeaturePython)
  n = 1
  ref = O_element
FEATURE [App::DocumentObjectGroupPython] G4_O  # scripted group (container) (typed FeaturePython)
  Dunit = g/cm3
  Dvalue = 0.00133151
  Group = -> [O_element105]
  conduct = 2
  density = 1
  expand = 3
  formula = O
  name = G4_O
  specific = 4
FEATURE [App::DocumentObjectGroupPython] F_element019  label="F_element : 008"  # scripted group (container) (typed FeaturePython)
  n = 1
  ref = F_element
FEATURE [App::DocumentObjectGroupPython] G4_F  # scripted group (container) (typed FeaturePython)
  Dunit = g/cm3
  Dvalue = 0.00158029
  Group = -> [F_element019]
  conduct = 2
  density = 1
  expand = 3
  formula = F
  name = G4_F
  specific = 4
FEATURE [App::DocumentObjectGroupPython] Ne_element001  label="Ne_element : 1"  # scripted group (container) (typed FeaturePython)
  n = 1
  ref = Ne_element
FEATURE [App::DocumentObjectGroupPython] G4_Ne  # scripted group (container) (typed FeaturePython)
  Dunit = g/cm3
  Dvalue = 0.000838505
  Group = -> [Ne_element001]
  conduct = 2
  density = 1
  expand = 3
  formula = Ne
  name = G4_Ne
  specific = 4
FEATURE [App::DocumentObjectGroupPython] Na_element020  label="Na_element : 005"  # scripted group (container) (typed FeaturePython)
  n = 1
  ref = Na_element
FEATURE [App::DocumentObjectGroupPython] G4_Na  # scripted group (container) (typed FeaturePython)
  Dunit = g/cm3
  Dvalue = 0.971
  Group = -> [Na_element020]
  conduct = 2
  density = 1
  expand = 3
  formula = Na
  name = G4_Na
  specific = 4
FEATURE [App::DocumentObjectGroupPython] Mg_element011  label="Mg_element : 005"  # scripted group (container) (typed FeaturePython)
  n = 1
  ref = Mg_element
FEATURE [App::DocumentObjectGroupPython] G4_Mg  # scripted group (container) (typed FeaturePython)
  Dunit = g/cm3
  Dvalue = 1.74
  Group = -> [Mg_element011]
  conduct = 2
  density = 1
  expand = 3
  formula = Mg
  name = G4_Mg
  specific = 4
FEATURE [App::DocumentObjectGroupPython] Al_element004  label="Al_element : 1"  # scripted group (container) (typed FeaturePython)
  n = 1
  ref = Al_element
FEATURE [App::DocumentObjectGroupPython] G4_Al  # scripted group (container) (typed FeaturePython)
  Dunit = g/cm3
  Dvalue = 2.699
  Group = -> [Al_element004]
  conduct = 2
  density = 1
  expand = 3
  formula = Al
  name = G4_Al
  specific = 4
FEATURE [App::DocumentObjectGroupPython] Si_element007  label="Si_element : 002"  # scripted group (container) (typed FeaturePython)
  n = 1
  ref = Si_element
FEATURE [App::DocumentObjectGroupPython] G4_Si  # scripted group (container) (typed FeaturePython)
  Dunit = g/cm3
  Dvalue = 2.33
  Group = -> [Si_element007]
  conduct = 2
  density = 1
  expand = 3
  formula = Si
  name = G4_Si
  specific = 4
FEATURE [App::DocumentObjectGroupPython] P_element013  label="P_element : 002"  # scripted group (container) (typed FeaturePython)
  n = 1
  ref = P_element
FEATURE [App::DocumentObjectGroupPython] G4_P  # scripted group (container) (typed FeaturePython)
  Dunit = g/cm3
  Dvalue = 2.2
  Group = -> [P_element013]
  conduct = 2
  density = 1
  expand = 3
  formula = P
  name = G4_P
  specific = 4
FEATURE [App::DocumentObjectGroupPython] S_element023  label="S_element : 007"  # scripted group (container) (typed FeaturePython)
  n = 1
  ref = S_element
FEATURE [App::DocumentObjectGroupPython] G4_S  # scripted group (container) (typed FeaturePython)
  Dunit = g/cm3
  Dvalue = 2
  Group = -> [S_element023]
  conduct = 2
  density = 1
  expand = 3
  formula = S
  name = G4_S
  specific = 4
FEATURE [App::DocumentObjectGroupPython] Cl_element029  label="Cl_element : 015"  # scripted group (container) (typed FeaturePython)
  n = 1
  ref = Cl_element
FEATURE [App::DocumentObjectGroupPython] G4_Cl  # scripted group (container) (typed FeaturePython)
  Dunit = g/cm3
  Dvalue = 0.00299473
  Group = -> [Cl_element029]
  conduct = 2
  density = 1
  expand = 3
  formula = Cl
  name = G4_Cl
  specific = 4
FEATURE [App::DocumentObjectGroupPython] Ar_element002  label="Ar_element : 1"  # scripted group (container) (typed FeaturePython)
  n = 1
  ref = Ar_element
FEATURE [App::DocumentObjectGroupPython] G4_Ar  # scripted group (container) (typed FeaturePython)
  Dunit = g/cm3
  Dvalue = 0.00166201
  Group = -> [Ar_element002]
  conduct = 2
  density = 1
  expand = 3
  formula = Ar
  name = G4_Ar
  specific = 4
FEATURE [App::DocumentObjectGroupPython] K_element013  label="K_element : 003"  # scripted group (container) (typed FeaturePython)
  n = 1
  ref = K_element
FEATURE [App::DocumentObjectGroupPython] G4_K  # scripted group (container) (typed FeaturePython)
  Dunit = g/cm3
  Dvalue = 0.862
  Group = -> [K_element013]
  conduct = 2
  density = 1
  expand = 3
  formula = K
  name = G4_K
  specific = 4
FEATURE [App::DocumentObjectGroupPython] Ca_element014  label="Ca_element : 007"  # scripted group (container) (typed FeaturePython)
  n = 1
  ref = Ca_element
FEATURE [App::DocumentObjectGroupPython] G4_Ca  # scripted group (container) (typed FeaturePython)
  Dunit = g/cm3
  Dvalue = 1.55
  Group = -> [Ca_element014]
  conduct = 2
  density = 1
  expand = 3
  formula = Ca
  name = G4_Ca
  specific = 4
FEATURE [App::DocumentObjectGroupPython] Sc_element001  label="Sc_element : 1"  # scripted group (container) (typed FeaturePython)
  n = 1
  ref = Sc_element
FEATURE [App::DocumentObjectGroupPython] G4_Sc  # scripted group (container) (typed FeaturePython)
  Dunit = g/cm3
  Dvalue = 2.989
  Group = -> [Sc_element001]
  conduct = 2
  density = 1
  expand = 3
  formula = Sc
  name = G4_Sc
  specific = 4
FEATURE [App::DocumentObjectGroupPython] Ti_element004  label="Ti_element : 002"  # scripted group (container) (typed FeaturePython)
  n = 1
  ref = Ti_element
FEATURE [App::DocumentObjectGroupPython] G4_Ti  # scripted group (container) (typed FeaturePython)
  Dunit = g/cm3
  Dvalue = 4.54
  Group = -> [Ti_element004]
  conduct = 2
  density = 1
  expand = 3
  formula = Ti
  name = G4_Ti
  specific = 4
FEATURE [App::DocumentObjectGroupPython] V_element001  label="V_element : 1"  # scripted group (container) (typed FeaturePython)
  n = 1
  ref = V_element
FEATURE [App::DocumentObjectGroupPython] G4_V  # scripted group (container) (typed FeaturePython)
  Dunit = g/cm3
  Dvalue = 6.11
  Group = -> [V_element001]
  conduct = 2
  density = 1
  expand = 3
  formula = V
  name = G4_V
  specific = 4
FEATURE [App::DocumentObjectGroupPython] Cr_element001  label="Cr_element : 1"  # scripted group (container) (typed FeaturePython)
  n = 1
  ref = Cr_element
FEATURE [App::DocumentObjectGroupPython] G4_Cr  # scripted group (container) (typed FeaturePython)
  Dunit = g/cm3
  Dvalue = 7.18
  Group = -> [Cr_element001]
  conduct = 2
  density = 1
  expand = 3
  formula = Cr
  name = G4_Cr
  specific = 4
FEATURE [App::DocumentObjectGroupPython] Mn_element001  label="Mn_element : 1"  # scripted group (container) (typed FeaturePython)
  n = 1
  ref = Mn_element
FEATURE [App::DocumentObjectGroupPython] G4_Mn  # scripted group (container) (typed FeaturePython)
  Dunit = g/cm3
  Dvalue = 7.44
  Group = -> [Mn_element001]
  conduct = 2
  density = 1
  expand = 3
  formula = Mn
  name = G4_Mn
  specific = 4
FEATURE [App::DocumentObjectGroupPython] Fe_element007  label="Fe_element : 004"  # scripted group (container) (typed FeaturePython)
  n = 1
  ref = Fe_element
FEATURE [App::DocumentObjectGroupPython] G4_Fe  # scripted group (container) (typed FeaturePython)
  Dunit = g/cm3
  Dvalue = 7.874
  Group = -> [Fe_element007]
  conduct = 2
  density = 1
  expand = 3
  formula = Fe
  name = G4_Fe
  specific = 4
FEATURE [App::DocumentObjectGroupPython] Co_element001  label="Co_element : 1"  # scripted group (container) (typed FeaturePython)
  n = 1
  ref = Co_element
FEATURE [App::DocumentObjectGroupPython] G4_Co  # scripted group (container) (typed FeaturePython)
  Dunit = g/cm3
  Dvalue = 8.9
  Group = -> [Co_element001]
  conduct = 2
  density = 1
  expand = 3
  formula = Co
  name = G4_Co
  specific = 4
FEATURE [App::DocumentObjectGroupPython] Ni_element001  label="Ni_element : 1"  # scripted group (container) (typed FeaturePython)
  n = 1
  ref = Ni_element
FEATURE [App::DocumentObjectGroupPython] G4_Ni  # scripted group (container) (typed FeaturePython)
  Dunit = g/cm3
  Dvalue = 8.902
  Group = -> [Ni_element001]
  conduct = 2
  density = 1
  expand = 3
  formula = Ni
  name = G4_Ni
  specific = 4
FEATURE [App::DocumentObjectGroupPython] Cu_element001  label="Cu_element : 1"  # scripted group (container) (typed FeaturePython)
  n = 1
  ref = Cu_element
FEATURE [App::DocumentObjectGroupPython] G4_Cu  # scripted group (container) (typed FeaturePython)
  Dunit = g/cm3
  Dvalue = 8.96
  Group = -> [Cu_element001]
  conduct = 2
  density = 1
  expand = 3
  formula = Cu
  name = G4_Cu
  specific = 4
FEATURE [App::DocumentObjectGroupPython] Zn_element001  label="Zn_element : 1"  # scripted group (container) (typed FeaturePython)
  n = 1
  ref = Zn_element
FEATURE [App::DocumentObjectGroupPython] G4_Zn  # scripted group (container) (typed FeaturePython)
  Dunit = g/cm3
  Dvalue = 7.133
  Group = -> [Zn_element001]
  conduct = 2
  density = 1
  expand = 3
  formula = Zn
  name = G4_Zn
  specific = 4
FEATURE [App::DocumentObjectGroupPython] Ga_element002  label="Ga_element : 002"  # scripted group (container) (typed FeaturePython)
  n = 1
  ref = Ga_element
FEATURE [App::DocumentObjectGroupPython] G4_Ga  # scripted group (container) (typed FeaturePython)
  Dunit = g/cm3
  Dvalue = 5.904
  Group = -> [Ga_element002]
  conduct = 2
  density = 1
  expand = 3
  formula = Ga
  name = G4_Ga
  specific = 4
FEATURE [App::DocumentObjectGroupPython] Ge_element002  label="Ge_element : 1"  # scripted group (container) (typed FeaturePython)
  n = 1
  ref = Ge_element
FEATURE [App::DocumentObjectGroupPython] G4_Ge  # scripted group (container) (typed FeaturePython)
  Dunit = g/cm3
  Dvalue = 5.323
  Group = -> [Ge_element002]
  conduct = 2
  density = 1
  expand = 3
  formula = Ge
  name = G4_Ge
  specific = 4
FEATURE [App::DocumentObjectGroupPython] As_element003  label="As_element : 002"  # scripted group (container) (typed FeaturePython)
  n = 1
  ref = As_element
FEATURE [App::DocumentObjectGroupPython] G4_As  # scripted group (container) (typed FeaturePython)
  Dunit = g/cm3
  Dvalue = 5.73
  Group = -> [As_element003]
  conduct = 2
  density = 1
  expand = 3
  formula = As
  name = G4_As
  specific = 4
FEATURE [App::DocumentObjectGroupPython] Se_element001  label="Se_element : 1"  # scripted group (container) (typed FeaturePython)
  n = 1
  ref = Se_element
FEATURE [App::DocumentObjectGroupPython] G4_Se  # scripted group (container) (typed FeaturePython)
  Dunit = g/cm3
  Dvalue = 4.5
  Group = -> [Se_element001]
  conduct = 2
  density = 1
  expand = 3
  formula = Se
  name = G4_Se
  specific = 4
FEATURE [App::DocumentObjectGroupPython] Br_element007  label="Br_element : 004"  # scripted group (container) (typed FeaturePython)
  n = 1
  ref = Br_element
FEATURE [App::DocumentObjectGroupPython] G4_Br  # scripted group (container) (typed FeaturePython)
  Dunit = g/cm3
  Dvalue = 0.0070721
  Group = -> [Br_element007]
  conduct = 2
  density = 1
  expand = 3
  formula = Br
  name = G4_Br
  specific = 4
FEATURE [App::DocumentObjectGroupPython] Kr_element001  label="Kr_element : 1"  # scripted group (container) (typed FeaturePython)
  n = 1
  ref = Kr_element
FEATURE [App::DocumentObjectGroupPython] G4_Kr  # scripted group (container) (typed FeaturePython)
  Dunit = g/cm3
  Dvalue = 0.00347832
  Group = -> [Kr_element001]
  conduct = 2
  density = 1
  expand = 3
  formula = Kr
  name = G4_Kr
  specific = 4
FEATURE [App::DocumentObjectGroupPython] Rb_element001  label="Rb_element : 1"  # scripted group (container) (typed FeaturePython)
  n = 1
  ref = Rb_element
FEATURE [App::DocumentObjectGroupPython] G4_Rb  # scripted group (container) (typed FeaturePython)
  Dunit = g/cm3
  Dvalue = 1.532
  Group = -> [Rb_element001]
  conduct = 2
  density = 1
  expand = 3
  formula = Rb
  name = G4_Rb
  specific = 4
FEATURE [App::DocumentObjectGroupPython] Sr_element001  label="Sr_element : 1"  # scripted group (container) (typed FeaturePython)
  n = 1
  ref = Sr_element
FEATURE [App::DocumentObjectGroupPython] G4_Sr  # scripted group (container) (typed FeaturePython)
  Dunit = g/cm3
  Dvalue = 2.54
  Group = -> [Sr_element001]
  conduct = 2
  density = 1
  expand = 3
  formula = Sr
  name = G4_Sr
  specific = 4
FEATURE [App::DocumentObjectGroupPython] Y_element001  label="Y_element : 1"  # scripted group (container) (typed FeaturePython)
  n = 1
  ref = Y_element
FEATURE [App::DocumentObjectGroupPython] G4_Y  # scripted group (container) (typed FeaturePython)
  Dunit = g/cm3
  Dvalue = 4.469
  Group = -> [Y_element001]
  conduct = 2
  density = 1
  expand = 3
  formula = Y
  name = G4_Y
  specific = 4
FEATURE [App::DocumentObjectGroupPython] Zr_element001  label="Zr_element : 1"  # scripted group (container) (typed FeaturePython)
  n = 1
  ref = Zr_element
FEATURE [App::DocumentObjectGroupPython] G4_Zr  # scripted group (container) (typed FeaturePython)
  Dunit = g/cm3
  Dvalue = 6.506
  Group = -> [Zr_element001]
  conduct = 2
  density = 1
  expand = 3
  formula = Zr
  name = G4_Zr
  specific = 4
FEATURE [App::DocumentObjectGroupPython] Nb_element001  label="Nb_element : 1"  # scripted group (container) (typed FeaturePython)
  n = 1
  ref = Nb_element
FEATURE [App::DocumentObjectGroupPython] G4_Nb  # scripted group (container) (typed FeaturePython)
  Dunit = g/cm3
  Dvalue = 8.57
  Group = -> [Nb_element001]
  conduct = 2
  density = 1
  expand = 3
  formula = Nb
  name = G4_Nb
  specific = 4
FEATURE [App::DocumentObjectGroupPython] Mo_element001  label="Mo_element : 1"  # scripted group (container) (typed FeaturePython)
  n = 1
  ref = Mo_element
FEATURE [App::DocumentObjectGroupPython] G4_Mo  # scripted group (container) (typed FeaturePython)
  Dunit = g/cm3
  Dvalue = 10.22
  Group = -> [Mo_element001]
  conduct = 2
  density = 1
  expand = 3
  formula = Mo
  name = G4_Mo
  specific = 4
FEATURE [App::DocumentObjectGroupPython] Tc_element001  label="Tc_element : 1"  # scripted group (container) (typed FeaturePython)
  n = 1
  ref = Tc_element
FEATURE [App::DocumentObjectGroupPython] G4_Tc  # scripted group (container) (typed FeaturePython)
  Dunit = g/cm3
  Dvalue = 11.5
  Group = -> [Tc_element001]
  conduct = 2
  density = 1
  expand = 3
  formula = Tc
  name = G4_Tc
  specific = 4
FEATURE [App::DocumentObjectGroupPython] Ru_element001  label="Ru_element : 1"  # scripted group (container) (typed FeaturePython)
  n = 1
  ref = Ru_element
FEATURE [App::DocumentObjectGroupPython] G4_Ru  # scripted group (container) (typed FeaturePython)
  Dunit = g/cm3
  Dvalue = 12.41
  Group = -> [Ru_element001]
  conduct = 2
  density = 1
  expand = 3
  formula = Ru
  name = G4_Ru
  specific = 4
FEATURE [App::DocumentObjectGroupPython] Rh_element001  label="Rh_element : 1"  # scripted group (container) (typed FeaturePython)
  n = 1
  ref = Rh_element
FEATURE [App::DocumentObjectGroupPython] G4_Rh  # scripted group (container) (typed FeaturePython)
  Dunit = g/cm3
  Dvalue = 12.41
  Group = -> [Rh_element001]
  conduct = 2
  density = 1
  expand = 3
  formula = Rh
  name = G4_Rh
  specific = 4
FEATURE [App::DocumentObjectGroupPython] Pd_element001  label="Pd_element : 1"  # scripted group (container) (typed FeaturePython)
  n = 1
  ref = Pd_element
FEATURE [App::DocumentObjectGroupPython] G4_Pd  # scripted group (container) (typed FeaturePython)
  Dunit = g/cm3
  Dvalue = 12.02
  Group = -> [Pd_element001]
  conduct = 2
  density = 1
  expand = 3
  formula = Pd
  name = G4_Pd
  specific = 4
FEATURE [App::DocumentObjectGroupPython] Ag_element006  label="Ag_element : 004"  # scripted group (container) (typed FeaturePython)
  n = 1
  ref = Ag_element
FEATURE [App::DocumentObjectGroupPython] G4_Ag  # scripted group (container) (typed FeaturePython)
  Dunit = g/cm3
  Dvalue = 10.5
  Group = -> [Ag_element006]
  conduct = 2
  density = 1
  expand = 3
  formula = Ag
  name = G4_Ag
  specific = 4
FEATURE [App::DocumentObjectGroupPython] Cd_element003  label="Cd_element : 003"  # scripted group (container) (typed FeaturePython)
  n = 1
  ref = Cd_element
FEATURE [App::DocumentObjectGroupPython] G4_Cd  # scripted group (container) (typed FeaturePython)
  Dunit = g/cm3
  Dvalue = 8.65
  Group = -> [Cd_element003]
  conduct = 2
  density = 1
  expand = 3
  formula = Cd
  name = G4_Cd
  specific = 4
FEATURE [App::DocumentObjectGroupPython] In_element001  label="In_element : 1"  # scripted group (container) (typed FeaturePython)
  n = 1
  ref = In_element
FEATURE [App::DocumentObjectGroupPython] G4_In  # scripted group (container) (typed FeaturePython)
  Dunit = g/cm3
  Dvalue = 7.31
  Group = -> [In_element001]
  conduct = 2
  density = 1
  expand = 3
  formula = In
  name = G4_In
  specific = 4
FEATURE [App::DocumentObjectGroupPython] Sn_element001  label="Sn_element : 1"  # scripted group (container) (typed FeaturePython)
  n = 1
  ref = Sn_element
FEATURE [App::DocumentObjectGroupPython] G4_Sn  # scripted group (container) (typed FeaturePython)
  Dunit = g/cm3
  Dvalue = 7.31
  Group = -> [Sn_element001]
  conduct = 2
  density = 1
  expand = 3
  formula = Sn
  name = G4_Sn
  specific = 4
FEATURE [App::DocumentObjectGroupPython] Sb_element001  label="Sb_element : 1"  # scripted group (container) (typed FeaturePython)
  n = 1
  ref = Sb_element
FEATURE [App::DocumentObjectGroupPython] G4_Sb  # scripted group (container) (typed FeaturePython)
  Dunit = g/cm3
  Dvalue = 6.691
  Group = -> [Sb_element001]
  conduct = 2
  density = 1
  expand = 3
  formula = Sb
  name = G4_Sb
  specific = 4
FEATURE [App::DocumentObjectGroupPython] Te_element002  label="Te_element : 002"  # scripted group (container) (typed FeaturePython)
  n = 1
  ref = Te_element
FEATURE [App::DocumentObjectGroupPython] G4_Te  # scripted group (container) (typed FeaturePython)
  Dunit = g/cm3
  Dvalue = 6.24
  Group = -> [Te_element002]
  conduct = 2
  density = 1
  expand = 3
  formula = Te
  name = G4_Te
  specific = 4
FEATURE [App::DocumentObjectGroupPython] I_element010  label="I_element : 006"  # scripted group (container) (typed FeaturePython)
  n = 1
  ref = I_element
FEATURE [App::DocumentObjectGroupPython] G4_I  # scripted group (container) (typed FeaturePython)
  Dunit = g/cm3
  Dvalue = 4.93
  Group = -> [I_element010]
  conduct = 2
  density = 1
  expand = 3
  formula = I
  name = G4_I
  specific = 4
FEATURE [App::DocumentObjectGroupPython] Xe_element001  label="Xe_element : 1"  # scripted group (container) (typed FeaturePython)
  n = 1
  ref = Xe_element
FEATURE [App::DocumentObjectGroupPython] G4_Xe  # scripted group (container) (typed FeaturePython)
  Dunit = g/cm3
  Dvalue = 0.00548536
  Group = -> [Xe_element001]
  conduct = 2
  density = 1
  expand = 3
  formula = Xe
  name = G4_Xe
  specific = 4
FEATURE [App::DocumentObjectGroupPython] Cs_element003  label="Cs_element : 003"  # scripted group (container) (typed FeaturePython)
  n = 1
  ref = Cs_element
FEATURE [App::DocumentObjectGroupPython] G4_Cs  # scripted group (container) (typed FeaturePython)
  Dunit = g/cm3
  Dvalue = 1.873
  Group = -> [Cs_element003]
  conduct = 2
  density = 1
  expand = 3
  formula = Cs
  name = G4_Cs
  specific = 4
FEATURE [App::DocumentObjectGroupPython] Ba_element003  label="Ba_element : 003"  # scripted group (container) (typed FeaturePython)
  n = 1
  ref = Ba_element
FEATURE [App::DocumentObjectGroupPython] G4_Ba  # scripted group (container) (typed FeaturePython)
  Dunit = g/cm3
  Dvalue = 3.5
  Group = -> [Ba_element003]
  conduct = 2
  density = 1
  expand = 3
  formula = Ba
  name = G4_Ba
  specific = 4
FEATURE [App::DocumentObjectGroupPython] La_element003  label="La_element : 003"  # scripted group (container) (typed FeaturePython)
  n = 1
  ref = La_element
FEATURE [App::DocumentObjectGroupPython] G4_La  # scripted group (container) (typed FeaturePython)
  Dunit = g/cm3
  Dvalue = 6.154
  Group = -> [La_element003]
  conduct = 2
  density = 1
  expand = 3
  formula = La
  name = G4_La
  specific = 4
FEATURE [App::DocumentObjectGroupPython] Ce_element002  label="Ce_element : 1"  # scripted group (container) (typed FeaturePython)
  n = 1
  ref = Ce_element
FEATURE [App::DocumentObjectGroupPython] G4_Ce  # scripted group (container) (typed FeaturePython)
  Dunit = g/cm3
  Dvalue = 6.657
  Group = -> [Ce_element002]
  conduct = 2
  density = 1
  expand = 3
  formula = Ce
  name = G4_Ce
  specific = 4
FEATURE [App::DocumentObjectGroupPython] Pr_element001  label="Pr_element : 1"  # scripted group (container) (typed FeaturePython)
  n = 1
  ref = Pr_element
FEATURE [App::DocumentObjectGroupPython] G4_Pr  # scripted group (container) (typed FeaturePython)
  Dunit = g/cm3
  Dvalue = 6.71
  Group = -> [Pr_element001]
  conduct = 2
  density = 1
  expand = 3
  formula = Pr
  name = G4_Pr
  specific = 4
FEATURE [App::DocumentObjectGroupPython] Nd_element001  label="Nd_element : 1"  # scripted group (container) (typed FeaturePython)
  n = 1
  ref = Nd_element
FEATURE [App::DocumentObjectGroupPython] G4_Nd  # scripted group (container) (typed FeaturePython)
  Dunit = g/cm3
  Dvalue = 6.9
  Group = -> [Nd_element001]
  conduct = 2
  density = 1
  expand = 3
  formula = Nd
  name = G4_Nd
  specific = 4
FEATURE [App::DocumentObjectGroupPython] Pm_element001  label="Pm_element : 1"  # scripted group (container) (typed FeaturePython)
  n = 1
  ref = Pm_element
FEATURE [App::DocumentObjectGroupPython] G4_Pm  # scripted group (container) (typed FeaturePython)
  Dunit = g/cm3
  Dvalue = 7.22
  Group = -> [Pm_element001]
  conduct = 2
  density = 1
  expand = 3
  formula = Pm
  name = G4_Pm
  specific = 4
FEATURE [App::DocumentObjectGroupPython] Sm_element001  label="Sm_element : 1"  # scripted group (container) (typed FeaturePython)
  n = 1
  ref = Sm_element
FEATURE [App::DocumentObjectGroupPython] G4_Sm  # scripted group (container) (typed FeaturePython)
  Dunit = g/cm3
  Dvalue = 7.46
  Group = -> [Sm_element001]
  conduct = 2
  density = 1
  expand = 3
  formula = Sm
  name = G4_Sm
  specific = 4
FEATURE [App::DocumentObjectGroupPython] Eu_element001  label="Eu_element : 1"  # scripted group (container) (typed FeaturePython)
  n = 1
  ref = Eu_element
FEATURE [App::DocumentObjectGroupPython] G4_Eu  # scripted group (container) (typed FeaturePython)
  Dunit = g/cm3
  Dvalue = 5.243
  Group = -> [Eu_element001]
  conduct = 2
  density = 1
  expand = 3
  formula = Eu
  name = G4_Eu
  specific = 4
FEATURE [App::DocumentObjectGroupPython] Gd_element002  label="Gd_element : 1"  # scripted group (container) (typed FeaturePython)
  n = 1
  ref = Gd_element
FEATURE [App::DocumentObjectGroupPython] G4_Gd  # scripted group (container) (typed FeaturePython)
  Dunit = g/cm3
  Dvalue = 7.9004
  Group = -> [Gd_element002]
  conduct = 2
  density = 1
  expand = 3
  formula = Gd
  name = G4_Gd
  specific = 4
FEATURE [App::DocumentObjectGroupPython] Tb_element001  label="Tb_element : 1"  # scripted group (container) (typed FeaturePython)
  n = 1
  ref = Tb_element
FEATURE [App::DocumentObjectGroupPython] G4_Tb  # scripted group (container) (typed FeaturePython)
  Dunit = g/cm3
  Dvalue = 8.229
  Group = -> [Tb_element001]
  conduct = 2
  density = 1
  expand = 3
  formula = Tb
  name = G4_Tb
  specific = 4
FEATURE [App::DocumentObjectGroupPython] Dy_element001  label="Dy_element : 1"  # scripted group (container) (typed FeaturePython)
  n = 1
  ref = Dy_element
FEATURE [App::DocumentObjectGroupPython] G4_Dy  # scripted group (container) (typed FeaturePython)
  Dunit = g/cm3
  Dvalue = 8.55
  Group = -> [Dy_element001]
  conduct = 2
  density = 1
  expand = 3
  formula = Dy
  name = G4_Dy
  specific = 4
FEATURE [App::DocumentObjectGroupPython] Ho_element001  label="Ho_element : 1"  # scripted group (container) (typed FeaturePython)
  n = 1
  ref = Ho_element
FEATURE [App::DocumentObjectGroupPython] G4_Ho  # scripted group (container) (typed FeaturePython)
  Dunit = g/cm3
  Dvalue = 8.795
  Group = -> [Ho_element001]
  conduct = 2
  density = 1
  expand = 3
  formula = Ho
  name = G4_Ho
  specific = 4
FEATURE [App::DocumentObjectGroupPython] Er_element001  label="Er_element : 1"  # scripted group (container) (typed FeaturePython)
  n = 1
  ref = Er_element
FEATURE [App::DocumentObjectGroupPython] G4_Er  # scripted group (container) (typed FeaturePython)
  Dunit = g/cm3
  Dvalue = 9.066
  Group = -> [Er_element001]
  conduct = 2
  density = 1
  expand = 3
  formula = Er
  name = G4_Er
  specific = 4
FEATURE [App::DocumentObjectGroupPython] Tm_element001  label="Tm_element : 1"  # scripted group (container) (typed FeaturePython)
  n = 1
  ref = Tm_element
FEATURE [App::DocumentObjectGroupPython] G4_Tm  # scripted group (container) (typed FeaturePython)
  Dunit = g/cm3
  Dvalue = 9.321
  Group = -> [Tm_element001]
  conduct = 2
  density = 1
  expand = 3
  formula = Tm
  name = G4_Tm
  specific = 4
FEATURE [App::DocumentObjectGroupPython] Yb_element001  label="Yb_element : 1"  # scripted group (container) (typed FeaturePython)
  n = 1
  ref = Yb_element
FEATURE [App::DocumentObjectGroupPython] G4_Yb  # scripted group (container) (typed FeaturePython)
  Dunit = g/cm3
  Dvalue = 6.73
  Group = -> [Yb_element001]
  conduct = 2
  density = 1
  expand = 3
  formula = Yb
  name = G4_Yb
  specific = 4
FEATURE [App::DocumentObjectGroupPython] Lu_element001  label="Lu_element : 1"  # scripted group (container) (typed FeaturePython)
  n = 1
  ref = Lu_element
FEATURE [App::DocumentObjectGroupPython] G4_Lu  # scripted group (container) (typed FeaturePython)
  Dunit = g/cm3
  Dvalue = 9.84
  Group = -> [Lu_element001]
  conduct = 2
  density = 1
  expand = 3
  formula = Lu
  name = G4_Lu
  specific = 4
FEATURE [App::DocumentObjectGroupPython] Hf_element001  label="Hf_element : 1"  # scripted group (container) (typed FeaturePython)
  n = 1
  ref = Hf_element
FEATURE [App::DocumentObjectGroupPython] G4_Hf  # scripted group (container) (typed FeaturePython)
  Dunit = g/cm3
  Dvalue = 13.31
  Group = -> [Hf_element001]
  conduct = 2
  density = 1
  expand = 3
  formula = Hf
  name = G4_Hf
  specific = 4
FEATURE [App::DocumentObjectGroupPython] Ta_element001  label="Ta_element : 1"  # scripted group (container) (typed FeaturePython)
  n = 1
  ref = Ta_element
FEATURE [App::DocumentObjectGroupPython] G4_Ta  # scripted group (container) (typed FeaturePython)
  Dunit = g/cm3
  Dvalue = 16.654
  Group = -> [Ta_element001]
  conduct = 2
  density = 1
  expand = 3
  formula = Ta
  name = G4_Ta
  specific = 4
FEATURE [App::DocumentObjectGroupPython] W_element004  label="W_element : 004"  # scripted group (container) (typed FeaturePython)
  n = 1
  ref = W_element
FEATURE [App::DocumentObjectGroupPython] G4_W  # scripted group (container) (typed FeaturePython)
  Dunit = g/cm3
  Dvalue = 19.3
  Group = -> [W_element004]
  conduct = 2
  density = 1
  expand = 3
  formula = W
  name = G4_W
  specific = 4
FEATURE [App::DocumentObjectGroupPython] Re_element001  label="Re_element : 1"  # scripted group (container) (typed FeaturePython)
  n = 1
  ref = Re_element
FEATURE [App::DocumentObjectGroupPython] G4_Re  # scripted group (container) (typed FeaturePython)
  Dunit = g/cm3
  Dvalue = 21.02
  Group = -> [Re_element001]
  conduct = 2
  density = 1
  expand = 3
  formula = Re
  name = G4_Re
  specific = 4
FEATURE [App::DocumentObjectGroupPython] Os_element001  label="Os_element : 1"  # scripted group (container) (typed FeaturePython)
  n = 1
  ref = Os_element
FEATURE [App::DocumentObjectGroupPython] G4_Os  # scripted group (container) (typed FeaturePython)
  Dunit = g/cm3
  Dvalue = 22.57
  Group = -> [Os_element001]
  conduct = 2
  density = 1
  expand = 3
  formula = Os
  name = G4_Os
  specific = 4
FEATURE [App::DocumentObjectGroupPython] Ir_element001  label="Ir_element : 1"  # scripted group (container) (typed FeaturePython)
  n = 1
  ref = Ir_element
FEATURE [App::DocumentObjectGroupPython] G4_Ir  # scripted group (container) (typed FeaturePython)
  Dunit = g/cm3
  Dvalue = 22.42
  Group = -> [Ir_element001]
  conduct = 2
  density = 1
  expand = 3
  formula = Ir
  name = G4_Ir
  specific = 4
FEATURE [App::DocumentObjectGroupPython] Pt_element001  label="Pt_element : 1"  # scripted group (container) (typed FeaturePython)
  n = 1
  ref = Pt_element
FEATURE [App::DocumentObjectGroupPython] G4_Pt  # scripted group (container) (typed FeaturePython)
  Dunit = g/cm3
  Dvalue = 21.45
  Group = -> [Pt_element001]
  conduct = 2
  density = 1
  expand = 3
  formula = Pt
  name = G4_Pt
  specific = 4
FEATURE [App::DocumentObjectGroupPython] Au_element001  label="Au_element : 1"  # scripted group (container) (typed FeaturePython)
  n = 1
  ref = Au_element
FEATURE [App::DocumentObjectGroupPython] G4_Au  # scripted group (container) (typed FeaturePython)
  Dunit = g/cm3
  Dvalue = 19.32
  Group = -> [Au_element001]
  conduct = 2
  density = 1
  expand = 3
  formula = Au
  name = G4_Au
  specific = 4
FEATURE [App::DocumentObjectGroupPython] Hg_element002  label="Hg_element : 002"  # scripted group (container) (typed FeaturePython)
  n = 1
  ref = Hg_element
FEATURE [App::DocumentObjectGroupPython] G4_Hg  # scripted group (container) (typed FeaturePython)
  Dunit = g/cm3
  Dvalue = 13.546
  Group = -> [Hg_element002]
  conduct = 2
  density = 1
  expand = 3
  formula = Hg
  name = G4_Hg
  specific = 4
FEATURE [App::DocumentObjectGroupPython] Tl_element002  label="Tl_element : 002"  # scripted group (container) (typed FeaturePython)
  n = 1
  ref = Tl_element
FEATURE [App::DocumentObjectGroupPython] G4_Tl  # scripted group (container) (typed FeaturePython)
  Dunit = g/cm3
  Dvalue = 11.72
  Group = -> [Tl_element002]
  conduct = 2
  density = 1
  expand = 3
  formula = Tl
  name = G4_Tl
  specific = 4
FEATURE [App::DocumentObjectGroupPython] Pb_element003  label="Pb_element : 1"  # scripted group (container) (typed FeaturePython)
  n = 1
  ref = Pb_element
FEATURE [App::DocumentObjectGroupPython] G4_Pb  # scripted group (container) (typed FeaturePython)
  Dunit = g/cm3
  Dvalue = 11.35
  Group = -> [Pb_element003]
  conduct = 2
  density = 1
  expand = 3
  formula = Pb
  name = G4_Pb
  specific = 4
FEATURE [App::DocumentObjectGroupPython] Bi_element002  label="Bi_element : 1"  # scripted group (container) (typed FeaturePython)
  n = 1
  ref = Bi_element
FEATURE [App::DocumentObjectGroupPython] G4_Bi  # scripted group (container) (typed FeaturePython)
  Dunit = g/cm3
  Dvalue = 9.747
  Group = -> [Bi_element002]
  conduct = 2
  density = 1
  expand = 3
  formula = Bi
  name = G4_Bi
  specific = 4
FEATURE [App::DocumentObjectGroupPython] Po_element001  label="Po_element : 1"  # scripted group (container) (typed FeaturePython)
  n = 1
  ref = Po_element
FEATURE [App::DocumentObjectGroupPython] G4_Po  # scripted group (container) (typed FeaturePython)
  Dunit = g/cm3
  Dvalue = 9.32
  Group = -> [Po_element001]
  conduct = 2
  density = 1
  expand = 3
  formula = Po
  name = G4_Po
  specific = 4
FEATURE [App::DocumentObjectGroupPython] At_element001  label="At_element : 1"  # scripted group (container) (typed FeaturePython)
  n = 1
  ref = At_element
FEATURE [App::DocumentObjectGroupPython] G4_At  # scripted group (container) (typed FeaturePython)
  Dunit = g/cm3
  Dvalue = 9.32
  Group = -> [At_element001]
  conduct = 2
  density = 1
  expand = 3
  formula = At
  name = G4_At
  specific = 4
FEATURE [App::DocumentObjectGroupPython] Rn_element001  label="Rn_element : 1"  # scripted group (container) (typed FeaturePython)
  n = 1
  ref = Rn_element
FEATURE [App::DocumentObjectGroupPython] G4_Rn  # scripted group (container) (typed FeaturePython)
  Dunit = g/cm3
  Dvalue = 0.00900662
  Group = -> [Rn_element001]
  conduct = 2
  density = 1
  expand = 3
  formula = Rn
  name = G4_Rn
  specific = 4
FEATURE [App::DocumentObjectGroupPython] Fr_element001  label="Fr_element : 1"  # scripted group (container) (typed FeaturePython)
  n = 1
  ref = Fr_element
FEATURE [App::DocumentObjectGroupPython] G4_Fr  # scripted group (container) (typed FeaturePython)
  Dunit = g/cm3
  Dvalue = 1
  Group = -> [Fr_element001]
  conduct = 2
  density = 1
  expand = 3
  formula = Fr
  name = G4_Fr
  specific = 4
FEATURE [App::DocumentObjectGroupPython] Ra_element001  label="Ra_element : 1"  # scripted group (container) (typed FeaturePython)
  n = 1
  ref = Ra_element
FEATURE [App::DocumentObjectGroupPython] G4_Ra  # scripted group (container) (typed FeaturePython)
  Dunit = g/cm3
  Dvalue = 5
  Group = -> [Ra_element001]
  conduct = 2
  density = 1
  expand = 3
  formula = Ra
  name = G4_Ra
  specific = 4
FEATURE [App::DocumentObjectGroupPython] Ac_element001  label="Ac_element : 1"  # scripted group (container) (typed FeaturePython)
  n = 1
  ref = Ac_element
FEATURE [App::DocumentObjectGroupPython] G4_Ac  # scripted group (container) (typed FeaturePython)
  Dunit = g/cm3
  Dvalue = 10.07
  Group = -> [Ac_element001]
  conduct = 2
  density = 1
  expand = 3
  formula = Ac
  name = G4_Ac
  specific = 4
FEATURE [App::DocumentObjectGroupPython] Th_element001  label="Th_element : 1"  # scripted group (container) (typed FeaturePython)
  n = 1
  ref = Th_element
FEATURE [App::DocumentObjectGroupPython] G4_Th  # scripted group (container) (typed FeaturePython)
  Dunit = g/cm3
  Dvalue = 11.72
  Group = -> [Th_element001]
  conduct = 2
  density = 1
  expand = 3
  formula = Th
  name = G4_Th
  specific = 4
FEATURE [App::DocumentObjectGroupPython] Pa_element001  label="Pa_element : 1"  # scripted group (container) (typed FeaturePython)
  n = 1
  ref = Pa_element
FEATURE [App::DocumentObjectGroupPython] G4_Pa  # scripted group (container) (typed FeaturePython)
  Dunit = g/cm3
  Dvalue = 15.37
  Group = -> [Pa_element001]
  conduct = 2
  density = 1
  expand = 3
  formula = Pa
  name = G4_Pa
  specific = 4
FEATURE [App::DocumentObjectGroupPython] U_element004  label="U_element : 004"  # scripted group (container) (typed FeaturePython)
  n = 1
  ref = U_element
FEATURE [App::DocumentObjectGroupPython] G4_U  # scripted group (container) (typed FeaturePython)
  Dunit = g/cm3
  Dvalue = 18.95
  Group = -> [U_element004]
  conduct = 2
  density = 1
  expand = 3
  formula = U
  name = G4_U
  specific = 4
FEATURE [App::DocumentObjectGroupPython] Np_element001  label="Np_element : 1"  # scripted group (container) (typed FeaturePython)
  n = 1
  ref = Np_element
FEATURE [App::DocumentObjectGroupPython] G4_Np  # scripted group (container) (typed FeaturePython)
  Dunit = g/cm3
  Dvalue = 20.25
  Group = -> [Np_element001]
  conduct = 2
  density = 1
  expand = 3
  formula = Np
  name = G4_Np
  specific = 4
FEATURE [App::DocumentObjectGroupPython] Pu_element002  label="Pu_element : 002"  # scripted group (container) (typed FeaturePython)
  n = 1
  ref = Pu_element
FEATURE [App::DocumentObjectGroupPython] G4_Pu  # scripted group (container) (typed FeaturePython)
  Dunit = g/cm3
  Dvalue = 19.84
  Group = -> [Pu_element002]
  conduct = 2
  density = 1
  expand = 3
  formula = Pu
  name = G4_Pu
  specific = 4
FEATURE [App::DocumentObjectGroupPython] Am_element001  label="Am_element : 1"  # scripted group (container) (typed FeaturePython)
  n = 1
  ref = Am_element
FEATURE [App::DocumentObjectGroupPython] G4_Am  # scripted group (container) (typed FeaturePython)
  Dunit = g/cm3
  Dvalue = 13.67
  Group = -> [Am_element001]
  conduct = 2
  density = 1
  expand = 3
  formula = Am
  name = G4_Am
  specific = 4
FEATURE [App::DocumentObjectGroupPython] Cm_element001  label="Cm_element : 1"  # scripted group (container) (typed FeaturePython)
  n = 1
  ref = Cm_element
FEATURE [App::DocumentObjectGroupPython] G4_Cm  # scripted group (container) (typed FeaturePython)
  Dunit = g/cm3
  Dvalue = 13.51
  Group = -> [Cm_element001]
  conduct = 2
  density = 1
  expand = 3
  formula = Cm
  name = G4_Cm
  specific = 4
FEATURE [App::DocumentObjectGroupPython] Bk_element001  label="Bk_element : 1"  # scripted group (container) (typed FeaturePython)
  n = 1
  ref = Bk_element
FEATURE [App::DocumentObjectGroupPython] G4_Bk  # scripted group (container) (typed FeaturePython)
  Dunit = g/cm3
  Dvalue = 14
  Group = -> [Bk_element001]
  conduct = 2
  density = 1
  expand = 3
  formula = Bk
  name = G4_Bk
  specific = 4
FEATURE [App::DocumentObjectGroupPython] Cf_element001  label="Cf_element : 1"  # scripted group (container) (typed FeaturePython)
  n = 1
  ref = Cf_element
FEATURE [App::DocumentObjectGroupPython] G4_Cf  # scripted group (container) (typed FeaturePython)
  Dunit = g/cm3
  Dvalue = 10
  Group = -> [Cf_element001]
  conduct = 2
  density = 1
  expand = 3
  formula = Cf
  name = G4_Cf
  specific = 4
FEATURE [App::DocumentObjectGroupPython] Element  # scripted group (container) (typed FeaturePython)
  Group = -> [G4_H,G4_He,G4_Li,G4_Be,G4_B,G4_C,G4_N,G4_O,G4_F,G4_Ne,G4_Na,G4_Mg,G4_Al,G4_Si,G4_P,G4_S,G4_Cl,G4_Ar,G4_K,G4_Ca,G4_Sc,G4_Ti,G4_V,G4_Cr,G4_Mn,G4_Fe,G4_Co,G4_Ni,G4_Cu,G4_Zn,G4_Ga,G4_Ge,G4_As,G4_Se,G4_Br,G4_Kr,G4_Rb,G4_Sr,G4_Y,G4_Zr,G4_Nb,G4_Mo,G4_Tc,G4_Ru,G4_Rh,G4_Pd,G4_Ag,G4_Cd,G4_In,G4_Sn,G4_Sb,G4_Te,G4_I,G4_Xe,G4_Cs,G4_Ba,G4_La,G4_Ce,G4_Pr,G4_Nd,G4_Pm,G4_Sm,G4_Eu,G4_Gd,G4_Tb,G4_Dy,G4_Ho,G4_Er,+30 more]
FEATURE [App::DocumentObjectGroupPython] H_element114  label="H_element : 063"  # scripted group (container) (typed FeaturePython)
  n = 2
  ref = H_element
FEATURE [App::DocumentObjectGroupPython] G4_lH2  # scripted group (container) (typed FeaturePython)
  Dunit = g/cm3
  Dvalue = 0.0708
  Group = -> [H_element114]
  conduct = 2
  density = 1
  expand = 3
  formula = G4_lH2
  name = G4_lH2
  specific = 4
FEATURE [App::DocumentObjectGroupPython] N_element049  label="N_element : 022"  # scripted group (container) (typed FeaturePython)
  n = 2
  ref = N_element
FEATURE [App::DocumentObjectGroupPython] G4_lN2  # scripted group (container) (typed FeaturePython)
  Dunit = g/cm3
  Dvalue = 0.807
  Group = -> [N_element049]
  conduct = 2
  density = 1
  expand = 3
  formula = G4_lN2
  name = G4_lN2
  specific = 4
FEATURE [App::DocumentObjectGroupPython] O_element106  label="O_element : 060"  # scripted group (container) (typed FeaturePython)
  n = 2
  ref = O_element
FEATURE [App::DocumentObjectGroupPython] G4_lO2  # scripted group (container) (typed FeaturePython)
  Dunit = g/cm3
  Dvalue = 1.141
  Group = -> [O_element106]
  conduct = 2
  density = 1
  expand = 3
  formula = G4_lO2
  name = G4_lO2
  specific = 4
FEATURE [App::DocumentObjectGroupPython] Ar  label="Ar : 1"  # scripted group (container) (typed FeaturePython)
  n = 1
  ref = Ar
FEATURE [App::DocumentObjectGroupPython] G4_lAr  # scripted group (container) (typed FeaturePython)
  Dunit = g/cm3
  Dvalue = 1.396
  Group = -> [Ar]
  conduct = 2
  density = 1
  expand = 3
  formula = G4_lAr
  name = G4_lAr
  specific = 4
FEATURE [App::DocumentObjectGroupPython] Br  label="Br : 1"  # scripted group (container) (typed FeaturePython)
  n = 1
  ref = Br
FEATURE [App::DocumentObjectGroupPython] G4_lBr  # scripted group (container) (typed FeaturePython)
  Dunit = g/cm3
  Dvalue = 3.1028
  Group = -> [Br]
  conduct = 2
  density = 1
  expand = 3
  formula = G4_lBr
  name = G4_lBr
  specific = 4
FEATURE [App::DocumentObjectGroupPython] Kr  label="Kr : 1"  # scripted group (container) (typed FeaturePython)
  n = 1
  ref = Kr
FEATURE [App::DocumentObjectGroupPython] G4_lKr  # scripted group (container) (typed FeaturePython)
  Dunit = g/cm3
  Dvalue = 2.418
  Group = -> [Kr]
  conduct = 2
  density = 1
  expand = 3
  formula = G4_lKr
  name = G4_lKr
  specific = 4
FEATURE [App::DocumentObjectGroupPython] Xe  label="Xe : 1"  # scripted group (container) (typed FeaturePython)
  n = 1
  ref = Xe
FEATURE [App::DocumentObjectGroupPython] G4_lXe  # scripted group (container) (typed FeaturePython)
  Dunit = g/cm3
  Dvalue = 2.953
  Group = -> [Xe]
  conduct = 2
  density = 1
  expand = 3
  formula = G4_lXe
  name = G4_lXe
  specific = 4
FEATURE [App::DocumentObjectGroupPython] O_element107  label="O_element : 061"  # scripted group (container) (typed FeaturePython)
  n = 4
  ref = O_element
FEATURE [App::DocumentObjectGroupPython] Pb_element004  label="Pb_element : 002"  # scripted group (container) (typed FeaturePython)
  n = 1
  ref = Pb_element
FEATURE [App::DocumentObjectGroupPython] W_element005  label="W_element : 005"  # scripted group (container) (typed FeaturePython)
  n = 1
  ref = W_element
FEATURE [App::DocumentObjectGroupPython] G4_PbWO4  # scripted group (container) (typed FeaturePython)
  Dunit = g/cm3
  Dvalue = 8.28
  Group = -> [O_element107,Pb_element004,W_element005]
  conduct = 2
  density = 1
  expand = 3
  formula = G4_PbWO4
  name = G4_PbWO4
  specific = 4
FEATURE [App::DocumentObjectGroupPython] alactic  label="alactic : 1"  # scripted group (container) (typed FeaturePython)
  n = 1
  ref = alactic
FEATURE [App::DocumentObjectGroupPython] G4_Galactic  # scripted group (container) (typed FeaturePython)
  Dunit = g/cm3
  Dvalue = 0
  Group = -> [alactic]
  conduct = 2
  density = 1
  expand = 3
  formula = G4_Galactic
  name = G4_Galactic
  specific = 4
FEATURE [App::DocumentObjectGroupPython] RAPHITE_POROUS  label="RAPHITE_POROUS : 1"  # scripted group (container) (typed FeaturePython)
  n = 1
  ref = RAPHITE_POROUS
FEATURE [App::DocumentObjectGroupPython] G4_GRAPHITE_POROUS  # scripted group (container) (typed FeaturePython)
  Dunit = g/cm3
  Dvalue = 1.7
  Group = -> [RAPHITE_POROUS]
  conduct = 2
  density = 1
  expand = 3
  formula = G4_GRAPHITE_POROUS
  name = G4_GRAPHITE_POROUS
  specific = 4
FEATURE [App::DocumentObjectGroupPython] H_element115  label="H_element : 0.150"  # scripted group (container) (typed FeaturePython)
  n = 0.080538
FEATURE [App::DocumentObjectGroupPython] C_element125  label="C_element : 0.600"  # scripted group (container) (typed FeaturePython)
  n = 0.599848
FEATURE [App::DocumentObjectGroupPython] O_element108  label="O_element : 0.320"  # scripted group (container) (typed FeaturePython)
  n = 0.319614
FEATURE [App::DocumentObjectGroupPython] G4_LUCITE  # scripted group (container) (typed FeaturePython)
  Dunit = g/cm3
  Dvalue = 1.19
  Group = -> [H_element115,C_element125,O_element108]
  conduct = 2
  density = 1
  expand = 3
  formula = G4_LUCITE
  name = G4_LUCITE
  specific = 4
FEATURE [App::DocumentObjectGroupPython] Cu_element002  label="Cu_element : 62"  # scripted group (container) (typed FeaturePython)
  n = 62
  ref = Cu_element
FEATURE [App::DocumentObjectGroupPython] Zn_element002  label="Zn_element : 35"  # scripted group (container) (typed FeaturePython)
  n = 35
  ref = Zn_element
FEATURE [App::DocumentObjectGroupPython] Pb_element005  label="Pb_element : 3"  # scripted group (container) (typed FeaturePython)
  n = 3
  ref = Pb_element
FEATURE [App::DocumentObjectGroupPython] G4_BRASS  # scripted group (container) (typed FeaturePython)
  Dunit = g/cm3
  Dvalue = 8.52
  Group = -> [Cu_element002,Zn_element002,Pb_element005]
  conduct = 2
  density = 1
  expand = 3
  formula = G4_BRASS
  name = G4_BRASS
  specific = 4
FEATURE [App::DocumentObjectGroupPython] Cu_element003  label="Cu_element : 89"  # scripted group (container) (typed FeaturePython)
  n = 89
  ref = Cu_element
FEATURE [App::DocumentObjectGroupPython] Zn_element003  label="Zn_element : 9"  # scripted group (container) (typed FeaturePython)
  n = 9
  ref = Zn_element
FEATURE [App::DocumentObjectGroupPython] Pb_element006  label="Pb_element : 2"  # scripted group (container) (typed FeaturePython)
  n = 2
  ref = Pb_element
FEATURE [App::DocumentObjectGroupPython] G4_BRONZE  # scripted group (container) (typed FeaturePython)
  Dunit = g/cm3
  Dvalue = 8.82
  Group = -> [Cu_element003,Zn_element003,Pb_element006]
  conduct = 2
  density = 1
  expand = 3
  formula = G4_BRONZE
  name = G4_BRONZE
  specific = 4
FEATURE [App::DocumentObjectGroupPython] Fe_element008  label="Fe_element : 74"  # scripted group (container) (typed FeaturePython)
  n = 74
  ref = Fe_element
FEATURE [App::DocumentObjectGroupPython] Cr_element002  label="Cr_element : 18"  # scripted group (container) (typed FeaturePython)
  n = 18
  ref = Cr_element
FEATURE [App::DocumentObjectGroupPython] Ni_element002  label="Ni_element : 8"  # scripted group (container) (typed FeaturePython)
  n = 8
  ref = Ni_element
FEATURE [App::DocumentObjectGroupPython] G4_STAINLESS_STEEL  label="G4_STAINLESS-STEEL"  # scripted group (container) (typed FeaturePython)
  Dunit = g/cm3
  Dvalue = 8
  Group = -> [Fe_element008,Cr_element002,Ni_element002]
  conduct = 2
  density = 1
  expand = 3
  formula = G4_STAINLESS-STEEL
  name = G4_STAINLESS-STEEL
  specific = 4
FEATURE [App::DocumentObjectGroupPython] H_element116  label="H_element : 064"  # scripted group (container) (typed FeaturePython)
  n = 18
  ref = H_element
FEATURE [App::DocumentObjectGroupPython] C_element126  label="C_element : 071"  # scripted group (container) (typed FeaturePython)
  n = 12
  ref = C_element
FEATURE [App::DocumentObjectGroupPython] O_element109  label="O_element : 062"  # scripted group (container) (typed FeaturePython)
  n = 7
  ref = O_element
FEATURE [App::DocumentObjectGroupPython] G4_CR39  # scripted group (container) (typed FeaturePython)
  Dunit = g/cm3
  Dvalue = 1.32
  Group = -> [H_element116,C_element126,O_element109]
  conduct = 2
  density = 1
  expand = 3
  formula = G4_CR39
  name = G4_CR39
  specific = 4
FEATURE [App::DocumentObjectGroupPython] H_element117  label="H_element : 38"  # scripted group (container) (typed FeaturePython)
  n = 38
  ref = H_element
FEATURE [App::DocumentObjectGroupPython] C_element127  label="C_element : 072"  # scripted group (container) (typed FeaturePython)
  n = 18
  ref = C_element
FEATURE [App::DocumentObjectGroupPython] O_element110  label="O_element : 063"  # scripted group (container) (typed FeaturePython)
  n = 1
  ref = O_element
FEATURE [App::DocumentObjectGroupPython] G4_OCTADECANOL  # scripted group (container) (typed FeaturePython)
  Dunit = g/cm3
  Dvalue = 0.812
  Group = -> [H_element117,C_element127,O_element110]
  conduct = 2
  density = 1
  expand = 3
  formula = G4_OCTADECANOL
  name = G4_OCTADECANOL
  specific = 4
FEATURE [App::DocumentObjectGroupPython] HEP  # scripted group (container) (typed FeaturePython)
  Group = -> [G4_lH2,G4_lN2,G4_lO2,G4_lAr,G4_lBr,G4_lKr,G4_lXe,G4_PbWO4,G4_Galactic,G4_GRAPHITE_POROUS,G4_LUCITE,G4_BRASS,G4_BRONZE,G4_STAINLESS_STEEL,G4_CR39,G4_OCTADECANOL]
FEATURE [App::DocumentObjectGroupPython] C_element128  label="C_element : 073"  # scripted group (container) (typed FeaturePython)
  n = 14
  ref = C_element
FEATURE [App::DocumentObjectGroupPython] H_element118  label="H_element : 065"  # scripted group (container) (typed FeaturePython)
  n = 10
  ref = H_element
FEATURE [App::DocumentObjectGroupPython] O_element111  label="O_element : 064"  # scripted group (container) (typed FeaturePython)
  n = 2
  ref = O_element
FEATURE [App::DocumentObjectGroupPython] N_element050  label="N_element : 023"  # scripted group (container) (typed FeaturePython)
  n = 2
  ref = N_element
FEATURE [App::DocumentObjectGroupPython] G4_KEVLAR  # scripted group (container) (typed FeaturePython)
  Dunit = g/cm3
  Dvalue = 1.44
  Group = -> [C_element128,H_element118,O_element111,N_element050]
  conduct = 2
  density = 1
  expand = 3
  formula = G4_KEVLAR
  name = G4_KEVLAR
  specific = 4
FEATURE [App::DocumentObjectGroupPython] C_element129  label="C_element : 074"  # scripted group (container) (typed FeaturePython)
  n = 10
  ref = C_element
FEATURE [App::DocumentObjectGroupPython] H_element119  label="H_element : 066"  # scripted group (container) (typed FeaturePython)
  n = 8
  ref = H_element
FEATURE [App::DocumentObjectGroupPython] O_element112  label="O_element : 065"  # scripted group (container) (typed FeaturePython)
  n = 4
  ref = O_element
FEATURE [App::DocumentObjectGroupPython] G4_DACRON  # scripted group (container) (typed FeaturePython)
  Dunit = g/cm3
  Dvalue = 1.4
  Group = -> [C_element129,H_element119,O_element112]
  conduct = 2
  density = 1
  expand = 3
  formula = G4_DACRON
  name = G4_DACRON
  specific = 4
FEATURE [App::DocumentObjectGroupPython] C_element130  label="C_element : 075"  # scripted group (container) (typed FeaturePython)
  n = 4
  ref = C_element
FEATURE [App::DocumentObjectGroupPython] H_element120  label="H_element : 067"  # scripted group (container) (typed FeaturePython)
  n = 5
  ref = H_element
FEATURE [App::DocumentObjectGroupPython] Cl_element030  label="Cl_element : 016"  # scripted group (container) (typed FeaturePython)
  n = 1
  ref = Cl_element
FEATURE [App::DocumentObjectGroupPython] G4_NEOPRENE  # scripted group (container) (typed FeaturePython)
  Dunit = g/cm3
  Dvalue = 1.23
  Group = -> [C_element130,H_element120,Cl_element030]
  conduct = 2
  density = 1
  expand = 3
  formula = G4_NEOPRENE
  name = G4_NEOPRENE
  specific = 4
FEATURE [App::DocumentObjectGroupPython] Space  # scripted group (container) (typed FeaturePython)
  Group = -> [G4_KEVLAR,G4_DACRON,G4_NEOPRENE]
FEATURE [App::DocumentObjectGroupPython] H_element121  label="H_element : 068"  # scripted group (container) (typed FeaturePython)
  n = 5
  ref = H_element
FEATURE [App::DocumentObjectGroupPython] C_element131  label="C_element : 076"  # scripted group (container) (typed FeaturePython)
  n = 4
  ref = C_element
FEATURE [App::DocumentObjectGroupPython] N_element051  label="N_element : 3"  # scripted group (container) (typed FeaturePython)
  n = 3
  ref = N_element
FEATURE [App::DocumentObjectGroupPython] O_element113  label="O_element : 066"  # scripted group (container) (typed FeaturePython)
  n = 1
  ref = O_element
FEATURE [App::DocumentObjectGroupPython] G4_CYTOSINE  # scripted group (container) (typed FeaturePython)
  Dunit = g/cm3
  Dvalue = 1.55
  Group = -> [H_element121,C_element131,N_element051,O_element113]
  conduct = 2
  density = 1
  expand = 3
  formula = G4_CYTOSINE
  name = G4_CYTOSINE
  specific = 4
FEATURE [App::DocumentObjectGroupPython] H_element122  label="H_element : 069"  # scripted group (container) (typed FeaturePython)
  n = 6
  ref = H_element
FEATURE [App::DocumentObjectGroupPython] C_element132  label="C_element : 077"  # scripted group (container) (typed FeaturePython)
  n = 5
  ref = C_element
FEATURE [App::DocumentObjectGroupPython] N_element052  label="N_element : 024"  # scripted group (container) (typed FeaturePython)
  n = 2
  ref = N_element
FEATURE [App::DocumentObjectGroupPython] O_element114  label="O_element : 067"  # scripted group (container) (typed FeaturePython)
  n = 2
  ref = O_element
FEATURE [App::DocumentObjectGroupPython] G4_THYMINE  # scripted group (container) (typed FeaturePython)
  Dunit = g/cm3
  Dvalue = 1.23
  Group = -> [H_element122,C_element132,N_element052,O_element114]
  conduct = 2
  density = 1
  expand = 3
  formula = G4_THYMINE
  name = G4_THYMINE
  specific = 4
FEATURE [App::DocumentObjectGroupPython] H_element123  label="H_element : 070"  # scripted group (container) (typed FeaturePython)
  n = 4
  ref = H_element
FEATURE [App::DocumentObjectGroupPython] C_element133  label="C_element : 078"  # scripted group (container) (typed FeaturePython)
  n = 4
  ref = C_element
FEATURE [App::DocumentObjectGroupPython] N_element053  label="N_element : 025"  # scripted group (container) (typed FeaturePython)
  n = 2
  ref = N_element
FEATURE [App::DocumentObjectGroupPython] O_element115  label="O_element : 068"  # scripted group (container) (typed FeaturePython)
  n = 2
  ref = O_element
FEATURE [App::DocumentObjectGroupPython] G4_URACIL  # scripted group (container) (typed FeaturePython)
  Dunit = g/cm3
  Dvalue = 1.32
  Group = -> [H_element123,C_element133,N_element053,O_element115]
  conduct = 2
  density = 1
  expand = 3
  formula = G4_URACIL
  name = G4_URACIL
  specific = 4
FEATURE [App::DocumentObjectGroupPython] H_element124  label="H_element : 071"  # scripted group (container) (typed FeaturePython)
  n = 4
  ref = H_element
FEATURE [App::DocumentObjectGroupPython] C_element134  label="C_element : 079"  # scripted group (container) (typed FeaturePython)
  n = 5
  ref = C_element
FEATURE [App::DocumentObjectGroupPython] N_element054  label="N_element : 026"  # scripted group (container) (typed FeaturePython)
  n = 5
  ref = N_element
FEATURE [App::DocumentObjectGroupPython] G4_DNA_ADENINE  # scripted group (container) (typed FeaturePython)
  Dunit = g/cm3
  Dvalue = 1
  Group = -> [H_element124,C_element134,N_element054]
  conduct = 2
  density = 1
  expand = 3
  formula = G4_DNA_ADENINE
  name = G4_DNA_ADENINE
  specific = 4
FEATURE [App::DocumentObjectGroupPython] H_element125  label="H_element : 072"  # scripted group (container) (typed FeaturePython)
  n = 4
  ref = H_element
FEATURE [App::DocumentObjectGroupPython] C_element135  label="C_element : 080"  # scripted group (container) (typed FeaturePython)
  n = 5
  ref = C_element
FEATURE [App::DocumentObjectGroupPython] N_element055  label="N_element : 027"  # scripted group (container) (typed FeaturePython)
  n = 5
  ref = N_element
FEATURE [App::DocumentObjectGroupPython] O_element116  label="O_element : 069"  # scripted group (container) (typed FeaturePython)
  n = 1
  ref = O_element
FEATURE [App::DocumentObjectGroupPython] G4_DNA_GUANINE  # scripted group (container) (typed FeaturePython)
  Dunit = g/cm3
  Dvalue = 1
  Group = -> [H_element125,C_element135,N_element055,O_element116]
  conduct = 2
  density = 1
  expand = 3
  formula = G4_DNA_GUANINE
  name = G4_DNA_GUANINE
  specific = 4
FEATURE [App::DocumentObjectGroupPython] H_element126  label="H_element : 073"  # scripted group (container) (typed FeaturePython)
  n = 4
  ref = H_element
FEATURE [App::DocumentObjectGroupPython] C_element136  label="C_element : 081"  # scripted group (container) (typed FeaturePython)
  n = 4
  ref = C_element
FEATURE [App::DocumentObjectGroupPython] N_element056  label="N_element : 028"  # scripted group (container) (typed FeaturePython)
  n = 3
  ref = N_element
FEATURE [App::DocumentObjectGroupPython] O_element117  label="O_element : 070"  # scripted group (container) (typed FeaturePython)
  n = 1
  ref = O_element
FEATURE [App::DocumentObjectGroupPython] G4_DNA_CYTOSINE  # scripted group (container) (typed FeaturePython)
  Dunit = g/cm3
  Dvalue = 1
  Group = -> [H_element126,C_element136,N_element056,O_element117]
  conduct = 2
  density = 1
  expand = 3
  formula = G4_DNA_CYTOSINE
  name = G4_DNA_CYTOSINE
  specific = 4
FEATURE [App::DocumentObjectGroupPython] H_element127  label="H_element : 074"  # scripted group (container) (typed FeaturePython)
  n = 5
  ref = H_element
FEATURE [App::DocumentObjectGroupPython] C_element137  label="C_element : 082"  # scripted group (container) (typed FeaturePython)
  n = 5
  ref = C_element
FEATURE [App::DocumentObjectGroupPython] N_element057  label="N_element : 029"  # scripted group (container) (typed FeaturePython)
  n = 2
  ref = N_element
FEATURE [App::DocumentObjectGroupPython] O_element118  label="O_element : 071"  # scripted group (container) (typed FeaturePython)
  n = 2
  ref = O_element
FEATURE [App::DocumentObjectGroupPython] G4_DNA_THYMINE  # scripted group (container) (typed FeaturePython)
  Dunit = g/cm3
  Dvalue = 1
  Group = -> [H_element127,C_element137,N_element057,O_element118]
  conduct = 2
  density = 1
  expand = 3
  formula = G4_DNA_THYMINE
  name = G4_DNA_THYMINE
  specific = 4
FEATURE [App::DocumentObjectGroupPython] H_element128  label="H_element : 075"  # scripted group (container) (typed FeaturePython)
  n = 3
  ref = H_element
FEATURE [App::DocumentObjectGroupPython] C_element138  label="C_element : 083"  # scripted group (container) (typed FeaturePython)
  n = 4
  ref = C_element
FEATURE [App::DocumentObjectGroupPython] N_element058  label="N_element : 030"  # scripted group (container) (typed FeaturePython)
  n = 2
  ref = N_element
FEATURE [App::DocumentObjectGroupPython] O_element119  label="O_element : 072"  # scripted group (container) (typed FeaturePython)
  n = 2
  ref = O_element
FEATURE [App::DocumentObjectGroupPython] G4_DNA_URACIL  # scripted group (container) (typed FeaturePython)
  Dunit = g/cm3
  Dvalue = 1
  Group = -> [H_element128,C_element138,N_element058,O_element119]
  conduct = 2
  density = 1
  expand = 3
  formula = G4_DNA_URACIL
  name = G4_DNA_URACIL
  specific = 4
FEATURE [App::DocumentObjectGroupPython] H_element129  label="H_element : 076"  # scripted group (container) (typed FeaturePython)
  n = 10
  ref = H_element
FEATURE [App::DocumentObjectGroupPython] C_element139  label="C_element : 084"  # scripted group (container) (typed FeaturePython)
  n = 10
  ref = C_element
FEATURE [App::DocumentObjectGroupPython] N_element059  label="N_element : 031"  # scripted group (container) (typed FeaturePython)
  n = 5
  ref = N_element
FEATURE [App::DocumentObjectGroupPython] O_element120  label="O_element : 073"  # scripted group (container) (typed FeaturePython)
  n = 4
  ref = O_element
FEATURE [App::DocumentObjectGroupPython] G4_DNA_ADENOSINE  # scripted group (container) (typed FeaturePython)
  Dunit = g/cm3
  Dvalue = 1
  Group = -> [H_element129,C_element139,N_element059,O_element120]
  conduct = 2
  density = 1
  expand = 3
  formula = G4_DNA_ADENOSINE
  name = G4_DNA_ADENOSINE
  specific = 4
FEATURE [App::DocumentObjectGroupPython] H_element130  label="H_element : 077"  # scripted group (container) (typed FeaturePython)
  n = 10
  ref = H_element
FEATURE [App::DocumentObjectGroupPython] C_element140  label="C_element : 085"  # scripted group (container) (typed FeaturePython)
  n = 10
  ref = C_element
FEATURE [App::DocumentObjectGroupPython] N_element060  label="N_element : 032"  # scripted group (container) (typed FeaturePython)
  n = 5
  ref = N_element
FEATURE [App::DocumentObjectGroupPython] O_element121  label="O_element : 074"  # scripted group (container) (typed FeaturePython)
  n = 5
  ref = O_element
FEATURE [App::DocumentObjectGroupPython] G4_DNA_GUANOSINE  # scripted group (container) (typed FeaturePython)
  Dunit = g/cm3
  Dvalue = 1
  Group = -> [H_element130,C_element140,N_element060,O_element121]
  conduct = 2
  density = 1
  expand = 3
  formula = G4_DNA_GUANOSINE
  name = G4_DNA_GUANOSINE
  specific = 4
FEATURE [App::DocumentObjectGroupPython] H_element131  label="H_element : 078"  # scripted group (container) (typed FeaturePython)
  n = 10
  ref = H_element
FEATURE [App::DocumentObjectGroupPython] C_element141  label="C_element : 086"  # scripted group (container) (typed FeaturePython)
  n = 9
  ref = C_element
FEATURE [App::DocumentObjectGroupPython] N_element061  label="N_element : 033"  # scripted group (container) (typed FeaturePython)
  n = 3
  ref = N_element
FEATURE [App::DocumentObjectGroupPython] O_element122  label="O_element : 075"  # scripted group (container) (typed FeaturePython)
  n = 5
  ref = O_element
FEATURE [App::DocumentObjectGroupPython] G4_DNA_CYTIDINE  # scripted group (container) (typed FeaturePython)
  Dunit = g/cm3
  Dvalue = 1
  Group = -> [H_element131,C_element141,N_element061,O_element122]
  conduct = 2
  density = 1
  expand = 3
  formula = G4_DNA_CYTIDINE
  name = G4_DNA_CYTIDINE
  specific = 4
FEATURE [App::DocumentObjectGroupPython] H_element132  label="H_element : 079"  # scripted group (container) (typed FeaturePython)
  n = 9
  ref = H_element
FEATURE [App::DocumentObjectGroupPython] C_element142  label="C_element : 087"  # scripted group (container) (typed FeaturePython)
  n = 9
  ref = C_element
FEATURE [App::DocumentObjectGroupPython] N_element062  label="N_element : 034"  # scripted group (container) (typed FeaturePython)
  n = 2
  ref = N_element
FEATURE [App::DocumentObjectGroupPython] O_element123  label="O_element : 076"  # scripted group (container) (typed FeaturePython)
  n = 6
  ref = O_element
FEATURE [App::DocumentObjectGroupPython] G4_DNA_URIDINE  # scripted group (container) (typed FeaturePython)
  Dunit = g/cm3
  Dvalue = 1
  Group = -> [H_element132,C_element142,N_element062,O_element123]
  conduct = 2
  density = 1
  expand = 3
  formula = G4_DNA_URIDINE
  name = G4_DNA_URIDINE
  specific = 4
FEATURE [App::DocumentObjectGroupPython] H_element133  label="H_element : 080"  # scripted group (container) (typed FeaturePython)
  n = 11
  ref = H_element
FEATURE [App::DocumentObjectGroupPython] C_element143  label="C_element : 088"  # scripted group (container) (typed FeaturePython)
  n = 10
  ref = C_element
FEATURE [App::DocumentObjectGroupPython] N_element063  label="N_element : 035"  # scripted group (container) (typed FeaturePython)
  n = 2
  ref = N_element
FEATURE [App::DocumentObjectGroupPython] O_element124  label="O_element : 077"  # scripted group (container) (typed FeaturePython)
  n = 6
  ref = O_element
FEATURE [App::DocumentObjectGroupPython] G4_DNA_METHYLURIDINE  # scripted group (container) (typed FeaturePython)
  Dunit = g/cm3
  Dvalue = 1
  Group = -> [H_element133,C_element143,N_element063,O_element124]
  conduct = 2
  density = 1
  expand = 3
  formula = G4_DNA_METHYLURIDINE
  name = G4_DNA_METHYLURIDINE
  specific = 4
FEATURE [App::DocumentObjectGroupPython] P_element014  label="P_element : 003"  # scripted group (container) (typed FeaturePython)
  n = 1
  ref = P_element
FEATURE [App::DocumentObjectGroupPython] O_element125  label="O_element : 078"  # scripted group (container) (typed FeaturePython)
  n = 3
  ref = O_element
FEATURE [App::DocumentObjectGroupPython] G4_DNA_MONOPHOSPHATE  # scripted group (container) (typed FeaturePython)
  Dunit = g/cm3
  Dvalue = 1
  Group = -> [P_element014,O_element125]
  conduct = 2
  density = 1
  expand = 3
  formula = G4_DNA_MONOPHOSPHATE
  name = G4_DNA_MONOPHOSPHATE
  specific = 4
FEATURE [App::DocumentObjectGroupPython] H_element134  label="H_element : 081"  # scripted group (container) (typed FeaturePython)
  n = 10
  ref = H_element
FEATURE [App::DocumentObjectGroupPython] C_element144  label="C_element : 089"  # scripted group (container) (typed FeaturePython)
  n = 10
  ref = C_element
FEATURE [App::DocumentObjectGroupPython] N_element064  label="N_element : 036"  # scripted group (container) (typed FeaturePython)
  n = 5
  ref = N_element
FEATURE [App::DocumentObjectGroupPython] O_element126  label="O_element : 079"  # scripted group (container) (typed FeaturePython)
  n = 7
  ref = O_element
FEATURE [App::DocumentObjectGroupPython] P_element015  label="P_element : 004"  # scripted group (container) (typed FeaturePython)
  n = 1
  ref = P_element
FEATURE [App::DocumentObjectGroupPython] G4_DNA_A  # scripted group (container) (typed FeaturePython)
  Dunit = g/cm3
  Dvalue = 1
  Group = -> [H_element134,C_element144,N_element064,O_element126,P_element015]
  conduct = 2
  density = 1
  expand = 3
  formula = G4_DNA_A
  name = G4_DNA_A
  specific = 4
FEATURE [App::DocumentObjectGroupPython] H_element135  label="H_element : 082"  # scripted group (container) (typed FeaturePython)
  n = 10
  ref = H_element
FEATURE [App::DocumentObjectGroupPython] C_element145  label="C_element : 090"  # scripted group (container) (typed FeaturePython)
  n = 10
  ref = C_element
FEATURE [App::DocumentObjectGroupPython] N_element065  label="N_element : 037"  # scripted group (container) (typed FeaturePython)
  n = 5
  ref = N_element
FEATURE [App::DocumentObjectGroupPython] O_element127  label="O_element : 8"  # scripted group (container) (typed FeaturePython)
  n = 8
  ref = O_element
FEATURE [App::DocumentObjectGroupPython] P_element016  label="P_element : 005"  # scripted group (container) (typed FeaturePython)
  n = 1
  ref = P_element
FEATURE [App::DocumentObjectGroupPython] G4_DNA_G  # scripted group (container) (typed FeaturePython)
  Dunit = g/cm3
  Dvalue = 1
  Group = -> [H_element135,C_element145,N_element065,O_element127,P_element016]
  conduct = 2
  density = 1
  expand = 3
  formula = G4_DNA_G
  name = G4_DNA_G
  specific = 4
FEATURE [App::DocumentObjectGroupPython] H_element136  label="H_element : 083"  # scripted group (container) (typed FeaturePython)
  n = 10
  ref = H_element
FEATURE [App::DocumentObjectGroupPython] C_element146  label="C_element : 091"  # scripted group (container) (typed FeaturePython)
  n = 9
  ref = C_element
FEATURE [App::DocumentObjectGroupPython] N_element066  label="N_element : 038"  # scripted group (container) (typed FeaturePython)
  n = 3
  ref = N_element
FEATURE [App::DocumentObjectGroupPython] O_element128  label="O_element : 080"  # scripted group (container) (typed FeaturePython)
  n = 8
  ref = O_element
FEATURE [App::DocumentObjectGroupPython] P_element017  label="P_element : 006"  # scripted group (container) (typed FeaturePython)
  n = 1
  ref = P_element
FEATURE [App::DocumentObjectGroupPython] G4_DNA_C  # scripted group (container) (typed FeaturePython)
  Dunit = g/cm3
  Dvalue = 1
  Group = -> [H_element136,C_element146,N_element066,O_element128,P_element017]
  conduct = 2
  density = 1
  expand = 3
  formula = G4_DNA_C
  name = G4_DNA_C
  specific = 4
FEATURE [App::DocumentObjectGroupPython] H_element137  label="H_element : 084"  # scripted group (container) (typed FeaturePython)
  n = 9
  ref = H_element
FEATURE [App::DocumentObjectGroupPython] C_element147  label="C_element : 092"  # scripted group (container) (typed FeaturePython)
  n = 9
  ref = C_element
FEATURE [App::DocumentObjectGroupPython] N_element067  label="N_element : 039"  # scripted group (container) (typed FeaturePython)
  n = 2
  ref = N_element
FEATURE [App::DocumentObjectGroupPython] O_element129  label="O_element : 9"  # scripted group (container) (typed FeaturePython)
  n = 9
  ref = O_element
FEATURE [App::DocumentObjectGroupPython] P_element018  label="P_element : 007"  # scripted group (container) (typed FeaturePython)
  n = 1
  ref = P_element
FEATURE [App::DocumentObjectGroupPython] G4_DNA_U  # scripted group (container) (typed FeaturePython)
  Dunit = g/cm3
  Dvalue = 1
  Group = -> [H_element137,C_element147,N_element067,O_element129,P_element018]
  conduct = 2
  density = 1
  expand = 3
  formula = G4_DNA_U
  name = G4_DNA_U
  specific = 4
FEATURE [App::DocumentObjectGroupPython] H_element138  label="H_element : 085"  # scripted group (container) (typed FeaturePython)
  n = 11
  ref = H_element
FEATURE [App::DocumentObjectGroupPython] C_element148  label="C_element : 093"  # scripted group (container) (typed FeaturePython)
  n = 10
  ref = C_element
FEATURE [App::DocumentObjectGroupPython] N_element068  label="N_element : 040"  # scripted group (container) (typed FeaturePython)
  n = 2
  ref = N_element
FEATURE [App::DocumentObjectGroupPython] O_element130  label="O_element : 081"  # scripted group (container) (typed FeaturePython)
  n = 9
  ref = O_element
FEATURE [App::DocumentObjectGroupPython] P_element019  label="P_element : 008"  # scripted group (container) (typed FeaturePython)
  n = 1
  ref = P_element
FEATURE [App::DocumentObjectGroupPython] G4_DNA_MU  # scripted group (container) (typed FeaturePython)
  Dunit = g/cm3
  Dvalue = 1
  Group = -> [H_element138,C_element148,N_element068,O_element130,P_element019]
  conduct = 2
  density = 1
  expand = 3
  formula = G4_DNA_MU
  name = G4_DNA_MU
  specific = 4
FEATURE [App::DocumentObjectGroupPython] BioChemical  # scripted group (container) (typed FeaturePython)
  Group = -> [G4_CYTOSINE,G4_THYMINE,G4_URACIL,G4_DNA_ADENINE,G4_DNA_GUANINE,G4_DNA_CYTOSINE,G4_DNA_THYMINE,G4_DNA_URACIL,G4_DNA_ADENOSINE,G4_DNA_GUANOSINE,G4_DNA_CYTIDINE,G4_DNA_URIDINE,G4_DNA_METHYLURIDINE,G4_DNA_MONOPHOSPHATE,G4_DNA_A,G4_DNA_G,G4_DNA_C,G4_DNA_U,G4_DNA_MU]
FEATURE [App::DocumentObjectGroupPython] G4Materials  # scripted group (container) (typed FeaturePython)
  Group = -> [NIST,Element,HEP,Space,BioChemical]
  version = 1
FEATURE [App::DocumentObjectGroupPython] Geant4  # scripted group (container) (typed FeaturePython)
  Group = -> [G4Isotopes,G4Elements,G4Materials]
FEATURE [App::DocumentObjectGroupPython] Materials  # scripted group (container) (typed FeaturePython)
  Group = -> [Geant4]
FEATURE [Part::FeaturePython] GDMLBox_WorldBox  # WARN: FeaturePython — macro-defined, semantics opaque (R4)
  lunit = 2
  material = 5
  x = 452.792
  y = 452.792
  z = 169
FEATURE [Part::FeaturePython] GDMLBox_Box  # WARN: FeaturePython — macro-defined, semantics opaque (R4)
  Placement = pos=(20,0,0) rot=(0,0,1;0rad)
  lunit = 2
  material = 0
  x = 10
  y = 10
  z = 10
FEATURE [Part::FeaturePython] GDMLTube  # WARN: FeaturePython — macro-defined, semantics opaque (R4)
  Placement = pos=(17,-4,0) rot=(0,0,1;0rad)
  aunit = 1
  deltaphi = 90
  lunit = 2
  material = 0
  rmax = 7
  rmin = 5
  startphi = 0
  z = 7
FEATURE [App::Part] LV_Tube
  Group = -> [GDMLTube]
  Origin = -> Origin003
  SkinSurface = 0
FEATURE [App::Part] LV_Box
  Group = -> [GDMLBox_Box,LV_Tube]
  Origin = -> Origin002
  Placement = pos=(0,0,0) rot=(0,0,1;-0.523599rad)
FEATURE [Part::FeaturePython] Array  # Draft array (typed FeaturePython)
  AlwaysSyncPlacement = false
  Angle = 180
  ArrayType = 1
  Axis = (0,0,1)
  Base = -> LV_Box
  Center = (-20,-20,0)
  Count = 5
  ExpandArray = false
  Fuse = false
  IntervalAxis = (0,0,0)
  IntervalX = (100,0,0)
  IntervalY = (0,100,0)
  IntervalZ = (0,0,100)
  NumberCircles = 3
  NumberPolar = 5
  NumberX = 2
  NumberY = 2
  NumberZ = 1
  PlacementList = 5 placements: [(0,0,0),(-20,8.28427,0),(-40,3.55271e-15,0),(-48.2843,-20,0),(-40,-40,0)]
  RadialDistance = 50
  ScaleList = (5) [(1,1,1),(1,1,1),(1,1,1),(1,1,1),(1,1,1)]
  Symmetry = 1
  TangentialDistance = 25
FEATURE [App::Part] Part  label="experiment"
  Group = -> [LV_Box,Array]
  Origin = -> Origin001
FEATURE [Part::FeaturePython] Array001  # Draft array (typed FeaturePython)
  AlwaysSyncPlacement = false
  Angle = 360
  ArrayType = 0
  Axis = (0,0,1)
  Base = -> Part
  Center = (0,0,0)
  Count = 4
  ExpandArray = false
  Fuse = true
  IntervalAxis = (0,0,0)
  IntervalX = (150,0,0)
  IntervalY = (0,150,0)
  IntervalZ = (0,0,100)
  NumberCircles = 3
  NumberPolar = 5
  NumberX = 2
  NumberY = 2
  NumberZ = 1
  PlacementList = 4 placements: [(0,0,0),(0,150,0),(150,0,0),(150,150,0)]
  RadialDistance = 50
  ScaleList = (4) [(1,1,1),(1,1,1),(1,1,1),(1,1,1)]
  Symmetry = 1
  TangentialDistance = 25
FEATURE [App::Part] Part001
  Group = -> [Part,Array001]
  Origin = -> Origin004
FEATURE [App::Part] worldVOL
  Group = -> [GDMLBox_WorldBox,Part001]
  Origin = -> Origin
